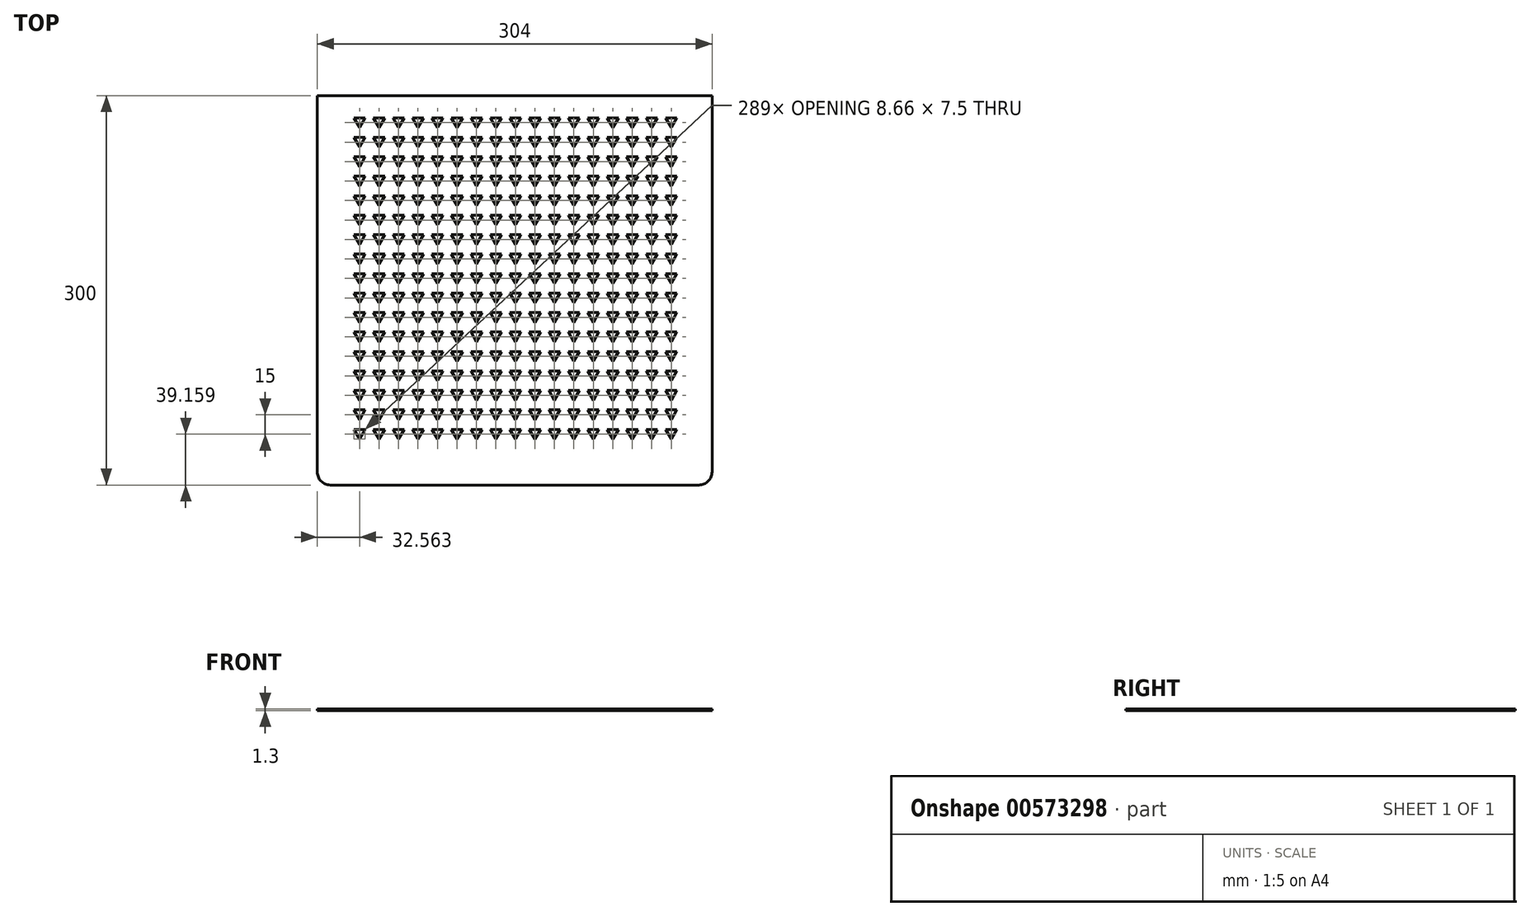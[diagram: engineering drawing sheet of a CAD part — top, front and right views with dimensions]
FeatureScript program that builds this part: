
annotation { "Feature Type Name" : "Feature", "Feature Type Description" : "" }
export const myFeature = defineFeature(function(context is Context, id is Id, definition is map)
    precondition{}
    {
        {
            var Q0;
            Q0=qCreatedBy(makeId("Top.planeOp"),FACE);
            var sketch = newSketch(context, id + "F0", { "sketchPlane" : qUnion([Q0])});
            skLineSegment(sketch, "E0.bottom", {"start": v(152, 150) * mm, "end": v(-152, 150) * mm});
            skLineSegment(sketch, "E0.top", {"start": v(152, -150) * mm, "end": v(-152, -150) * mm});
            skLineSegment(sketch, "E0.left", {"start": v(152, 150) * mm, "end": v(152, -150) * mm});
            skLineSegment(sketch, "E0.right", {"start": v(-152, 150) * mm, "end": v(-152, -150) * mm});
            skPoint(sketch, "E0.middle", {"position": v(0, 0) * mm});
            skSolve(sketch);
        }
        {
            var Q0;
            Q0=makeQuery(id+"F0.imprint","IMPRINT",FACE,{"disambiguationData":[TD([[makeQuery(id+"F0.imprint","IMPRINT",EDGE,{"derivedFrom":sQuery(id+"F0.wireOp",EDGE,"E0.bottom")}),1.0]])]});
            extrude(context, id + "F1", {"entities" : qUnion([Q0]), "depth" : 1.3 * mm, "offsetDistance" : 25 * mm});
        }
        {
            var Q0;
            Q0=makeQuery(id+"F1.opExtrude","SWEPT_EDGE",EDGE,{"disambiguationData":[OSD([sQuery(id+"F0.wireOp",EDGE,"E0.top"),sQuery(id+"F0.wireOp",EDGE,"E0.left")])]});
            var Q1;
            Q1=makeQuery(id+"F1.opExtrude","SWEPT_EDGE",EDGE,{"disambiguationData":[OSD([sQuery(id+"F0.wireOp",EDGE,"E0.top"),sQuery(id+"F0.wireOp",EDGE,"E0.right")])]});
            fillet(context, id + "F2", {"entities" : qUnion([Q0, Q1]), "radius" : 10 * mm, "tangentPropagation" : true, "allowEdgeOverflow" : false});
        }
        {
            var Q0;
            Q0=makeQuery(id+"F1.opExtrude","CAP_FACE",FACE,{"disambiguationData":[OSD([sQuery(id+"F0.wireOp",EDGE,"E0.bottom"),sQuery(id+"F0.wireOp",EDGE,"E0.top"),sQuery(id+"F0.wireOp",EDGE,"E0.left"),sQuery(id+"F0.wireOp",EDGE,"E0.right")])],"isStart":false});
            var sketch = newSketch(context, id + "F3", { "sketchPlane" : qUnion([Q0])});
            skLineSegment(sketch, "E1.0", {"start": v(-123.77, 132.9) * mm, "end": v(-115.1, 132.9) * mm});
            skLineSegment(sketch, "E1.1", {"start": v(-115.1, 132.9) * mm, "end": v(-119.44, 125.41) * mm});
            skLineSegment(sketch, "E1.2", {"start": v(-119.44, 125.41) * mm, "end": v(-123.77, 132.9) * mm});
            skPoint(sketch, "E1.0.midPoint", {"position": v(-119.44, 132.9) * mm});
            skLineSegment(sketch, "E2.0.1.0", {"start": v(-115.1, 117.9) * mm, "end": v(-119.44, 110.41) * mm});
            skLineSegment(sketch, "E2.0.1.1", {"start": v(-119.44, 110.41) * mm, "end": v(-123.77, 117.9) * mm});
            skLineSegment(sketch, "E2.0.1.2", {"start": v(-123.77, 117.9) * mm, "end": v(-115.1, 117.9) * mm});
            skLineSegment(sketch, "E2.0.2.0", {"start": v(-115.1, 102.9) * mm, "end": v(-119.44, 95.41) * mm});
            skLineSegment(sketch, "E2.0.2.1", {"start": v(-119.44, 95.41) * mm, "end": v(-123.77, 102.9) * mm});
            skLineSegment(sketch, "E2.0.2.2", {"start": v(-123.77, 102.9) * mm, "end": v(-115.1, 102.9) * mm});
            skLineSegment(sketch, "E2.0.3.0", {"start": v(-115.1, 87.9) * mm, "end": v(-119.44, 80.41) * mm});
            skLineSegment(sketch, "E2.0.3.1", {"start": v(-119.44, 80.41) * mm, "end": v(-123.77, 87.9) * mm});
            skLineSegment(sketch, "E2.0.3.2", {"start": v(-123.77, 87.9) * mm, "end": v(-115.1, 87.9) * mm});
            skLineSegment(sketch, "E2.0.4.0", {"start": v(-115.1, 72.9) * mm, "end": v(-119.44, 65.41) * mm});
            skLineSegment(sketch, "E2.0.4.1", {"start": v(-119.44, 65.41) * mm, "end": v(-123.77, 72.9) * mm});
            skLineSegment(sketch, "E2.0.4.2", {"start": v(-123.77, 72.9) * mm, "end": v(-115.1, 72.9) * mm});
            skLineSegment(sketch, "E2.0.5.0", {"start": v(-115.1, 57.9) * mm, "end": v(-119.44, 50.41) * mm});
            skLineSegment(sketch, "E2.0.5.1", {"start": v(-119.44, 50.41) * mm, "end": v(-123.77, 57.9) * mm});
            skLineSegment(sketch, "E2.0.5.2", {"start": v(-123.77, 57.9) * mm, "end": v(-115.1, 57.9) * mm});
            skLineSegment(sketch, "E2.0.6.0", {"start": v(-115.1, 42.9) * mm, "end": v(-119.44, 35.41) * mm});
            skLineSegment(sketch, "E2.0.6.1", {"start": v(-119.44, 35.41) * mm, "end": v(-123.77, 42.9) * mm});
            skLineSegment(sketch, "E2.0.6.2", {"start": v(-123.77, 42.9) * mm, "end": v(-115.1, 42.9) * mm});
            skLineSegment(sketch, "E2.0.7.0", {"start": v(-115.1, 27.9) * mm, "end": v(-119.44, 20.41) * mm});
            skLineSegment(sketch, "E2.0.7.1", {"start": v(-119.44, 20.41) * mm, "end": v(-123.77, 27.9) * mm});
            skLineSegment(sketch, "E2.0.7.2", {"start": v(-123.77, 27.9) * mm, "end": v(-115.1, 27.9) * mm});
            skLineSegment(sketch, "E2.0.8.0", {"start": v(-115.1, 12.9) * mm, "end": v(-119.44, 5.41) * mm});
            skLineSegment(sketch, "E2.0.8.1", {"start": v(-119.44, 5.41) * mm, "end": v(-123.77, 12.9) * mm});
            skLineSegment(sketch, "E2.0.8.2", {"start": v(-123.77, 12.9) * mm, "end": v(-115.1, 12.9) * mm});
            skLineSegment(sketch, "E2.0.9.0", {"start": v(-115.1, -2.1) * mm, "end": v(-119.44, -9.59) * mm});
            skLineSegment(sketch, "E2.0.9.1", {"start": v(-119.44, -9.59) * mm, "end": v(-123.77, -2.1) * mm});
            skLineSegment(sketch, "E2.0.9.2", {"start": v(-123.77, -2.1) * mm, "end": v(-115.1, -2.1) * mm});
            skLineSegment(sketch, "E2.0.10.0", {"start": v(-115.1, -17.1) * mm, "end": v(-119.44, -24.59) * mm});
            skLineSegment(sketch, "E2.0.10.1", {"start": v(-119.44, -24.59) * mm, "end": v(-123.77, -17.1) * mm});
            skLineSegment(sketch, "E2.0.10.2", {"start": v(-123.77, -17.1) * mm, "end": v(-115.1, -17.1) * mm});
            skLineSegment(sketch, "E2.0.11.0", {"start": v(-115.1, -32.1) * mm, "end": v(-119.44, -39.59) * mm});
            skLineSegment(sketch, "E2.0.11.1", {"start": v(-119.44, -39.59) * mm, "end": v(-123.77, -32.1) * mm});
            skLineSegment(sketch, "E2.0.11.2", {"start": v(-123.77, -32.1) * mm, "end": v(-115.1, -32.1) * mm});
            skLineSegment(sketch, "E2.0.12.0", {"start": v(-115.1, -47.1) * mm, "end": v(-119.44, -54.59) * mm});
            skLineSegment(sketch, "E2.0.12.1", {"start": v(-119.44, -54.59) * mm, "end": v(-123.77, -47.1) * mm});
            skLineSegment(sketch, "E2.0.12.2", {"start": v(-123.77, -47.1) * mm, "end": v(-115.1, -47.1) * mm});
            skLineSegment(sketch, "E2.0.13.0", {"start": v(-115.1, -62.1) * mm, "end": v(-119.44, -69.59) * mm});
            skLineSegment(sketch, "E2.0.13.1", {"start": v(-119.44, -69.59) * mm, "end": v(-123.77, -62.1) * mm});
            skLineSegment(sketch, "E2.0.13.2", {"start": v(-123.77, -62.1) * mm, "end": v(-115.1, -62.1) * mm});
            skLineSegment(sketch, "E2.0.14.0", {"start": v(-115.1, -77.1) * mm, "end": v(-119.44, -84.59) * mm});
            skLineSegment(sketch, "E2.0.14.1", {"start": v(-119.44, -84.59) * mm, "end": v(-123.77, -77.1) * mm});
            skLineSegment(sketch, "E2.0.14.2", {"start": v(-123.77, -77.1) * mm, "end": v(-115.1, -77.1) * mm});
            skLineSegment(sketch, "E2.0.15.0", {"start": v(-115.1, -92.1) * mm, "end": v(-119.44, -99.59) * mm});
            skLineSegment(sketch, "E2.0.15.1", {"start": v(-119.44, -99.59) * mm, "end": v(-123.77, -92.1) * mm});
            skLineSegment(sketch, "E2.0.15.2", {"start": v(-123.77, -92.1) * mm, "end": v(-115.1, -92.1) * mm});
            skLineSegment(sketch, "E2.0.16.0", {"start": v(-115.1, -107.1) * mm, "end": v(-119.44, -114.59) * mm});
            skLineSegment(sketch, "E2.0.16.1", {"start": v(-119.44, -114.59) * mm, "end": v(-123.77, -107.1) * mm});
            skLineSegment(sketch, "E2.0.16.2", {"start": v(-123.77, -107.1) * mm, "end": v(-115.1, -107.1) * mm});
            skLineSegment(sketch, "E2.1.0.0", {"start": v(-100.1, 132.9) * mm, "end": v(-104.44, 125.41) * mm});
            skLineSegment(sketch, "E2.1.0.1", {"start": v(-104.44, 125.41) * mm, "end": v(-108.77, 132.9) * mm});
            skLineSegment(sketch, "E2.1.0.2", {"start": v(-108.77, 132.9) * mm, "end": v(-100.1, 132.9) * mm});
            skLineSegment(sketch, "E2.1.1.0", {"start": v(-100.1, 117.9) * mm, "end": v(-104.44, 110.41) * mm});
            skLineSegment(sketch, "E2.1.1.1", {"start": v(-104.44, 110.41) * mm, "end": v(-108.77, 117.9) * mm});
            skLineSegment(sketch, "E2.1.1.2", {"start": v(-108.77, 117.9) * mm, "end": v(-100.1, 117.9) * mm});
            skLineSegment(sketch, "E2.1.2.0", {"start": v(-100.1, 102.9) * mm, "end": v(-104.44, 95.41) * mm});
            skLineSegment(sketch, "E2.1.2.1", {"start": v(-104.44, 95.41) * mm, "end": v(-108.77, 102.9) * mm});
            skLineSegment(sketch, "E2.1.2.2", {"start": v(-108.77, 102.9) * mm, "end": v(-100.1, 102.9) * mm});
            skLineSegment(sketch, "E2.1.3.0", {"start": v(-100.1, 87.9) * mm, "end": v(-104.44, 80.41) * mm});
            skLineSegment(sketch, "E2.1.3.1", {"start": v(-104.44, 80.41) * mm, "end": v(-108.77, 87.9) * mm});
            skLineSegment(sketch, "E2.1.3.2", {"start": v(-108.77, 87.9) * mm, "end": v(-100.1, 87.9) * mm});
            skLineSegment(sketch, "E2.1.4.0", {"start": v(-100.1, 72.9) * mm, "end": v(-104.44, 65.41) * mm});
            skLineSegment(sketch, "E2.1.4.1", {"start": v(-104.44, 65.41) * mm, "end": v(-108.77, 72.9) * mm});
            skLineSegment(sketch, "E2.1.4.2", {"start": v(-108.77, 72.9) * mm, "end": v(-100.1, 72.9) * mm});
            skLineSegment(sketch, "E2.1.5.0", {"start": v(-100.1, 57.9) * mm, "end": v(-104.44, 50.41) * mm});
            skLineSegment(sketch, "E2.1.5.1", {"start": v(-104.44, 50.41) * mm, "end": v(-108.77, 57.9) * mm});
            skLineSegment(sketch, "E2.1.5.2", {"start": v(-108.77, 57.9) * mm, "end": v(-100.1, 57.9) * mm});
            skLineSegment(sketch, "E2.1.6.0", {"start": v(-100.1, 42.9) * mm, "end": v(-104.44, 35.41) * mm});
            skLineSegment(sketch, "E2.1.6.1", {"start": v(-104.44, 35.41) * mm, "end": v(-108.77, 42.9) * mm});
            skLineSegment(sketch, "E2.1.6.2", {"start": v(-108.77, 42.9) * mm, "end": v(-100.1, 42.9) * mm});
            skLineSegment(sketch, "E2.1.7.0", {"start": v(-100.1, 27.9) * mm, "end": v(-104.44, 20.41) * mm});
            skLineSegment(sketch, "E2.1.7.1", {"start": v(-104.44, 20.41) * mm, "end": v(-108.77, 27.9) * mm});
            skLineSegment(sketch, "E2.1.7.2", {"start": v(-108.77, 27.9) * mm, "end": v(-100.1, 27.9) * mm});
            skLineSegment(sketch, "E2.1.8.0", {"start": v(-100.1, 12.9) * mm, "end": v(-104.44, 5.41) * mm});
            skLineSegment(sketch, "E2.1.8.1", {"start": v(-104.44, 5.41) * mm, "end": v(-108.77, 12.9) * mm});
            skLineSegment(sketch, "E2.1.8.2", {"start": v(-108.77, 12.9) * mm, "end": v(-100.1, 12.9) * mm});
            skLineSegment(sketch, "E2.1.9.0", {"start": v(-100.1, -2.1) * mm, "end": v(-104.44, -9.59) * mm});
            skLineSegment(sketch, "E2.1.9.1", {"start": v(-104.44, -9.59) * mm, "end": v(-108.77, -2.1) * mm});
            skLineSegment(sketch, "E2.1.9.2", {"start": v(-108.77, -2.1) * mm, "end": v(-100.1, -2.1) * mm});
            skLineSegment(sketch, "E2.1.10.0", {"start": v(-100.1, -17.1) * mm, "end": v(-104.44, -24.59) * mm});
            skLineSegment(sketch, "E2.1.10.1", {"start": v(-104.44, -24.59) * mm, "end": v(-108.77, -17.1) * mm});
            skLineSegment(sketch, "E2.1.10.2", {"start": v(-108.77, -17.1) * mm, "end": v(-100.1, -17.1) * mm});
            skLineSegment(sketch, "E2.1.11.0", {"start": v(-100.1, -32.1) * mm, "end": v(-104.44, -39.59) * mm});
            skLineSegment(sketch, "E2.1.11.1", {"start": v(-104.44, -39.59) * mm, "end": v(-108.77, -32.1) * mm});
            skLineSegment(sketch, "E2.1.11.2", {"start": v(-108.77, -32.1) * mm, "end": v(-100.1, -32.1) * mm});
            skLineSegment(sketch, "E2.1.12.0", {"start": v(-100.1, -47.1) * mm, "end": v(-104.44, -54.59) * mm});
            skLineSegment(sketch, "E2.1.12.1", {"start": v(-104.44, -54.59) * mm, "end": v(-108.77, -47.1) * mm});
            skLineSegment(sketch, "E2.1.12.2", {"start": v(-108.77, -47.1) * mm, "end": v(-100.1, -47.1) * mm});
            skLineSegment(sketch, "E2.1.13.0", {"start": v(-100.1, -62.1) * mm, "end": v(-104.44, -69.59) * mm});
            skLineSegment(sketch, "E2.1.13.1", {"start": v(-104.44, -69.59) * mm, "end": v(-108.77, -62.1) * mm});
            skLineSegment(sketch, "E2.1.13.2", {"start": v(-108.77, -62.1) * mm, "end": v(-100.1, -62.1) * mm});
            skLineSegment(sketch, "E2.1.14.0", {"start": v(-100.1, -77.1) * mm, "end": v(-104.44, -84.59) * mm});
            skLineSegment(sketch, "E2.1.14.1", {"start": v(-104.44, -84.59) * mm, "end": v(-108.77, -77.1) * mm});
            skLineSegment(sketch, "E2.1.14.2", {"start": v(-108.77, -77.1) * mm, "end": v(-100.1, -77.1) * mm});
            skLineSegment(sketch, "E2.1.15.0", {"start": v(-100.1, -92.1) * mm, "end": v(-104.44, -99.59) * mm});
            skLineSegment(sketch, "E2.1.15.1", {"start": v(-104.44, -99.59) * mm, "end": v(-108.77, -92.1) * mm});
            skLineSegment(sketch, "E2.1.15.2", {"start": v(-108.77, -92.1) * mm, "end": v(-100.1, -92.1) * mm});
            skLineSegment(sketch, "E2.1.16.0", {"start": v(-100.1, -107.1) * mm, "end": v(-104.44, -114.59) * mm});
            skLineSegment(sketch, "E2.1.16.1", {"start": v(-104.44, -114.59) * mm, "end": v(-108.77, -107.1) * mm});
            skLineSegment(sketch, "E2.1.16.2", {"start": v(-108.77, -107.1) * mm, "end": v(-100.1, -107.1) * mm});
            skLineSegment(sketch, "E2.2.0.0", {"start": v(-85.1, 132.9) * mm, "end": v(-89.44, 125.41) * mm});
            skLineSegment(sketch, "E2.2.0.1", {"start": v(-89.44, 125.41) * mm, "end": v(-93.77, 132.9) * mm});
            skLineSegment(sketch, "E2.2.0.2", {"start": v(-93.77, 132.9) * mm, "end": v(-85.1, 132.9) * mm});
            skLineSegment(sketch, "E2.2.1.0", {"start": v(-85.1, 117.9) * mm, "end": v(-89.44, 110.41) * mm});
            skLineSegment(sketch, "E2.2.1.1", {"start": v(-89.44, 110.41) * mm, "end": v(-93.77, 117.9) * mm});
            skLineSegment(sketch, "E2.2.1.2", {"start": v(-93.77, 117.9) * mm, "end": v(-85.1, 117.9) * mm});
            skLineSegment(sketch, "E2.2.2.0", {"start": v(-85.1, 102.9) * mm, "end": v(-89.44, 95.41) * mm});
            skLineSegment(sketch, "E2.2.2.1", {"start": v(-89.44, 95.41) * mm, "end": v(-93.77, 102.9) * mm});
            skLineSegment(sketch, "E2.2.2.2", {"start": v(-93.77, 102.9) * mm, "end": v(-85.1, 102.9) * mm});
            skLineSegment(sketch, "E2.2.3.0", {"start": v(-85.1, 87.9) * mm, "end": v(-89.44, 80.41) * mm});
            skLineSegment(sketch, "E2.2.3.1", {"start": v(-89.44, 80.41) * mm, "end": v(-93.77, 87.9) * mm});
            skLineSegment(sketch, "E2.2.3.2", {"start": v(-93.77, 87.9) * mm, "end": v(-85.1, 87.9) * mm});
            skLineSegment(sketch, "E2.2.4.0", {"start": v(-85.1, 72.9) * mm, "end": v(-89.44, 65.41) * mm});
            skLineSegment(sketch, "E2.2.4.1", {"start": v(-89.44, 65.41) * mm, "end": v(-93.77, 72.9) * mm});
            skLineSegment(sketch, "E2.2.4.2", {"start": v(-93.77, 72.9) * mm, "end": v(-85.1, 72.9) * mm});
            skLineSegment(sketch, "E2.2.5.0", {"start": v(-85.1, 57.9) * mm, "end": v(-89.44, 50.41) * mm});
            skLineSegment(sketch, "E2.2.5.1", {"start": v(-89.44, 50.41) * mm, "end": v(-93.77, 57.9) * mm});
            skLineSegment(sketch, "E2.2.5.2", {"start": v(-93.77, 57.9) * mm, "end": v(-85.1, 57.9) * mm});
            skLineSegment(sketch, "E2.2.6.0", {"start": v(-85.1, 42.9) * mm, "end": v(-89.44, 35.41) * mm});
            skLineSegment(sketch, "E2.2.6.1", {"start": v(-89.44, 35.41) * mm, "end": v(-93.77, 42.9) * mm});
            skLineSegment(sketch, "E2.2.6.2", {"start": v(-93.77, 42.9) * mm, "end": v(-85.1, 42.9) * mm});
            skLineSegment(sketch, "E2.2.7.0", {"start": v(-85.1, 27.9) * mm, "end": v(-89.44, 20.41) * mm});
            skLineSegment(sketch, "E2.2.7.1", {"start": v(-89.44, 20.41) * mm, "end": v(-93.77, 27.9) * mm});
            skLineSegment(sketch, "E2.2.7.2", {"start": v(-93.77, 27.9) * mm, "end": v(-85.1, 27.9) * mm});
            skLineSegment(sketch, "E2.2.8.0", {"start": v(-85.1, 12.9) * mm, "end": v(-89.44, 5.41) * mm});
            skLineSegment(sketch, "E2.2.8.1", {"start": v(-89.44, 5.41) * mm, "end": v(-93.77, 12.9) * mm});
            skLineSegment(sketch, "E2.2.8.2", {"start": v(-93.77, 12.9) * mm, "end": v(-85.1, 12.9) * mm});
            skLineSegment(sketch, "E2.2.9.0", {"start": v(-85.1, -2.1) * mm, "end": v(-89.44, -9.59) * mm});
            skLineSegment(sketch, "E2.2.9.1", {"start": v(-89.44, -9.59) * mm, "end": v(-93.77, -2.1) * mm});
            skLineSegment(sketch, "E2.2.9.2", {"start": v(-93.77, -2.1) * mm, "end": v(-85.1, -2.1) * mm});
            skLineSegment(sketch, "E2.2.10.0", {"start": v(-85.1, -17.1) * mm, "end": v(-89.44, -24.59) * mm});
            skLineSegment(sketch, "E2.2.10.1", {"start": v(-89.44, -24.59) * mm, "end": v(-93.77, -17.1) * mm});
            skLineSegment(sketch, "E2.2.10.2", {"start": v(-93.77, -17.1) * mm, "end": v(-85.1, -17.1) * mm});
            skLineSegment(sketch, "E2.2.11.0", {"start": v(-85.1, -32.1) * mm, "end": v(-89.44, -39.59) * mm});
            skLineSegment(sketch, "E2.2.11.1", {"start": v(-89.44, -39.59) * mm, "end": v(-93.77, -32.1) * mm});
            skLineSegment(sketch, "E2.2.11.2", {"start": v(-93.77, -32.1) * mm, "end": v(-85.1, -32.1) * mm});
            skLineSegment(sketch, "E2.2.12.0", {"start": v(-85.1, -47.1) * mm, "end": v(-89.44, -54.59) * mm});
            skLineSegment(sketch, "E2.2.12.1", {"start": v(-89.44, -54.59) * mm, "end": v(-93.77, -47.1) * mm});
            skLineSegment(sketch, "E2.2.12.2", {"start": v(-93.77, -47.1) * mm, "end": v(-85.1, -47.1) * mm});
            skLineSegment(sketch, "E2.2.13.0", {"start": v(-85.1, -62.1) * mm, "end": v(-89.44, -69.59) * mm});
            skLineSegment(sketch, "E2.2.13.1", {"start": v(-89.44, -69.59) * mm, "end": v(-93.77, -62.1) * mm});
            skLineSegment(sketch, "E2.2.13.2", {"start": v(-93.77, -62.1) * mm, "end": v(-85.1, -62.1) * mm});
            skLineSegment(sketch, "E2.2.14.0", {"start": v(-85.1, -77.1) * mm, "end": v(-89.44, -84.59) * mm});
            skLineSegment(sketch, "E2.2.14.1", {"start": v(-89.44, -84.59) * mm, "end": v(-93.77, -77.1) * mm});
            skLineSegment(sketch, "E2.2.14.2", {"start": v(-93.77, -77.1) * mm, "end": v(-85.1, -77.1) * mm});
            skLineSegment(sketch, "E2.2.15.0", {"start": v(-85.1, -92.1) * mm, "end": v(-89.44, -99.59) * mm});
            skLineSegment(sketch, "E2.2.15.1", {"start": v(-89.44, -99.59) * mm, "end": v(-93.77, -92.1) * mm});
            skLineSegment(sketch, "E2.2.15.2", {"start": v(-93.77, -92.1) * mm, "end": v(-85.1, -92.1) * mm});
            skLineSegment(sketch, "E2.2.16.0", {"start": v(-85.1, -107.1) * mm, "end": v(-89.44, -114.59) * mm});
            skLineSegment(sketch, "E2.2.16.1", {"start": v(-89.44, -114.59) * mm, "end": v(-93.77, -107.1) * mm});
            skLineSegment(sketch, "E2.2.16.2", {"start": v(-93.77, -107.1) * mm, "end": v(-85.1, -107.1) * mm});
            skLineSegment(sketch, "E2.3.0.0", {"start": v(-70.1, 132.9) * mm, "end": v(-74.44, 125.41) * mm});
            skLineSegment(sketch, "E2.3.0.1", {"start": v(-74.44, 125.41) * mm, "end": v(-78.77, 132.9) * mm});
            skLineSegment(sketch, "E2.3.0.2", {"start": v(-78.77, 132.9) * mm, "end": v(-70.1, 132.9) * mm});
            skLineSegment(sketch, "E2.3.1.0", {"start": v(-70.1, 117.9) * mm, "end": v(-74.44, 110.41) * mm});
            skLineSegment(sketch, "E2.3.1.1", {"start": v(-74.44, 110.41) * mm, "end": v(-78.77, 117.9) * mm});
            skLineSegment(sketch, "E2.3.1.2", {"start": v(-78.77, 117.9) * mm, "end": v(-70.1, 117.9) * mm});
            skLineSegment(sketch, "E2.3.2.0", {"start": v(-70.1, 102.9) * mm, "end": v(-74.44, 95.41) * mm});
            skLineSegment(sketch, "E2.3.2.1", {"start": v(-74.44, 95.41) * mm, "end": v(-78.77, 102.9) * mm});
            skLineSegment(sketch, "E2.3.2.2", {"start": v(-78.77, 102.9) * mm, "end": v(-70.1, 102.9) * mm});
            skLineSegment(sketch, "E2.3.3.0", {"start": v(-70.1, 87.9) * mm, "end": v(-74.44, 80.41) * mm});
            skLineSegment(sketch, "E2.3.3.1", {"start": v(-74.44, 80.41) * mm, "end": v(-78.77, 87.9) * mm});
            skLineSegment(sketch, "E2.3.3.2", {"start": v(-78.77, 87.9) * mm, "end": v(-70.1, 87.9) * mm});
            skLineSegment(sketch, "E2.3.4.0", {"start": v(-70.1, 72.9) * mm, "end": v(-74.44, 65.41) * mm});
            skLineSegment(sketch, "E2.3.4.1", {"start": v(-74.44, 65.41) * mm, "end": v(-78.77, 72.9) * mm});
            skLineSegment(sketch, "E2.3.4.2", {"start": v(-78.77, 72.9) * mm, "end": v(-70.1, 72.9) * mm});
            skLineSegment(sketch, "E2.3.5.0", {"start": v(-70.1, 57.9) * mm, "end": v(-74.44, 50.41) * mm});
            skLineSegment(sketch, "E2.3.5.1", {"start": v(-74.44, 50.41) * mm, "end": v(-78.77, 57.9) * mm});
            skLineSegment(sketch, "E2.3.5.2", {"start": v(-78.77, 57.9) * mm, "end": v(-70.1, 57.9) * mm});
            skLineSegment(sketch, "E2.3.6.0", {"start": v(-70.1, 42.9) * mm, "end": v(-74.44, 35.41) * mm});
            skLineSegment(sketch, "E2.3.6.1", {"start": v(-74.44, 35.41) * mm, "end": v(-78.77, 42.9) * mm});
            skLineSegment(sketch, "E2.3.6.2", {"start": v(-78.77, 42.9) * mm, "end": v(-70.1, 42.9) * mm});
            skLineSegment(sketch, "E2.3.7.0", {"start": v(-70.1, 27.9) * mm, "end": v(-74.44, 20.41) * mm});
            skLineSegment(sketch, "E2.3.7.1", {"start": v(-74.44, 20.41) * mm, "end": v(-78.77, 27.9) * mm});
            skLineSegment(sketch, "E2.3.7.2", {"start": v(-78.77, 27.9) * mm, "end": v(-70.1, 27.9) * mm});
            skLineSegment(sketch, "E2.3.8.0", {"start": v(-70.1, 12.9) * mm, "end": v(-74.44, 5.41) * mm});
            skLineSegment(sketch, "E2.3.8.1", {"start": v(-74.44, 5.41) * mm, "end": v(-78.77, 12.9) * mm});
            skLineSegment(sketch, "E2.3.8.2", {"start": v(-78.77, 12.9) * mm, "end": v(-70.1, 12.9) * mm});
            skLineSegment(sketch, "E2.3.9.0", {"start": v(-70.1, -2.1) * mm, "end": v(-74.44, -9.59) * mm});
            skLineSegment(sketch, "E2.3.9.1", {"start": v(-74.44, -9.59) * mm, "end": v(-78.77, -2.1) * mm});
            skLineSegment(sketch, "E2.3.9.2", {"start": v(-78.77, -2.1) * mm, "end": v(-70.1, -2.1) * mm});
            skLineSegment(sketch, "E2.3.10.0", {"start": v(-70.1, -17.1) * mm, "end": v(-74.44, -24.59) * mm});
            skLineSegment(sketch, "E2.3.10.1", {"start": v(-74.44, -24.59) * mm, "end": v(-78.77, -17.1) * mm});
            skLineSegment(sketch, "E2.3.10.2", {"start": v(-78.77, -17.1) * mm, "end": v(-70.1, -17.1) * mm});
            skLineSegment(sketch, "E2.3.11.0", {"start": v(-70.1, -32.1) * mm, "end": v(-74.44, -39.59) * mm});
            skLineSegment(sketch, "E2.3.11.1", {"start": v(-74.44, -39.59) * mm, "end": v(-78.77, -32.1) * mm});
            skLineSegment(sketch, "E2.3.11.2", {"start": v(-78.77, -32.1) * mm, "end": v(-70.1, -32.1) * mm});
            skLineSegment(sketch, "E2.3.12.0", {"start": v(-70.1, -47.1) * mm, "end": v(-74.44, -54.59) * mm});
            skLineSegment(sketch, "E2.3.12.1", {"start": v(-74.44, -54.59) * mm, "end": v(-78.77, -47.1) * mm});
            skLineSegment(sketch, "E2.3.12.2", {"start": v(-78.77, -47.1) * mm, "end": v(-70.1, -47.1) * mm});
            skLineSegment(sketch, "E2.3.13.0", {"start": v(-70.1, -62.1) * mm, "end": v(-74.44, -69.59) * mm});
            skLineSegment(sketch, "E2.3.13.1", {"start": v(-74.44, -69.59) * mm, "end": v(-78.77, -62.1) * mm});
            skLineSegment(sketch, "E2.3.13.2", {"start": v(-78.77, -62.1) * mm, "end": v(-70.1, -62.1) * mm});
            skLineSegment(sketch, "E2.3.14.0", {"start": v(-70.1, -77.1) * mm, "end": v(-74.44, -84.59) * mm});
            skLineSegment(sketch, "E2.3.14.1", {"start": v(-74.44, -84.59) * mm, "end": v(-78.77, -77.1) * mm});
            skLineSegment(sketch, "E2.3.14.2", {"start": v(-78.77, -77.1) * mm, "end": v(-70.1, -77.1) * mm});
            skLineSegment(sketch, "E2.3.15.0", {"start": v(-70.1, -92.1) * mm, "end": v(-74.44, -99.59) * mm});
            skLineSegment(sketch, "E2.3.15.1", {"start": v(-74.44, -99.59) * mm, "end": v(-78.77, -92.1) * mm});
            skLineSegment(sketch, "E2.3.15.2", {"start": v(-78.77, -92.1) * mm, "end": v(-70.1, -92.1) * mm});
            skLineSegment(sketch, "E2.3.16.0", {"start": v(-70.1, -107.1) * mm, "end": v(-74.44, -114.59) * mm});
            skLineSegment(sketch, "E2.3.16.1", {"start": v(-74.44, -114.59) * mm, "end": v(-78.77, -107.1) * mm});
            skLineSegment(sketch, "E2.3.16.2", {"start": v(-78.77, -107.1) * mm, "end": v(-70.1, -107.1) * mm});
            skLineSegment(sketch, "E2.4.0.0", {"start": v(-55.1, 132.9) * mm, "end": v(-59.44, 125.41) * mm});
            skLineSegment(sketch, "E2.4.0.1", {"start": v(-59.44, 125.41) * mm, "end": v(-63.77, 132.9) * mm});
            skLineSegment(sketch, "E2.4.0.2", {"start": v(-63.77, 132.9) * mm, "end": v(-55.1, 132.9) * mm});
            skLineSegment(sketch, "E2.4.1.0", {"start": v(-55.1, 117.9) * mm, "end": v(-59.44, 110.41) * mm});
            skLineSegment(sketch, "E2.4.1.1", {"start": v(-59.44, 110.41) * mm, "end": v(-63.77, 117.9) * mm});
            skLineSegment(sketch, "E2.4.1.2", {"start": v(-63.77, 117.9) * mm, "end": v(-55.1, 117.9) * mm});
            skLineSegment(sketch, "E2.4.2.0", {"start": v(-55.1, 102.9) * mm, "end": v(-59.44, 95.41) * mm});
            skLineSegment(sketch, "E2.4.2.1", {"start": v(-59.44, 95.41) * mm, "end": v(-63.77, 102.9) * mm});
            skLineSegment(sketch, "E2.4.2.2", {"start": v(-63.77, 102.9) * mm, "end": v(-55.1, 102.9) * mm});
            skLineSegment(sketch, "E2.4.3.0", {"start": v(-55.1, 87.9) * mm, "end": v(-59.44, 80.41) * mm});
            skLineSegment(sketch, "E2.4.3.1", {"start": v(-59.44, 80.41) * mm, "end": v(-63.77, 87.9) * mm});
            skLineSegment(sketch, "E2.4.3.2", {"start": v(-63.77, 87.9) * mm, "end": v(-55.1, 87.9) * mm});
            skLineSegment(sketch, "E2.4.4.0", {"start": v(-55.1, 72.9) * mm, "end": v(-59.44, 65.41) * mm});
            skLineSegment(sketch, "E2.4.4.1", {"start": v(-59.44, 65.41) * mm, "end": v(-63.77, 72.9) * mm});
            skLineSegment(sketch, "E2.4.4.2", {"start": v(-63.77, 72.9) * mm, "end": v(-55.1, 72.9) * mm});
            skLineSegment(sketch, "E2.4.5.0", {"start": v(-55.1, 57.9) * mm, "end": v(-59.44, 50.41) * mm});
            skLineSegment(sketch, "E2.4.5.1", {"start": v(-59.44, 50.41) * mm, "end": v(-63.77, 57.9) * mm});
            skLineSegment(sketch, "E2.4.5.2", {"start": v(-63.77, 57.9) * mm, "end": v(-55.1, 57.9) * mm});
            skLineSegment(sketch, "E2.4.6.0", {"start": v(-55.1, 42.9) * mm, "end": v(-59.44, 35.41) * mm});
            skLineSegment(sketch, "E2.4.6.1", {"start": v(-59.44, 35.41) * mm, "end": v(-63.77, 42.9) * mm});
            skLineSegment(sketch, "E2.4.6.2", {"start": v(-63.77, 42.9) * mm, "end": v(-55.1, 42.9) * mm});
            skLineSegment(sketch, "E2.4.7.0", {"start": v(-55.1, 27.9) * mm, "end": v(-59.44, 20.41) * mm});
            skLineSegment(sketch, "E2.4.7.1", {"start": v(-59.44, 20.41) * mm, "end": v(-63.77, 27.9) * mm});
            skLineSegment(sketch, "E2.4.7.2", {"start": v(-63.77, 27.9) * mm, "end": v(-55.1, 27.9) * mm});
            skLineSegment(sketch, "E2.4.8.0", {"start": v(-55.1, 12.9) * mm, "end": v(-59.44, 5.41) * mm});
            skLineSegment(sketch, "E2.4.8.1", {"start": v(-59.44, 5.41) * mm, "end": v(-63.77, 12.9) * mm});
            skLineSegment(sketch, "E2.4.8.2", {"start": v(-63.77, 12.9) * mm, "end": v(-55.1, 12.9) * mm});
            skLineSegment(sketch, "E2.4.9.0", {"start": v(-55.1, -2.1) * mm, "end": v(-59.44, -9.59) * mm});
            skLineSegment(sketch, "E2.4.9.1", {"start": v(-59.44, -9.59) * mm, "end": v(-63.77, -2.1) * mm});
            skLineSegment(sketch, "E2.4.9.2", {"start": v(-63.77, -2.1) * mm, "end": v(-55.1, -2.1) * mm});
            skLineSegment(sketch, "E2.4.10.0", {"start": v(-55.1, -17.1) * mm, "end": v(-59.44, -24.59) * mm});
            skLineSegment(sketch, "E2.4.10.1", {"start": v(-59.44, -24.59) * mm, "end": v(-63.77, -17.1) * mm});
            skLineSegment(sketch, "E2.4.10.2", {"start": v(-63.77, -17.1) * mm, "end": v(-55.1, -17.1) * mm});
            skLineSegment(sketch, "E2.4.11.0", {"start": v(-55.1, -32.1) * mm, "end": v(-59.44, -39.59) * mm});
            skLineSegment(sketch, "E2.4.11.1", {"start": v(-59.44, -39.59) * mm, "end": v(-63.77, -32.1) * mm});
            skLineSegment(sketch, "E2.4.11.2", {"start": v(-63.77, -32.1) * mm, "end": v(-55.1, -32.1) * mm});
            skLineSegment(sketch, "E2.4.12.0", {"start": v(-55.1, -47.1) * mm, "end": v(-59.44, -54.59) * mm});
            skLineSegment(sketch, "E2.4.12.1", {"start": v(-59.44, -54.59) * mm, "end": v(-63.77, -47.1) * mm});
            skLineSegment(sketch, "E2.4.12.2", {"start": v(-63.77, -47.1) * mm, "end": v(-55.1, -47.1) * mm});
            skLineSegment(sketch, "E2.4.13.0", {"start": v(-55.1, -62.1) * mm, "end": v(-59.44, -69.59) * mm});
            skLineSegment(sketch, "E2.4.13.1", {"start": v(-59.44, -69.59) * mm, "end": v(-63.77, -62.1) * mm});
            skLineSegment(sketch, "E2.4.13.2", {"start": v(-63.77, -62.1) * mm, "end": v(-55.1, -62.1) * mm});
            skLineSegment(sketch, "E2.4.14.0", {"start": v(-55.1, -77.1) * mm, "end": v(-59.44, -84.59) * mm});
            skLineSegment(sketch, "E2.4.14.1", {"start": v(-59.44, -84.59) * mm, "end": v(-63.77, -77.1) * mm});
            skLineSegment(sketch, "E2.4.14.2", {"start": v(-63.77, -77.1) * mm, "end": v(-55.1, -77.1) * mm});
            skLineSegment(sketch, "E2.4.15.0", {"start": v(-55.1, -92.1) * mm, "end": v(-59.44, -99.59) * mm});
            skLineSegment(sketch, "E2.4.15.1", {"start": v(-59.44, -99.59) * mm, "end": v(-63.77, -92.1) * mm});
            skLineSegment(sketch, "E2.4.15.2", {"start": v(-63.77, -92.1) * mm, "end": v(-55.1, -92.1) * mm});
            skLineSegment(sketch, "E2.4.16.0", {"start": v(-55.1, -107.1) * mm, "end": v(-59.44, -114.59) * mm});
            skLineSegment(sketch, "E2.4.16.1", {"start": v(-59.44, -114.59) * mm, "end": v(-63.77, -107.1) * mm});
            skLineSegment(sketch, "E2.4.16.2", {"start": v(-63.77, -107.1) * mm, "end": v(-55.1, -107.1) * mm});
            skLineSegment(sketch, "E2.5.0.0", {"start": v(-40.1, 132.9) * mm, "end": v(-44.44, 125.41) * mm});
            skLineSegment(sketch, "E2.5.0.1", {"start": v(-44.44, 125.41) * mm, "end": v(-48.77, 132.9) * mm});
            skLineSegment(sketch, "E2.5.0.2", {"start": v(-48.77, 132.9) * mm, "end": v(-40.1, 132.9) * mm});
            skLineSegment(sketch, "E2.5.1.0", {"start": v(-40.1, 117.9) * mm, "end": v(-44.44, 110.41) * mm});
            skLineSegment(sketch, "E2.5.1.1", {"start": v(-44.44, 110.41) * mm, "end": v(-48.77, 117.9) * mm});
            skLineSegment(sketch, "E2.5.1.2", {"start": v(-48.77, 117.9) * mm, "end": v(-40.1, 117.9) * mm});
            skLineSegment(sketch, "E2.5.2.0", {"start": v(-40.1, 102.9) * mm, "end": v(-44.44, 95.41) * mm});
            skLineSegment(sketch, "E2.5.2.1", {"start": v(-44.44, 95.41) * mm, "end": v(-48.77, 102.9) * mm});
            skLineSegment(sketch, "E2.5.2.2", {"start": v(-48.77, 102.9) * mm, "end": v(-40.1, 102.9) * mm});
            skLineSegment(sketch, "E2.5.3.0", {"start": v(-40.1, 87.9) * mm, "end": v(-44.44, 80.41) * mm});
            skLineSegment(sketch, "E2.5.3.1", {"start": v(-44.44, 80.41) * mm, "end": v(-48.77, 87.9) * mm});
            skLineSegment(sketch, "E2.5.3.2", {"start": v(-48.77, 87.9) * mm, "end": v(-40.1, 87.9) * mm});
            skLineSegment(sketch, "E2.5.4.0", {"start": v(-40.1, 72.9) * mm, "end": v(-44.44, 65.41) * mm});
            skLineSegment(sketch, "E2.5.4.1", {"start": v(-44.44, 65.41) * mm, "end": v(-48.77, 72.9) * mm});
            skLineSegment(sketch, "E2.5.4.2", {"start": v(-48.77, 72.9) * mm, "end": v(-40.1, 72.9) * mm});
            skLineSegment(sketch, "E2.5.5.0", {"start": v(-40.1, 57.9) * mm, "end": v(-44.44, 50.41) * mm});
            skLineSegment(sketch, "E2.5.5.1", {"start": v(-44.44, 50.41) * mm, "end": v(-48.77, 57.9) * mm});
            skLineSegment(sketch, "E2.5.5.2", {"start": v(-48.77, 57.9) * mm, "end": v(-40.1, 57.9) * mm});
            skLineSegment(sketch, "E2.5.6.0", {"start": v(-40.1, 42.9) * mm, "end": v(-44.44, 35.41) * mm});
            skLineSegment(sketch, "E2.5.6.1", {"start": v(-44.44, 35.41) * mm, "end": v(-48.77, 42.9) * mm});
            skLineSegment(sketch, "E2.5.6.2", {"start": v(-48.77, 42.9) * mm, "end": v(-40.1, 42.9) * mm});
            skLineSegment(sketch, "E2.5.7.0", {"start": v(-40.1, 27.9) * mm, "end": v(-44.44, 20.41) * mm});
            skLineSegment(sketch, "E2.5.7.1", {"start": v(-44.44, 20.41) * mm, "end": v(-48.77, 27.9) * mm});
            skLineSegment(sketch, "E2.5.7.2", {"start": v(-48.77, 27.9) * mm, "end": v(-40.1, 27.9) * mm});
            skLineSegment(sketch, "E2.5.8.0", {"start": v(-40.1, 12.9) * mm, "end": v(-44.44, 5.41) * mm});
            skLineSegment(sketch, "E2.5.8.1", {"start": v(-44.44, 5.41) * mm, "end": v(-48.77, 12.9) * mm});
            skLineSegment(sketch, "E2.5.8.2", {"start": v(-48.77, 12.9) * mm, "end": v(-40.1, 12.9) * mm});
            skLineSegment(sketch, "E2.5.9.0", {"start": v(-40.1, -2.1) * mm, "end": v(-44.44, -9.59) * mm});
            skLineSegment(sketch, "E2.5.9.1", {"start": v(-44.44, -9.59) * mm, "end": v(-48.77, -2.1) * mm});
            skLineSegment(sketch, "E2.5.9.2", {"start": v(-48.77, -2.1) * mm, "end": v(-40.1, -2.1) * mm});
            skLineSegment(sketch, "E2.5.10.0", {"start": v(-40.1, -17.1) * mm, "end": v(-44.44, -24.59) * mm});
            skLineSegment(sketch, "E2.5.10.1", {"start": v(-44.44, -24.59) * mm, "end": v(-48.77, -17.1) * mm});
            skLineSegment(sketch, "E2.5.10.2", {"start": v(-48.77, -17.1) * mm, "end": v(-40.1, -17.1) * mm});
            skLineSegment(sketch, "E2.5.11.0", {"start": v(-40.1, -32.1) * mm, "end": v(-44.44, -39.59) * mm});
            skLineSegment(sketch, "E2.5.11.1", {"start": v(-44.44, -39.59) * mm, "end": v(-48.77, -32.1) * mm});
            skLineSegment(sketch, "E2.5.11.2", {"start": v(-48.77, -32.1) * mm, "end": v(-40.1, -32.1) * mm});
            skLineSegment(sketch, "E2.5.12.0", {"start": v(-40.1, -47.1) * mm, "end": v(-44.44, -54.59) * mm});
            skLineSegment(sketch, "E2.5.12.1", {"start": v(-44.44, -54.59) * mm, "end": v(-48.77, -47.1) * mm});
            skLineSegment(sketch, "E2.5.12.2", {"start": v(-48.77, -47.1) * mm, "end": v(-40.1, -47.1) * mm});
            skLineSegment(sketch, "E2.5.13.0", {"start": v(-40.1, -62.1) * mm, "end": v(-44.44, -69.59) * mm});
            skLineSegment(sketch, "E2.5.13.1", {"start": v(-44.44, -69.59) * mm, "end": v(-48.77, -62.1) * mm});
            skLineSegment(sketch, "E2.5.13.2", {"start": v(-48.77, -62.1) * mm, "end": v(-40.1, -62.1) * mm});
            skLineSegment(sketch, "E2.5.14.0", {"start": v(-40.1, -77.1) * mm, "end": v(-44.44, -84.59) * mm});
            skLineSegment(sketch, "E2.5.14.1", {"start": v(-44.44, -84.59) * mm, "end": v(-48.77, -77.1) * mm});
            skLineSegment(sketch, "E2.5.14.2", {"start": v(-48.77, -77.1) * mm, "end": v(-40.1, -77.1) * mm});
            skLineSegment(sketch, "E2.5.15.0", {"start": v(-40.1, -92.1) * mm, "end": v(-44.44, -99.59) * mm});
            skLineSegment(sketch, "E2.5.15.1", {"start": v(-44.44, -99.59) * mm, "end": v(-48.77, -92.1) * mm});
            skLineSegment(sketch, "E2.5.15.2", {"start": v(-48.77, -92.1) * mm, "end": v(-40.1, -92.1) * mm});
            skLineSegment(sketch, "E2.5.16.0", {"start": v(-40.1, -107.1) * mm, "end": v(-44.44, -114.59) * mm});
            skLineSegment(sketch, "E2.5.16.1", {"start": v(-44.44, -114.59) * mm, "end": v(-48.77, -107.1) * mm});
            skLineSegment(sketch, "E2.5.16.2", {"start": v(-48.77, -107.1) * mm, "end": v(-40.1, -107.1) * mm});
            skLineSegment(sketch, "E2.6.0.0", {"start": v(-25.1, 132.9) * mm, "end": v(-29.44, 125.41) * mm});
            skLineSegment(sketch, "E2.6.0.1", {"start": v(-29.44, 125.41) * mm, "end": v(-33.77, 132.9) * mm});
            skLineSegment(sketch, "E2.6.0.2", {"start": v(-33.77, 132.9) * mm, "end": v(-25.1, 132.9) * mm});
            skLineSegment(sketch, "E2.6.1.0", {"start": v(-25.1, 117.9) * mm, "end": v(-29.44, 110.41) * mm});
            skLineSegment(sketch, "E2.6.1.1", {"start": v(-29.44, 110.41) * mm, "end": v(-33.77, 117.9) * mm});
            skLineSegment(sketch, "E2.6.1.2", {"start": v(-33.77, 117.9) * mm, "end": v(-25.1, 117.9) * mm});
            skLineSegment(sketch, "E2.6.2.0", {"start": v(-25.1, 102.9) * mm, "end": v(-29.44, 95.41) * mm});
            skLineSegment(sketch, "E2.6.2.1", {"start": v(-29.44, 95.41) * mm, "end": v(-33.77, 102.9) * mm});
            skLineSegment(sketch, "E2.6.2.2", {"start": v(-33.77, 102.9) * mm, "end": v(-25.1, 102.9) * mm});
            skLineSegment(sketch, "E2.6.3.0", {"start": v(-25.1, 87.9) * mm, "end": v(-29.44, 80.41) * mm});
            skLineSegment(sketch, "E2.6.3.1", {"start": v(-29.44, 80.41) * mm, "end": v(-33.77, 87.9) * mm});
            skLineSegment(sketch, "E2.6.3.2", {"start": v(-33.77, 87.9) * mm, "end": v(-25.1, 87.9) * mm});
            skLineSegment(sketch, "E2.6.4.0", {"start": v(-25.1, 72.9) * mm, "end": v(-29.44, 65.41) * mm});
            skLineSegment(sketch, "E2.6.4.1", {"start": v(-29.44, 65.41) * mm, "end": v(-33.77, 72.9) * mm});
            skLineSegment(sketch, "E2.6.4.2", {"start": v(-33.77, 72.9) * mm, "end": v(-25.1, 72.9) * mm});
            skLineSegment(sketch, "E2.6.5.0", {"start": v(-25.1, 57.9) * mm, "end": v(-29.44, 50.41) * mm});
            skLineSegment(sketch, "E2.6.5.1", {"start": v(-29.44, 50.41) * mm, "end": v(-33.77, 57.9) * mm});
            skLineSegment(sketch, "E2.6.5.2", {"start": v(-33.77, 57.9) * mm, "end": v(-25.1, 57.9) * mm});
            skLineSegment(sketch, "E2.6.6.0", {"start": v(-25.1, 42.9) * mm, "end": v(-29.44, 35.41) * mm});
            skLineSegment(sketch, "E2.6.6.1", {"start": v(-29.44, 35.41) * mm, "end": v(-33.77, 42.9) * mm});
            skLineSegment(sketch, "E2.6.6.2", {"start": v(-33.77, 42.9) * mm, "end": v(-25.1, 42.9) * mm});
            skLineSegment(sketch, "E2.6.7.0", {"start": v(-25.1, 27.9) * mm, "end": v(-29.44, 20.41) * mm});
            skLineSegment(sketch, "E2.6.7.1", {"start": v(-29.44, 20.41) * mm, "end": v(-33.77, 27.9) * mm});
            skLineSegment(sketch, "E2.6.7.2", {"start": v(-33.77, 27.9) * mm, "end": v(-25.1, 27.9) * mm});
            skLineSegment(sketch, "E2.6.8.0", {"start": v(-25.1, 12.9) * mm, "end": v(-29.44, 5.41) * mm});
            skLineSegment(sketch, "E2.6.8.1", {"start": v(-29.44, 5.41) * mm, "end": v(-33.77, 12.9) * mm});
            skLineSegment(sketch, "E2.6.8.2", {"start": v(-33.77, 12.9) * mm, "end": v(-25.1, 12.9) * mm});
            skLineSegment(sketch, "E2.6.9.0", {"start": v(-25.1, -2.1) * mm, "end": v(-29.44, -9.59) * mm});
            skLineSegment(sketch, "E2.6.9.1", {"start": v(-29.44, -9.59) * mm, "end": v(-33.77, -2.1) * mm});
            skLineSegment(sketch, "E2.6.9.2", {"start": v(-33.77, -2.1) * mm, "end": v(-25.1, -2.1) * mm});
            skLineSegment(sketch, "E2.6.10.0", {"start": v(-25.1, -17.1) * mm, "end": v(-29.44, -24.59) * mm});
            skLineSegment(sketch, "E2.6.10.1", {"start": v(-29.44, -24.59) * mm, "end": v(-33.77, -17.1) * mm});
            skLineSegment(sketch, "E2.6.10.2", {"start": v(-33.77, -17.1) * mm, "end": v(-25.1, -17.1) * mm});
            skLineSegment(sketch, "E2.6.11.0", {"start": v(-25.1, -32.1) * mm, "end": v(-29.44, -39.59) * mm});
            skLineSegment(sketch, "E2.6.11.1", {"start": v(-29.44, -39.59) * mm, "end": v(-33.77, -32.1) * mm});
            skLineSegment(sketch, "E2.6.11.2", {"start": v(-33.77, -32.1) * mm, "end": v(-25.1, -32.1) * mm});
            skLineSegment(sketch, "E2.6.12.0", {"start": v(-25.1, -47.1) * mm, "end": v(-29.44, -54.59) * mm});
            skLineSegment(sketch, "E2.6.12.1", {"start": v(-29.44, -54.59) * mm, "end": v(-33.77, -47.1) * mm});
            skLineSegment(sketch, "E2.6.12.2", {"start": v(-33.77, -47.1) * mm, "end": v(-25.1, -47.1) * mm});
            skLineSegment(sketch, "E2.6.13.0", {"start": v(-25.1, -62.1) * mm, "end": v(-29.44, -69.59) * mm});
            skLineSegment(sketch, "E2.6.13.1", {"start": v(-29.44, -69.59) * mm, "end": v(-33.77, -62.1) * mm});
            skLineSegment(sketch, "E2.6.13.2", {"start": v(-33.77, -62.1) * mm, "end": v(-25.1, -62.1) * mm});
            skLineSegment(sketch, "E2.6.14.0", {"start": v(-25.1, -77.1) * mm, "end": v(-29.44, -84.59) * mm});
            skLineSegment(sketch, "E2.6.14.1", {"start": v(-29.44, -84.59) * mm, "end": v(-33.77, -77.1) * mm});
            skLineSegment(sketch, "E2.6.14.2", {"start": v(-33.77, -77.1) * mm, "end": v(-25.1, -77.1) * mm});
            skLineSegment(sketch, "E2.6.15.0", {"start": v(-25.1, -92.1) * mm, "end": v(-29.44, -99.59) * mm});
            skLineSegment(sketch, "E2.6.15.1", {"start": v(-29.44, -99.59) * mm, "end": v(-33.77, -92.1) * mm});
            skLineSegment(sketch, "E2.6.15.2", {"start": v(-33.77, -92.1) * mm, "end": v(-25.1, -92.1) * mm});
            skLineSegment(sketch, "E2.6.16.0", {"start": v(-25.1, -107.1) * mm, "end": v(-29.44, -114.59) * mm});
            skLineSegment(sketch, "E2.6.16.1", {"start": v(-29.44, -114.59) * mm, "end": v(-33.77, -107.1) * mm});
            skLineSegment(sketch, "E2.6.16.2", {"start": v(-33.77, -107.1) * mm, "end": v(-25.1, -107.1) * mm});
            skLineSegment(sketch, "E2.7.0.0", {"start": v(-10.1, 132.9) * mm, "end": v(-14.44, 125.41) * mm});
            skLineSegment(sketch, "E2.7.0.1", {"start": v(-14.44, 125.41) * mm, "end": v(-18.77, 132.9) * mm});
            skLineSegment(sketch, "E2.7.0.2", {"start": v(-18.77, 132.9) * mm, "end": v(-10.1, 132.9) * mm});
            skLineSegment(sketch, "E2.7.1.0", {"start": v(-10.1, 117.9) * mm, "end": v(-14.44, 110.41) * mm});
            skLineSegment(sketch, "E2.7.1.1", {"start": v(-14.44, 110.41) * mm, "end": v(-18.77, 117.9) * mm});
            skLineSegment(sketch, "E2.7.1.2", {"start": v(-18.77, 117.9) * mm, "end": v(-10.1, 117.9) * mm});
            skLineSegment(sketch, "E2.7.2.0", {"start": v(-10.1, 102.9) * mm, "end": v(-14.44, 95.41) * mm});
            skLineSegment(sketch, "E2.7.2.1", {"start": v(-14.44, 95.41) * mm, "end": v(-18.77, 102.9) * mm});
            skLineSegment(sketch, "E2.7.2.2", {"start": v(-18.77, 102.9) * mm, "end": v(-10.1, 102.9) * mm});
            skLineSegment(sketch, "E2.7.3.0", {"start": v(-10.1, 87.9) * mm, "end": v(-14.44, 80.41) * mm});
            skLineSegment(sketch, "E2.7.3.1", {"start": v(-14.44, 80.41) * mm, "end": v(-18.77, 87.9) * mm});
            skLineSegment(sketch, "E2.7.3.2", {"start": v(-18.77, 87.9) * mm, "end": v(-10.1, 87.9) * mm});
            skLineSegment(sketch, "E2.7.4.0", {"start": v(-10.1, 72.9) * mm, "end": v(-14.44, 65.41) * mm});
            skLineSegment(sketch, "E2.7.4.1", {"start": v(-14.44, 65.41) * mm, "end": v(-18.77, 72.9) * mm});
            skLineSegment(sketch, "E2.7.4.2", {"start": v(-18.77, 72.9) * mm, "end": v(-10.1, 72.9) * mm});
            skLineSegment(sketch, "E2.7.5.0", {"start": v(-10.1, 57.9) * mm, "end": v(-14.44, 50.41) * mm});
            skLineSegment(sketch, "E2.7.5.1", {"start": v(-14.44, 50.41) * mm, "end": v(-18.77, 57.9) * mm});
            skLineSegment(sketch, "E2.7.5.2", {"start": v(-18.77, 57.9) * mm, "end": v(-10.1, 57.9) * mm});
            skLineSegment(sketch, "E2.7.6.0", {"start": v(-10.1, 42.9) * mm, "end": v(-14.44, 35.41) * mm});
            skLineSegment(sketch, "E2.7.6.1", {"start": v(-14.44, 35.41) * mm, "end": v(-18.77, 42.9) * mm});
            skLineSegment(sketch, "E2.7.6.2", {"start": v(-18.77, 42.9) * mm, "end": v(-10.1, 42.9) * mm});
            skLineSegment(sketch, "E2.7.7.0", {"start": v(-10.1, 27.9) * mm, "end": v(-14.44, 20.41) * mm});
            skLineSegment(sketch, "E2.7.7.1", {"start": v(-14.44, 20.41) * mm, "end": v(-18.77, 27.9) * mm});
            skLineSegment(sketch, "E2.7.7.2", {"start": v(-18.77, 27.9) * mm, "end": v(-10.1, 27.9) * mm});
            skLineSegment(sketch, "E2.7.8.0", {"start": v(-10.1, 12.9) * mm, "end": v(-14.44, 5.41) * mm});
            skLineSegment(sketch, "E2.7.8.1", {"start": v(-14.44, 5.41) * mm, "end": v(-18.77, 12.9) * mm});
            skLineSegment(sketch, "E2.7.8.2", {"start": v(-18.77, 12.9) * mm, "end": v(-10.1, 12.9) * mm});
            skLineSegment(sketch, "E2.7.9.0", {"start": v(-10.1, -2.1) * mm, "end": v(-14.44, -9.59) * mm});
            skLineSegment(sketch, "E2.7.9.1", {"start": v(-14.44, -9.59) * mm, "end": v(-18.77, -2.1) * mm});
            skLineSegment(sketch, "E2.7.9.2", {"start": v(-18.77, -2.1) * mm, "end": v(-10.1, -2.1) * mm});
            skLineSegment(sketch, "E2.7.10.0", {"start": v(-10.1, -17.1) * mm, "end": v(-14.44, -24.59) * mm});
            skLineSegment(sketch, "E2.7.10.1", {"start": v(-14.44, -24.59) * mm, "end": v(-18.77, -17.1) * mm});
            skLineSegment(sketch, "E2.7.10.2", {"start": v(-18.77, -17.1) * mm, "end": v(-10.1, -17.1) * mm});
            skLineSegment(sketch, "E2.7.11.0", {"start": v(-10.1, -32.1) * mm, "end": v(-14.44, -39.59) * mm});
            skLineSegment(sketch, "E2.7.11.1", {"start": v(-14.44, -39.59) * mm, "end": v(-18.77, -32.1) * mm});
            skLineSegment(sketch, "E2.7.11.2", {"start": v(-18.77, -32.1) * mm, "end": v(-10.1, -32.1) * mm});
            skLineSegment(sketch, "E2.7.12.0", {"start": v(-10.1, -47.1) * mm, "end": v(-14.44, -54.59) * mm});
            skLineSegment(sketch, "E2.7.12.1", {"start": v(-14.44, -54.59) * mm, "end": v(-18.77, -47.1) * mm});
            skLineSegment(sketch, "E2.7.12.2", {"start": v(-18.77, -47.1) * mm, "end": v(-10.1, -47.1) * mm});
            skLineSegment(sketch, "E2.7.13.0", {"start": v(-10.1, -62.1) * mm, "end": v(-14.44, -69.59) * mm});
            skLineSegment(sketch, "E2.7.13.1", {"start": v(-14.44, -69.59) * mm, "end": v(-18.77, -62.1) * mm});
            skLineSegment(sketch, "E2.7.13.2", {"start": v(-18.77, -62.1) * mm, "end": v(-10.1, -62.1) * mm});
            skLineSegment(sketch, "E2.7.14.0", {"start": v(-10.1, -77.1) * mm, "end": v(-14.44, -84.59) * mm});
            skLineSegment(sketch, "E2.7.14.1", {"start": v(-14.44, -84.59) * mm, "end": v(-18.77, -77.1) * mm});
            skLineSegment(sketch, "E2.7.14.2", {"start": v(-18.77, -77.1) * mm, "end": v(-10.1, -77.1) * mm});
            skLineSegment(sketch, "E2.7.15.0", {"start": v(-10.1, -92.1) * mm, "end": v(-14.44, -99.59) * mm});
            skLineSegment(sketch, "E2.7.15.1", {"start": v(-14.44, -99.59) * mm, "end": v(-18.77, -92.1) * mm});
            skLineSegment(sketch, "E2.7.15.2", {"start": v(-18.77, -92.1) * mm, "end": v(-10.1, -92.1) * mm});
            skLineSegment(sketch, "E2.7.16.0", {"start": v(-10.1, -107.1) * mm, "end": v(-14.44, -114.59) * mm});
            skLineSegment(sketch, "E2.7.16.1", {"start": v(-14.44, -114.59) * mm, "end": v(-18.77, -107.1) * mm});
            skLineSegment(sketch, "E2.7.16.2", {"start": v(-18.77, -107.1) * mm, "end": v(-10.1, -107.1) * mm});
            skLineSegment(sketch, "E2.8.0.0", {"start": v(4.9, 132.9) * mm, "end": v(0.56, 125.41) * mm});
            skLineSegment(sketch, "E2.8.0.1", {"start": v(0.56, 125.41) * mm, "end": v(-3.77, 132.9) * mm});
            skLineSegment(sketch, "E2.8.0.2", {"start": v(-3.77, 132.9) * mm, "end": v(4.9, 132.9) * mm});
            skLineSegment(sketch, "E2.8.1.0", {"start": v(4.9, 117.9) * mm, "end": v(0.56, 110.41) * mm});
            skLineSegment(sketch, "E2.8.1.1", {"start": v(0.56, 110.41) * mm, "end": v(-3.77, 117.9) * mm});
            skLineSegment(sketch, "E2.8.1.2", {"start": v(-3.77, 117.9) * mm, "end": v(4.9, 117.9) * mm});
            skLineSegment(sketch, "E2.8.2.0", {"start": v(4.9, 102.9) * mm, "end": v(0.56, 95.41) * mm});
            skLineSegment(sketch, "E2.8.2.1", {"start": v(0.56, 95.41) * mm, "end": v(-3.77, 102.9) * mm});
            skLineSegment(sketch, "E2.8.2.2", {"start": v(-3.77, 102.9) * mm, "end": v(4.9, 102.9) * mm});
            skLineSegment(sketch, "E2.8.3.0", {"start": v(4.9, 87.9) * mm, "end": v(0.56, 80.41) * mm});
            skLineSegment(sketch, "E2.8.3.1", {"start": v(0.56, 80.41) * mm, "end": v(-3.77, 87.9) * mm});
            skLineSegment(sketch, "E2.8.3.2", {"start": v(-3.77, 87.9) * mm, "end": v(4.9, 87.9) * mm});
            skLineSegment(sketch, "E2.8.4.0", {"start": v(4.9, 72.9) * mm, "end": v(0.56, 65.41) * mm});
            skLineSegment(sketch, "E2.8.4.1", {"start": v(0.56, 65.41) * mm, "end": v(-3.77, 72.9) * mm});
            skLineSegment(sketch, "E2.8.4.2", {"start": v(-3.77, 72.9) * mm, "end": v(4.9, 72.9) * mm});
            skLineSegment(sketch, "E2.8.5.0", {"start": v(4.9, 57.9) * mm, "end": v(0.56, 50.41) * mm});
            skLineSegment(sketch, "E2.8.5.1", {"start": v(0.56, 50.41) * mm, "end": v(-3.77, 57.9) * mm});
            skLineSegment(sketch, "E2.8.5.2", {"start": v(-3.77, 57.9) * mm, "end": v(4.9, 57.9) * mm});
            skLineSegment(sketch, "E2.8.6.0", {"start": v(4.9, 42.9) * mm, "end": v(0.56, 35.41) * mm});
            skLineSegment(sketch, "E2.8.6.1", {"start": v(0.56, 35.41) * mm, "end": v(-3.77, 42.9) * mm});
            skLineSegment(sketch, "E2.8.6.2", {"start": v(-3.77, 42.9) * mm, "end": v(4.9, 42.9) * mm});
            skLineSegment(sketch, "E2.8.7.0", {"start": v(4.9, 27.9) * mm, "end": v(0.56, 20.41) * mm});
            skLineSegment(sketch, "E2.8.7.1", {"start": v(0.56, 20.41) * mm, "end": v(-3.77, 27.9) * mm});
            skLineSegment(sketch, "E2.8.7.2", {"start": v(-3.77, 27.9) * mm, "end": v(4.9, 27.9) * mm});
            skLineSegment(sketch, "E2.8.8.0", {"start": v(4.9, 12.9) * mm, "end": v(0.56, 5.41) * mm});
            skLineSegment(sketch, "E2.8.8.1", {"start": v(0.56, 5.41) * mm, "end": v(-3.77, 12.9) * mm});
            skLineSegment(sketch, "E2.8.8.2", {"start": v(-3.77, 12.9) * mm, "end": v(4.9, 12.9) * mm});
            skLineSegment(sketch, "E2.8.9.0", {"start": v(4.9, -2.1) * mm, "end": v(0.56, -9.59) * mm});
            skLineSegment(sketch, "E2.8.9.1", {"start": v(0.56, -9.59) * mm, "end": v(-3.77, -2.1) * mm});
            skLineSegment(sketch, "E2.8.9.2", {"start": v(-3.77, -2.1) * mm, "end": v(4.9, -2.1) * mm});
            skLineSegment(sketch, "E2.8.10.0", {"start": v(4.9, -17.1) * mm, "end": v(0.56, -24.59) * mm});
            skLineSegment(sketch, "E2.8.10.1", {"start": v(0.56, -24.59) * mm, "end": v(-3.77, -17.1) * mm});
            skLineSegment(sketch, "E2.8.10.2", {"start": v(-3.77, -17.1) * mm, "end": v(4.9, -17.1) * mm});
            skLineSegment(sketch, "E2.8.11.0", {"start": v(4.9, -32.1) * mm, "end": v(0.56, -39.59) * mm});
            skLineSegment(sketch, "E2.8.11.1", {"start": v(0.56, -39.59) * mm, "end": v(-3.77, -32.1) * mm});
            skLineSegment(sketch, "E2.8.11.2", {"start": v(-3.77, -32.1) * mm, "end": v(4.9, -32.1) * mm});
            skLineSegment(sketch, "E2.8.12.0", {"start": v(4.9, -47.1) * mm, "end": v(0.56, -54.59) * mm});
            skLineSegment(sketch, "E2.8.12.1", {"start": v(0.56, -54.59) * mm, "end": v(-3.77, -47.1) * mm});
            skLineSegment(sketch, "E2.8.12.2", {"start": v(-3.77, -47.1) * mm, "end": v(4.9, -47.1) * mm});
            skLineSegment(sketch, "E2.8.13.0", {"start": v(4.9, -62.1) * mm, "end": v(0.56, -69.59) * mm});
            skLineSegment(sketch, "E2.8.13.1", {"start": v(0.56, -69.59) * mm, "end": v(-3.77, -62.1) * mm});
            skLineSegment(sketch, "E2.8.13.2", {"start": v(-3.77, -62.1) * mm, "end": v(4.9, -62.1) * mm});
            skLineSegment(sketch, "E2.8.14.0", {"start": v(4.9, -77.1) * mm, "end": v(0.56, -84.59) * mm});
            skLineSegment(sketch, "E2.8.14.1", {"start": v(0.56, -84.59) * mm, "end": v(-3.77, -77.1) * mm});
            skLineSegment(sketch, "E2.8.14.2", {"start": v(-3.77, -77.1) * mm, "end": v(4.9, -77.1) * mm});
            skLineSegment(sketch, "E2.8.15.0", {"start": v(4.9, -92.1) * mm, "end": v(0.56, -99.59) * mm});
            skLineSegment(sketch, "E2.8.15.1", {"start": v(0.56, -99.59) * mm, "end": v(-3.77, -92.1) * mm});
            skLineSegment(sketch, "E2.8.15.2", {"start": v(-3.77, -92.1) * mm, "end": v(4.9, -92.1) * mm});
            skLineSegment(sketch, "E2.8.16.0", {"start": v(4.9, -107.1) * mm, "end": v(0.56, -114.59) * mm});
            skLineSegment(sketch, "E2.8.16.1", {"start": v(0.56, -114.59) * mm, "end": v(-3.77, -107.1) * mm});
            skLineSegment(sketch, "E2.8.16.2", {"start": v(-3.77, -107.1) * mm, "end": v(4.9, -107.1) * mm});
            skLineSegment(sketch, "E2.9.0.0", {"start": v(19.9, 132.9) * mm, "end": v(15.56, 125.41) * mm});
            skLineSegment(sketch, "E2.9.0.1", {"start": v(15.56, 125.41) * mm, "end": v(11.23, 132.9) * mm});
            skLineSegment(sketch, "E2.9.0.2", {"start": v(11.23, 132.9) * mm, "end": v(19.9, 132.9) * mm});
            skLineSegment(sketch, "E2.9.1.0", {"start": v(19.9, 117.9) * mm, "end": v(15.56, 110.41) * mm});
            skLineSegment(sketch, "E2.9.1.1", {"start": v(15.56, 110.41) * mm, "end": v(11.23, 117.9) * mm});
            skLineSegment(sketch, "E2.9.1.2", {"start": v(11.23, 117.9) * mm, "end": v(19.9, 117.9) * mm});
            skLineSegment(sketch, "E2.9.2.0", {"start": v(19.9, 102.9) * mm, "end": v(15.56, 95.41) * mm});
            skLineSegment(sketch, "E2.9.2.1", {"start": v(15.56, 95.41) * mm, "end": v(11.23, 102.9) * mm});
            skLineSegment(sketch, "E2.9.2.2", {"start": v(11.23, 102.9) * mm, "end": v(19.9, 102.9) * mm});
            skLineSegment(sketch, "E2.9.3.0", {"start": v(19.9, 87.9) * mm, "end": v(15.56, 80.41) * mm});
            skLineSegment(sketch, "E2.9.3.1", {"start": v(15.56, 80.41) * mm, "end": v(11.23, 87.9) * mm});
            skLineSegment(sketch, "E2.9.3.2", {"start": v(11.23, 87.9) * mm, "end": v(19.9, 87.9) * mm});
            skLineSegment(sketch, "E2.9.4.0", {"start": v(19.9, 72.9) * mm, "end": v(15.56, 65.41) * mm});
            skLineSegment(sketch, "E2.9.4.1", {"start": v(15.56, 65.41) * mm, "end": v(11.23, 72.9) * mm});
            skLineSegment(sketch, "E2.9.4.2", {"start": v(11.23, 72.9) * mm, "end": v(19.9, 72.9) * mm});
            skLineSegment(sketch, "E2.9.5.0", {"start": v(19.9, 57.9) * mm, "end": v(15.56, 50.41) * mm});
            skLineSegment(sketch, "E2.9.5.1", {"start": v(15.56, 50.41) * mm, "end": v(11.23, 57.9) * mm});
            skLineSegment(sketch, "E2.9.5.2", {"start": v(11.23, 57.9) * mm, "end": v(19.9, 57.9) * mm});
            skLineSegment(sketch, "E2.9.6.0", {"start": v(19.9, 42.9) * mm, "end": v(15.56, 35.41) * mm});
            skLineSegment(sketch, "E2.9.6.1", {"start": v(15.56, 35.41) * mm, "end": v(11.23, 42.9) * mm});
            skLineSegment(sketch, "E2.9.6.2", {"start": v(11.23, 42.9) * mm, "end": v(19.9, 42.9) * mm});
            skLineSegment(sketch, "E2.9.7.0", {"start": v(19.9, 27.9) * mm, "end": v(15.56, 20.41) * mm});
            skLineSegment(sketch, "E2.9.7.1", {"start": v(15.56, 20.41) * mm, "end": v(11.23, 27.9) * mm});
            skLineSegment(sketch, "E2.9.7.2", {"start": v(11.23, 27.9) * mm, "end": v(19.9, 27.9) * mm});
            skLineSegment(sketch, "E2.9.8.0", {"start": v(19.9, 12.9) * mm, "end": v(15.56, 5.41) * mm});
            skLineSegment(sketch, "E2.9.8.1", {"start": v(15.56, 5.41) * mm, "end": v(11.23, 12.9) * mm});
            skLineSegment(sketch, "E2.9.8.2", {"start": v(11.23, 12.9) * mm, "end": v(19.9, 12.9) * mm});
            skLineSegment(sketch, "E2.9.9.0", {"start": v(19.9, -2.1) * mm, "end": v(15.56, -9.59) * mm});
            skLineSegment(sketch, "E2.9.9.1", {"start": v(15.56, -9.59) * mm, "end": v(11.23, -2.1) * mm});
            skLineSegment(sketch, "E2.9.9.2", {"start": v(11.23, -2.1) * mm, "end": v(19.9, -2.1) * mm});
            skLineSegment(sketch, "E2.9.10.0", {"start": v(19.9, -17.1) * mm, "end": v(15.56, -24.59) * mm});
            skLineSegment(sketch, "E2.9.10.1", {"start": v(15.56, -24.59) * mm, "end": v(11.23, -17.1) * mm});
            skLineSegment(sketch, "E2.9.10.2", {"start": v(11.23, -17.1) * mm, "end": v(19.9, -17.1) * mm});
            skLineSegment(sketch, "E2.9.11.0", {"start": v(19.9, -32.1) * mm, "end": v(15.56, -39.59) * mm});
            skLineSegment(sketch, "E2.9.11.1", {"start": v(15.56, -39.59) * mm, "end": v(11.23, -32.1) * mm});
            skLineSegment(sketch, "E2.9.11.2", {"start": v(11.23, -32.1) * mm, "end": v(19.9, -32.1) * mm});
            skLineSegment(sketch, "E2.9.12.0", {"start": v(19.9, -47.1) * mm, "end": v(15.56, -54.59) * mm});
            skLineSegment(sketch, "E2.9.12.1", {"start": v(15.56, -54.59) * mm, "end": v(11.23, -47.1) * mm});
            skLineSegment(sketch, "E2.9.12.2", {"start": v(11.23, -47.1) * mm, "end": v(19.9, -47.1) * mm});
            skLineSegment(sketch, "E2.9.13.0", {"start": v(19.9, -62.1) * mm, "end": v(15.56, -69.59) * mm});
            skLineSegment(sketch, "E2.9.13.1", {"start": v(15.56, -69.59) * mm, "end": v(11.23, -62.1) * mm});
            skLineSegment(sketch, "E2.9.13.2", {"start": v(11.23, -62.1) * mm, "end": v(19.9, -62.1) * mm});
            skLineSegment(sketch, "E2.9.14.0", {"start": v(19.9, -77.1) * mm, "end": v(15.56, -84.59) * mm});
            skLineSegment(sketch, "E2.9.14.1", {"start": v(15.56, -84.59) * mm, "end": v(11.23, -77.1) * mm});
            skLineSegment(sketch, "E2.9.14.2", {"start": v(11.23, -77.1) * mm, "end": v(19.9, -77.1) * mm});
            skLineSegment(sketch, "E2.9.15.0", {"start": v(19.9, -92.1) * mm, "end": v(15.56, -99.59) * mm});
            skLineSegment(sketch, "E2.9.15.1", {"start": v(15.56, -99.59) * mm, "end": v(11.23, -92.1) * mm});
            skLineSegment(sketch, "E2.9.15.2", {"start": v(11.23, -92.1) * mm, "end": v(19.9, -92.1) * mm});
            skLineSegment(sketch, "E2.9.16.0", {"start": v(19.9, -107.1) * mm, "end": v(15.56, -114.59) * mm});
            skLineSegment(sketch, "E2.9.16.1", {"start": v(15.56, -114.59) * mm, "end": v(11.23, -107.1) * mm});
            skLineSegment(sketch, "E2.9.16.2", {"start": v(11.23, -107.1) * mm, "end": v(19.9, -107.1) * mm});
            skLineSegment(sketch, "E2.10.0.0", {"start": v(34.9, 132.9) * mm, "end": v(30.56, 125.41) * mm});
            skLineSegment(sketch, "E2.10.0.1", {"start": v(30.56, 125.41) * mm, "end": v(26.23, 132.9) * mm});
            skLineSegment(sketch, "E2.10.0.2", {"start": v(26.23, 132.9) * mm, "end": v(34.9, 132.9) * mm});
            skLineSegment(sketch, "E2.10.1.0", {"start": v(34.9, 117.9) * mm, "end": v(30.56, 110.41) * mm});
            skLineSegment(sketch, "E2.10.1.1", {"start": v(30.56, 110.41) * mm, "end": v(26.23, 117.9) * mm});
            skLineSegment(sketch, "E2.10.1.2", {"start": v(26.23, 117.9) * mm, "end": v(34.9, 117.9) * mm});
            skLineSegment(sketch, "E2.10.2.0", {"start": v(34.9, 102.9) * mm, "end": v(30.56, 95.41) * mm});
            skLineSegment(sketch, "E2.10.2.1", {"start": v(30.56, 95.41) * mm, "end": v(26.23, 102.9) * mm});
            skLineSegment(sketch, "E2.10.2.2", {"start": v(26.23, 102.9) * mm, "end": v(34.9, 102.9) * mm});
            skLineSegment(sketch, "E2.10.3.0", {"start": v(34.9, 87.9) * mm, "end": v(30.56, 80.41) * mm});
            skLineSegment(sketch, "E2.10.3.1", {"start": v(30.56, 80.41) * mm, "end": v(26.23, 87.9) * mm});
            skLineSegment(sketch, "E2.10.3.2", {"start": v(26.23, 87.9) * mm, "end": v(34.9, 87.9) * mm});
            skLineSegment(sketch, "E2.10.4.0", {"start": v(34.9, 72.9) * mm, "end": v(30.56, 65.41) * mm});
            skLineSegment(sketch, "E2.10.4.1", {"start": v(30.56, 65.41) * mm, "end": v(26.23, 72.9) * mm});
            skLineSegment(sketch, "E2.10.4.2", {"start": v(26.23, 72.9) * mm, "end": v(34.9, 72.9) * mm});
            skLineSegment(sketch, "E2.10.5.0", {"start": v(34.9, 57.9) * mm, "end": v(30.56, 50.41) * mm});
            skLineSegment(sketch, "E2.10.5.1", {"start": v(30.56, 50.41) * mm, "end": v(26.23, 57.9) * mm});
            skLineSegment(sketch, "E2.10.5.2", {"start": v(26.23, 57.9) * mm, "end": v(34.9, 57.9) * mm});
            skLineSegment(sketch, "E2.10.6.0", {"start": v(34.9, 42.9) * mm, "end": v(30.56, 35.41) * mm});
            skLineSegment(sketch, "E2.10.6.1", {"start": v(30.56, 35.41) * mm, "end": v(26.23, 42.9) * mm});
            skLineSegment(sketch, "E2.10.6.2", {"start": v(26.23, 42.9) * mm, "end": v(34.9, 42.9) * mm});
            skLineSegment(sketch, "E2.10.7.0", {"start": v(34.9, 27.9) * mm, "end": v(30.56, 20.41) * mm});
            skLineSegment(sketch, "E2.10.7.1", {"start": v(30.56, 20.41) * mm, "end": v(26.23, 27.9) * mm});
            skLineSegment(sketch, "E2.10.7.2", {"start": v(26.23, 27.9) * mm, "end": v(34.9, 27.9) * mm});
            skLineSegment(sketch, "E2.10.8.0", {"start": v(34.9, 12.9) * mm, "end": v(30.56, 5.41) * mm});
            skLineSegment(sketch, "E2.10.8.1", {"start": v(30.56, 5.41) * mm, "end": v(26.23, 12.9) * mm});
            skLineSegment(sketch, "E2.10.8.2", {"start": v(26.23, 12.9) * mm, "end": v(34.9, 12.9) * mm});
            skLineSegment(sketch, "E2.10.9.0", {"start": v(34.9, -2.1) * mm, "end": v(30.56, -9.59) * mm});
            skLineSegment(sketch, "E2.10.9.1", {"start": v(30.56, -9.59) * mm, "end": v(26.23, -2.1) * mm});
            skLineSegment(sketch, "E2.10.9.2", {"start": v(26.23, -2.1) * mm, "end": v(34.9, -2.1) * mm});
            skLineSegment(sketch, "E2.10.10.0", {"start": v(34.9, -17.1) * mm, "end": v(30.56, -24.59) * mm});
            skLineSegment(sketch, "E2.10.10.1", {"start": v(30.56, -24.59) * mm, "end": v(26.23, -17.1) * mm});
            skLineSegment(sketch, "E2.10.10.2", {"start": v(26.23, -17.1) * mm, "end": v(34.9, -17.1) * mm});
            skLineSegment(sketch, "E2.10.11.0", {"start": v(34.9, -32.1) * mm, "end": v(30.56, -39.59) * mm});
            skLineSegment(sketch, "E2.10.11.1", {"start": v(30.56, -39.59) * mm, "end": v(26.23, -32.1) * mm});
            skLineSegment(sketch, "E2.10.11.2", {"start": v(26.23, -32.1) * mm, "end": v(34.9, -32.1) * mm});
            skLineSegment(sketch, "E2.10.12.0", {"start": v(34.9, -47.1) * mm, "end": v(30.56, -54.59) * mm});
            skLineSegment(sketch, "E2.10.12.1", {"start": v(30.56, -54.59) * mm, "end": v(26.23, -47.1) * mm});
            skLineSegment(sketch, "E2.10.12.2", {"start": v(26.23, -47.1) * mm, "end": v(34.9, -47.1) * mm});
            skLineSegment(sketch, "E2.10.13.0", {"start": v(34.9, -62.1) * mm, "end": v(30.56, -69.59) * mm});
            skLineSegment(sketch, "E2.10.13.1", {"start": v(30.56, -69.59) * mm, "end": v(26.23, -62.1) * mm});
            skLineSegment(sketch, "E2.10.13.2", {"start": v(26.23, -62.1) * mm, "end": v(34.9, -62.1) * mm});
            skLineSegment(sketch, "E2.10.14.0", {"start": v(34.9, -77.1) * mm, "end": v(30.56, -84.59) * mm});
            skLineSegment(sketch, "E2.10.14.1", {"start": v(30.56, -84.59) * mm, "end": v(26.23, -77.1) * mm});
            skLineSegment(sketch, "E2.10.14.2", {"start": v(26.23, -77.1) * mm, "end": v(34.9, -77.1) * mm});
            skLineSegment(sketch, "E2.10.15.0", {"start": v(34.9, -92.1) * mm, "end": v(30.56, -99.59) * mm});
            skLineSegment(sketch, "E2.10.15.1", {"start": v(30.56, -99.59) * mm, "end": v(26.23, -92.1) * mm});
            skLineSegment(sketch, "E2.10.15.2", {"start": v(26.23, -92.1) * mm, "end": v(34.9, -92.1) * mm});
            skLineSegment(sketch, "E2.10.16.0", {"start": v(34.9, -107.1) * mm, "end": v(30.56, -114.59) * mm});
            skLineSegment(sketch, "E2.10.16.1", {"start": v(30.56, -114.59) * mm, "end": v(26.23, -107.1) * mm});
            skLineSegment(sketch, "E2.10.16.2", {"start": v(26.23, -107.1) * mm, "end": v(34.9, -107.1) * mm});
            skLineSegment(sketch, "E2.11.0.0", {"start": v(49.9, 132.9) * mm, "end": v(45.56, 125.41) * mm});
            skLineSegment(sketch, "E2.11.0.1", {"start": v(45.56, 125.41) * mm, "end": v(41.23, 132.9) * mm});
            skLineSegment(sketch, "E2.11.0.2", {"start": v(41.23, 132.9) * mm, "end": v(49.9, 132.9) * mm});
            skLineSegment(sketch, "E2.11.1.0", {"start": v(49.9, 117.9) * mm, "end": v(45.56, 110.41) * mm});
            skLineSegment(sketch, "E2.11.1.1", {"start": v(45.56, 110.41) * mm, "end": v(41.23, 117.9) * mm});
            skLineSegment(sketch, "E2.11.1.2", {"start": v(41.23, 117.9) * mm, "end": v(49.9, 117.9) * mm});
            skLineSegment(sketch, "E2.11.2.0", {"start": v(49.9, 102.9) * mm, "end": v(45.56, 95.41) * mm});
            skLineSegment(sketch, "E2.11.2.1", {"start": v(45.56, 95.41) * mm, "end": v(41.23, 102.9) * mm});
            skLineSegment(sketch, "E2.11.2.2", {"start": v(41.23, 102.9) * mm, "end": v(49.9, 102.9) * mm});
            skLineSegment(sketch, "E2.11.3.0", {"start": v(49.9, 87.9) * mm, "end": v(45.56, 80.41) * mm});
            skLineSegment(sketch, "E2.11.3.1", {"start": v(45.56, 80.41) * mm, "end": v(41.23, 87.9) * mm});
            skLineSegment(sketch, "E2.11.3.2", {"start": v(41.23, 87.9) * mm, "end": v(49.9, 87.9) * mm});
            skLineSegment(sketch, "E2.11.4.0", {"start": v(49.9, 72.9) * mm, "end": v(45.56, 65.41) * mm});
            skLineSegment(sketch, "E2.11.4.1", {"start": v(45.56, 65.41) * mm, "end": v(41.23, 72.9) * mm});
            skLineSegment(sketch, "E2.11.4.2", {"start": v(41.23, 72.9) * mm, "end": v(49.9, 72.9) * mm});
            skLineSegment(sketch, "E2.11.5.0", {"start": v(49.9, 57.9) * mm, "end": v(45.56, 50.41) * mm});
            skLineSegment(sketch, "E2.11.5.1", {"start": v(45.56, 50.41) * mm, "end": v(41.23, 57.9) * mm});
            skLineSegment(sketch, "E2.11.5.2", {"start": v(41.23, 57.9) * mm, "end": v(49.9, 57.9) * mm});
            skLineSegment(sketch, "E2.11.6.0", {"start": v(49.9, 42.9) * mm, "end": v(45.56, 35.41) * mm});
            skLineSegment(sketch, "E2.11.6.1", {"start": v(45.56, 35.41) * mm, "end": v(41.23, 42.9) * mm});
            skLineSegment(sketch, "E2.11.6.2", {"start": v(41.23, 42.9) * mm, "end": v(49.9, 42.9) * mm});
            skLineSegment(sketch, "E2.11.7.0", {"start": v(49.9, 27.9) * mm, "end": v(45.56, 20.41) * mm});
            skLineSegment(sketch, "E2.11.7.1", {"start": v(45.56, 20.41) * mm, "end": v(41.23, 27.9) * mm});
            skLineSegment(sketch, "E2.11.7.2", {"start": v(41.23, 27.9) * mm, "end": v(49.9, 27.9) * mm});
            skLineSegment(sketch, "E2.11.8.0", {"start": v(49.9, 12.9) * mm, "end": v(45.56, 5.41) * mm});
            skLineSegment(sketch, "E2.11.8.1", {"start": v(45.56, 5.41) * mm, "end": v(41.23, 12.9) * mm});
            skLineSegment(sketch, "E2.11.8.2", {"start": v(41.23, 12.9) * mm, "end": v(49.9, 12.9) * mm});
            skLineSegment(sketch, "E2.11.9.0", {"start": v(49.9, -2.1) * mm, "end": v(45.56, -9.59) * mm});
            skLineSegment(sketch, "E2.11.9.1", {"start": v(45.56, -9.59) * mm, "end": v(41.23, -2.1) * mm});
            skLineSegment(sketch, "E2.11.9.2", {"start": v(41.23, -2.1) * mm, "end": v(49.9, -2.1) * mm});
            skLineSegment(sketch, "E2.11.10.0", {"start": v(49.9, -17.1) * mm, "end": v(45.56, -24.59) * mm});
            skLineSegment(sketch, "E2.11.10.1", {"start": v(45.56, -24.59) * mm, "end": v(41.23, -17.1) * mm});
            skLineSegment(sketch, "E2.11.10.2", {"start": v(41.23, -17.1) * mm, "end": v(49.9, -17.1) * mm});
            skLineSegment(sketch, "E2.11.11.0", {"start": v(49.9, -32.1) * mm, "end": v(45.56, -39.59) * mm});
            skLineSegment(sketch, "E2.11.11.1", {"start": v(45.56, -39.59) * mm, "end": v(41.23, -32.1) * mm});
            skLineSegment(sketch, "E2.11.11.2", {"start": v(41.23, -32.1) * mm, "end": v(49.9, -32.1) * mm});
            skLineSegment(sketch, "E2.11.12.0", {"start": v(49.9, -47.1) * mm, "end": v(45.56, -54.59) * mm});
            skLineSegment(sketch, "E2.11.12.1", {"start": v(45.56, -54.59) * mm, "end": v(41.23, -47.1) * mm});
            skLineSegment(sketch, "E2.11.12.2", {"start": v(41.23, -47.1) * mm, "end": v(49.9, -47.1) * mm});
            skLineSegment(sketch, "E2.11.13.0", {"start": v(49.9, -62.1) * mm, "end": v(45.56, -69.59) * mm});
            skLineSegment(sketch, "E2.11.13.1", {"start": v(45.56, -69.59) * mm, "end": v(41.23, -62.1) * mm});
            skLineSegment(sketch, "E2.11.13.2", {"start": v(41.23, -62.1) * mm, "end": v(49.9, -62.1) * mm});
            skLineSegment(sketch, "E2.11.14.0", {"start": v(49.9, -77.1) * mm, "end": v(45.56, -84.59) * mm});
            skLineSegment(sketch, "E2.11.14.1", {"start": v(45.56, -84.59) * mm, "end": v(41.23, -77.1) * mm});
            skLineSegment(sketch, "E2.11.14.2", {"start": v(41.23, -77.1) * mm, "end": v(49.9, -77.1) * mm});
            skLineSegment(sketch, "E2.11.15.0", {"start": v(49.9, -92.1) * mm, "end": v(45.56, -99.59) * mm});
            skLineSegment(sketch, "E2.11.15.1", {"start": v(45.56, -99.59) * mm, "end": v(41.23, -92.1) * mm});
            skLineSegment(sketch, "E2.11.15.2", {"start": v(41.23, -92.1) * mm, "end": v(49.9, -92.1) * mm});
            skLineSegment(sketch, "E2.11.16.0", {"start": v(49.9, -107.1) * mm, "end": v(45.56, -114.59) * mm});
            skLineSegment(sketch, "E2.11.16.1", {"start": v(45.56, -114.59) * mm, "end": v(41.23, -107.1) * mm});
            skLineSegment(sketch, "E2.11.16.2", {"start": v(41.23, -107.1) * mm, "end": v(49.9, -107.1) * mm});
            skLineSegment(sketch, "E2.12.0.0", {"start": v(64.9, 132.9) * mm, "end": v(60.56, 125.41) * mm});
            skLineSegment(sketch, "E2.12.0.1", {"start": v(60.56, 125.41) * mm, "end": v(56.23, 132.9) * mm});
            skLineSegment(sketch, "E2.12.0.2", {"start": v(56.23, 132.9) * mm, "end": v(64.9, 132.9) * mm});
            skLineSegment(sketch, "E2.12.1.0", {"start": v(64.9, 117.9) * mm, "end": v(60.56, 110.41) * mm});
            skLineSegment(sketch, "E2.12.1.1", {"start": v(60.56, 110.41) * mm, "end": v(56.23, 117.9) * mm});
            skLineSegment(sketch, "E2.12.1.2", {"start": v(56.23, 117.9) * mm, "end": v(64.9, 117.9) * mm});
            skLineSegment(sketch, "E2.12.2.0", {"start": v(64.9, 102.9) * mm, "end": v(60.56, 95.41) * mm});
            skLineSegment(sketch, "E2.12.2.1", {"start": v(60.56, 95.41) * mm, "end": v(56.23, 102.9) * mm});
            skLineSegment(sketch, "E2.12.2.2", {"start": v(56.23, 102.9) * mm, "end": v(64.9, 102.9) * mm});
            skLineSegment(sketch, "E2.12.3.0", {"start": v(64.9, 87.9) * mm, "end": v(60.56, 80.41) * mm});
            skLineSegment(sketch, "E2.12.3.1", {"start": v(60.56, 80.41) * mm, "end": v(56.23, 87.9) * mm});
            skLineSegment(sketch, "E2.12.3.2", {"start": v(56.23, 87.9) * mm, "end": v(64.9, 87.9) * mm});
            skLineSegment(sketch, "E2.12.4.0", {"start": v(64.9, 72.9) * mm, "end": v(60.56, 65.41) * mm});
            skLineSegment(sketch, "E2.12.4.1", {"start": v(60.56, 65.41) * mm, "end": v(56.23, 72.9) * mm});
            skLineSegment(sketch, "E2.12.4.2", {"start": v(56.23, 72.9) * mm, "end": v(64.9, 72.9) * mm});
            skLineSegment(sketch, "E2.12.5.0", {"start": v(64.9, 57.9) * mm, "end": v(60.56, 50.41) * mm});
            skLineSegment(sketch, "E2.12.5.1", {"start": v(60.56, 50.41) * mm, "end": v(56.23, 57.9) * mm});
            skLineSegment(sketch, "E2.12.5.2", {"start": v(56.23, 57.9) * mm, "end": v(64.9, 57.9) * mm});
            skLineSegment(sketch, "E2.12.6.0", {"start": v(64.9, 42.9) * mm, "end": v(60.56, 35.41) * mm});
            skLineSegment(sketch, "E2.12.6.1", {"start": v(60.56, 35.41) * mm, "end": v(56.23, 42.9) * mm});
            skLineSegment(sketch, "E2.12.6.2", {"start": v(56.23, 42.9) * mm, "end": v(64.9, 42.9) * mm});
            skLineSegment(sketch, "E2.12.7.0", {"start": v(64.9, 27.9) * mm, "end": v(60.56, 20.41) * mm});
            skLineSegment(sketch, "E2.12.7.1", {"start": v(60.56, 20.41) * mm, "end": v(56.23, 27.9) * mm});
            skLineSegment(sketch, "E2.12.7.2", {"start": v(56.23, 27.9) * mm, "end": v(64.9, 27.9) * mm});
            skLineSegment(sketch, "E2.12.8.0", {"start": v(64.9, 12.9) * mm, "end": v(60.56, 5.41) * mm});
            skLineSegment(sketch, "E2.12.8.1", {"start": v(60.56, 5.41) * mm, "end": v(56.23, 12.9) * mm});
            skLineSegment(sketch, "E2.12.8.2", {"start": v(56.23, 12.9) * mm, "end": v(64.9, 12.9) * mm});
            skLineSegment(sketch, "E2.12.9.0", {"start": v(64.9, -2.1) * mm, "end": v(60.56, -9.59) * mm});
            skLineSegment(sketch, "E2.12.9.1", {"start": v(60.56, -9.59) * mm, "end": v(56.23, -2.1) * mm});
            skLineSegment(sketch, "E2.12.9.2", {"start": v(56.23, -2.1) * mm, "end": v(64.9, -2.1) * mm});
            skLineSegment(sketch, "E2.12.10.0", {"start": v(64.9, -17.1) * mm, "end": v(60.56, -24.59) * mm});
            skLineSegment(sketch, "E2.12.10.1", {"start": v(60.56, -24.59) * mm, "end": v(56.23, -17.1) * mm});
            skLineSegment(sketch, "E2.12.10.2", {"start": v(56.23, -17.1) * mm, "end": v(64.9, -17.1) * mm});
            skLineSegment(sketch, "E2.12.11.0", {"start": v(64.9, -32.1) * mm, "end": v(60.56, -39.59) * mm});
            skLineSegment(sketch, "E2.12.11.1", {"start": v(60.56, -39.59) * mm, "end": v(56.23, -32.1) * mm});
            skLineSegment(sketch, "E2.12.11.2", {"start": v(56.23, -32.1) * mm, "end": v(64.9, -32.1) * mm});
            skLineSegment(sketch, "E2.12.12.0", {"start": v(64.9, -47.1) * mm, "end": v(60.56, -54.59) * mm});
            skLineSegment(sketch, "E2.12.12.1", {"start": v(60.56, -54.59) * mm, "end": v(56.23, -47.1) * mm});
            skLineSegment(sketch, "E2.12.12.2", {"start": v(56.23, -47.1) * mm, "end": v(64.9, -47.1) * mm});
            skLineSegment(sketch, "E2.12.13.0", {"start": v(64.9, -62.1) * mm, "end": v(60.56, -69.59) * mm});
            skLineSegment(sketch, "E2.12.13.1", {"start": v(60.56, -69.59) * mm, "end": v(56.23, -62.1) * mm});
            skLineSegment(sketch, "E2.12.13.2", {"start": v(56.23, -62.1) * mm, "end": v(64.9, -62.1) * mm});
            skLineSegment(sketch, "E2.12.14.0", {"start": v(64.9, -77.1) * mm, "end": v(60.56, -84.59) * mm});
            skLineSegment(sketch, "E2.12.14.1", {"start": v(60.56, -84.59) * mm, "end": v(56.23, -77.1) * mm});
            skLineSegment(sketch, "E2.12.14.2", {"start": v(56.23, -77.1) * mm, "end": v(64.9, -77.1) * mm});
            skLineSegment(sketch, "E2.12.15.0", {"start": v(64.9, -92.1) * mm, "end": v(60.56, -99.59) * mm});
            skLineSegment(sketch, "E2.12.15.1", {"start": v(60.56, -99.59) * mm, "end": v(56.23, -92.1) * mm});
            skLineSegment(sketch, "E2.12.15.2", {"start": v(56.23, -92.1) * mm, "end": v(64.9, -92.1) * mm});
            skLineSegment(sketch, "E2.12.16.0", {"start": v(64.9, -107.1) * mm, "end": v(60.56, -114.59) * mm});
            skLineSegment(sketch, "E2.12.16.1", {"start": v(60.56, -114.59) * mm, "end": v(56.23, -107.1) * mm});
            skLineSegment(sketch, "E2.12.16.2", {"start": v(56.23, -107.1) * mm, "end": v(64.9, -107.1) * mm});
            skLineSegment(sketch, "E2.13.0.0", {"start": v(79.9, 132.9) * mm, "end": v(75.56, 125.41) * mm});
            skLineSegment(sketch, "E2.13.0.1", {"start": v(75.56, 125.41) * mm, "end": v(71.23, 132.9) * mm});
            skLineSegment(sketch, "E2.13.0.2", {"start": v(71.23, 132.9) * mm, "end": v(79.9, 132.9) * mm});
            skLineSegment(sketch, "E2.13.1.0", {"start": v(79.9, 117.9) * mm, "end": v(75.56, 110.41) * mm});
            skLineSegment(sketch, "E2.13.1.1", {"start": v(75.56, 110.41) * mm, "end": v(71.23, 117.9) * mm});
            skLineSegment(sketch, "E2.13.1.2", {"start": v(71.23, 117.9) * mm, "end": v(79.9, 117.9) * mm});
            skLineSegment(sketch, "E2.13.2.0", {"start": v(79.9, 102.9) * mm, "end": v(75.56, 95.41) * mm});
            skLineSegment(sketch, "E2.13.2.1", {"start": v(75.56, 95.41) * mm, "end": v(71.23, 102.9) * mm});
            skLineSegment(sketch, "E2.13.2.2", {"start": v(71.23, 102.9) * mm, "end": v(79.9, 102.9) * mm});
            skLineSegment(sketch, "E2.13.3.0", {"start": v(79.9, 87.9) * mm, "end": v(75.56, 80.41) * mm});
            skLineSegment(sketch, "E2.13.3.1", {"start": v(75.56, 80.41) * mm, "end": v(71.23, 87.9) * mm});
            skLineSegment(sketch, "E2.13.3.2", {"start": v(71.23, 87.9) * mm, "end": v(79.9, 87.9) * mm});
            skLineSegment(sketch, "E2.13.4.0", {"start": v(79.9, 72.9) * mm, "end": v(75.56, 65.41) * mm});
            skLineSegment(sketch, "E2.13.4.1", {"start": v(75.56, 65.41) * mm, "end": v(71.23, 72.9) * mm});
            skLineSegment(sketch, "E2.13.4.2", {"start": v(71.23, 72.9) * mm, "end": v(79.9, 72.9) * mm});
            skLineSegment(sketch, "E2.13.5.0", {"start": v(79.9, 57.9) * mm, "end": v(75.56, 50.41) * mm});
            skLineSegment(sketch, "E2.13.5.1", {"start": v(75.56, 50.41) * mm, "end": v(71.23, 57.9) * mm});
            skLineSegment(sketch, "E2.13.5.2", {"start": v(71.23, 57.9) * mm, "end": v(79.9, 57.9) * mm});
            skLineSegment(sketch, "E2.13.6.0", {"start": v(79.9, 42.9) * mm, "end": v(75.56, 35.41) * mm});
            skLineSegment(sketch, "E2.13.6.1", {"start": v(75.56, 35.41) * mm, "end": v(71.23, 42.9) * mm});
            skLineSegment(sketch, "E2.13.6.2", {"start": v(71.23, 42.9) * mm, "end": v(79.9, 42.9) * mm});
            skLineSegment(sketch, "E2.13.7.0", {"start": v(79.9, 27.9) * mm, "end": v(75.56, 20.41) * mm});
            skLineSegment(sketch, "E2.13.7.1", {"start": v(75.56, 20.41) * mm, "end": v(71.23, 27.9) * mm});
            skLineSegment(sketch, "E2.13.7.2", {"start": v(71.23, 27.9) * mm, "end": v(79.9, 27.9) * mm});
            skLineSegment(sketch, "E2.13.8.0", {"start": v(79.9, 12.9) * mm, "end": v(75.56, 5.41) * mm});
            skLineSegment(sketch, "E2.13.8.1", {"start": v(75.56, 5.41) * mm, "end": v(71.23, 12.9) * mm});
            skLineSegment(sketch, "E2.13.8.2", {"start": v(71.23, 12.9) * mm, "end": v(79.9, 12.9) * mm});
            skLineSegment(sketch, "E2.13.9.0", {"start": v(79.9, -2.1) * mm, "end": v(75.56, -9.59) * mm});
            skLineSegment(sketch, "E2.13.9.1", {"start": v(75.56, -9.59) * mm, "end": v(71.23, -2.1) * mm});
            skLineSegment(sketch, "E2.13.9.2", {"start": v(71.23, -2.1) * mm, "end": v(79.9, -2.1) * mm});
            skLineSegment(sketch, "E2.13.10.0", {"start": v(79.9, -17.1) * mm, "end": v(75.56, -24.59) * mm});
            skLineSegment(sketch, "E2.13.10.1", {"start": v(75.56, -24.59) * mm, "end": v(71.23, -17.1) * mm});
            skLineSegment(sketch, "E2.13.10.2", {"start": v(71.23, -17.1) * mm, "end": v(79.9, -17.1) * mm});
            skLineSegment(sketch, "E2.13.11.0", {"start": v(79.9, -32.1) * mm, "end": v(75.56, -39.59) * mm});
            skLineSegment(sketch, "E2.13.11.1", {"start": v(75.56, -39.59) * mm, "end": v(71.23, -32.1) * mm});
            skLineSegment(sketch, "E2.13.11.2", {"start": v(71.23, -32.1) * mm, "end": v(79.9, -32.1) * mm});
            skLineSegment(sketch, "E2.13.12.0", {"start": v(79.9, -47.1) * mm, "end": v(75.56, -54.59) * mm});
            skLineSegment(sketch, "E2.13.12.1", {"start": v(75.56, -54.59) * mm, "end": v(71.23, -47.1) * mm});
            skLineSegment(sketch, "E2.13.12.2", {"start": v(71.23, -47.1) * mm, "end": v(79.9, -47.1) * mm});
            skLineSegment(sketch, "E2.13.13.0", {"start": v(79.9, -62.1) * mm, "end": v(75.56, -69.59) * mm});
            skLineSegment(sketch, "E2.13.13.1", {"start": v(75.56, -69.59) * mm, "end": v(71.23, -62.1) * mm});
            skLineSegment(sketch, "E2.13.13.2", {"start": v(71.23, -62.1) * mm, "end": v(79.9, -62.1) * mm});
            skLineSegment(sketch, "E2.13.14.0", {"start": v(79.9, -77.1) * mm, "end": v(75.56, -84.59) * mm});
            skLineSegment(sketch, "E2.13.14.1", {"start": v(75.56, -84.59) * mm, "end": v(71.23, -77.1) * mm});
            skLineSegment(sketch, "E2.13.14.2", {"start": v(71.23, -77.1) * mm, "end": v(79.9, -77.1) * mm});
            skLineSegment(sketch, "E2.13.15.0", {"start": v(79.9, -92.1) * mm, "end": v(75.56, -99.59) * mm});
            skLineSegment(sketch, "E2.13.15.1", {"start": v(75.56, -99.59) * mm, "end": v(71.23, -92.1) * mm});
            skLineSegment(sketch, "E2.13.15.2", {"start": v(71.23, -92.1) * mm, "end": v(79.9, -92.1) * mm});
            skLineSegment(sketch, "E2.13.16.0", {"start": v(79.9, -107.1) * mm, "end": v(75.56, -114.59) * mm});
            skLineSegment(sketch, "E2.13.16.1", {"start": v(75.56, -114.59) * mm, "end": v(71.23, -107.1) * mm});
            skLineSegment(sketch, "E2.13.16.2", {"start": v(71.23, -107.1) * mm, "end": v(79.9, -107.1) * mm});
            skLineSegment(sketch, "E2.14.0.0", {"start": v(94.9, 132.9) * mm, "end": v(90.56, 125.41) * mm});
            skLineSegment(sketch, "E2.14.0.1", {"start": v(90.56, 125.41) * mm, "end": v(86.23, 132.9) * mm});
            skLineSegment(sketch, "E2.14.0.2", {"start": v(86.23, 132.9) * mm, "end": v(94.9, 132.9) * mm});
            skLineSegment(sketch, "E2.14.1.0", {"start": v(94.9, 117.9) * mm, "end": v(90.56, 110.41) * mm});
            skLineSegment(sketch, "E2.14.1.1", {"start": v(90.56, 110.41) * mm, "end": v(86.23, 117.9) * mm});
            skLineSegment(sketch, "E2.14.1.2", {"start": v(86.23, 117.9) * mm, "end": v(94.9, 117.9) * mm});
            skLineSegment(sketch, "E2.14.2.0", {"start": v(94.9, 102.9) * mm, "end": v(90.56, 95.41) * mm});
            skLineSegment(sketch, "E2.14.2.1", {"start": v(90.56, 95.41) * mm, "end": v(86.23, 102.9) * mm});
            skLineSegment(sketch, "E2.14.2.2", {"start": v(86.23, 102.9) * mm, "end": v(94.9, 102.9) * mm});
            skLineSegment(sketch, "E2.14.3.0", {"start": v(94.9, 87.9) * mm, "end": v(90.56, 80.41) * mm});
            skLineSegment(sketch, "E2.14.3.1", {"start": v(90.56, 80.41) * mm, "end": v(86.23, 87.9) * mm});
            skLineSegment(sketch, "E2.14.3.2", {"start": v(86.23, 87.9) * mm, "end": v(94.9, 87.9) * mm});
            skLineSegment(sketch, "E2.14.4.0", {"start": v(94.9, 72.9) * mm, "end": v(90.56, 65.41) * mm});
            skLineSegment(sketch, "E2.14.4.1", {"start": v(90.56, 65.41) * mm, "end": v(86.23, 72.9) * mm});
            skLineSegment(sketch, "E2.14.4.2", {"start": v(86.23, 72.9) * mm, "end": v(94.9, 72.9) * mm});
            skLineSegment(sketch, "E2.14.5.0", {"start": v(94.9, 57.9) * mm, "end": v(90.56, 50.41) * mm});
            skLineSegment(sketch, "E2.14.5.1", {"start": v(90.56, 50.41) * mm, "end": v(86.23, 57.9) * mm});
            skLineSegment(sketch, "E2.14.5.2", {"start": v(86.23, 57.9) * mm, "end": v(94.9, 57.9) * mm});
            skLineSegment(sketch, "E2.14.6.0", {"start": v(94.9, 42.9) * mm, "end": v(90.56, 35.41) * mm});
            skLineSegment(sketch, "E2.14.6.1", {"start": v(90.56, 35.41) * mm, "end": v(86.23, 42.9) * mm});
            skLineSegment(sketch, "E2.14.6.2", {"start": v(86.23, 42.9) * mm, "end": v(94.9, 42.9) * mm});
            skLineSegment(sketch, "E2.14.7.0", {"start": v(94.9, 27.9) * mm, "end": v(90.56, 20.41) * mm});
            skLineSegment(sketch, "E2.14.7.1", {"start": v(90.56, 20.41) * mm, "end": v(86.23, 27.9) * mm});
            skLineSegment(sketch, "E2.14.7.2", {"start": v(86.23, 27.9) * mm, "end": v(94.9, 27.9) * mm});
            skLineSegment(sketch, "E2.14.8.0", {"start": v(94.9, 12.9) * mm, "end": v(90.56, 5.41) * mm});
            skLineSegment(sketch, "E2.14.8.1", {"start": v(90.56, 5.41) * mm, "end": v(86.23, 12.9) * mm});
            skLineSegment(sketch, "E2.14.8.2", {"start": v(86.23, 12.9) * mm, "end": v(94.9, 12.9) * mm});
            skLineSegment(sketch, "E2.14.9.0", {"start": v(94.9, -2.1) * mm, "end": v(90.56, -9.59) * mm});
            skLineSegment(sketch, "E2.14.9.1", {"start": v(90.56, -9.59) * mm, "end": v(86.23, -2.1) * mm});
            skLineSegment(sketch, "E2.14.9.2", {"start": v(86.23, -2.1) * mm, "end": v(94.9, -2.1) * mm});
            skLineSegment(sketch, "E2.14.10.0", {"start": v(94.9, -17.1) * mm, "end": v(90.56, -24.59) * mm});
            skLineSegment(sketch, "E2.14.10.1", {"start": v(90.56, -24.59) * mm, "end": v(86.23, -17.1) * mm});
            skLineSegment(sketch, "E2.14.10.2", {"start": v(86.23, -17.1) * mm, "end": v(94.9, -17.1) * mm});
            skLineSegment(sketch, "E2.14.11.0", {"start": v(94.9, -32.1) * mm, "end": v(90.56, -39.59) * mm});
            skLineSegment(sketch, "E2.14.11.1", {"start": v(90.56, -39.59) * mm, "end": v(86.23, -32.1) * mm});
            skLineSegment(sketch, "E2.14.11.2", {"start": v(86.23, -32.1) * mm, "end": v(94.9, -32.1) * mm});
            skLineSegment(sketch, "E2.14.12.0", {"start": v(94.9, -47.1) * mm, "end": v(90.56, -54.59) * mm});
            skLineSegment(sketch, "E2.14.12.1", {"start": v(90.56, -54.59) * mm, "end": v(86.23, -47.1) * mm});
            skLineSegment(sketch, "E2.14.12.2", {"start": v(86.23, -47.1) * mm, "end": v(94.9, -47.1) * mm});
            skLineSegment(sketch, "E2.14.13.0", {"start": v(94.9, -62.1) * mm, "end": v(90.56, -69.59) * mm});
            skLineSegment(sketch, "E2.14.13.1", {"start": v(90.56, -69.59) * mm, "end": v(86.23, -62.1) * mm});
            skLineSegment(sketch, "E2.14.13.2", {"start": v(86.23, -62.1) * mm, "end": v(94.9, -62.1) * mm});
            skLineSegment(sketch, "E2.14.14.0", {"start": v(94.9, -77.1) * mm, "end": v(90.56, -84.59) * mm});
            skLineSegment(sketch, "E2.14.14.1", {"start": v(90.56, -84.59) * mm, "end": v(86.23, -77.1) * mm});
            skLineSegment(sketch, "E2.14.14.2", {"start": v(86.23, -77.1) * mm, "end": v(94.9, -77.1) * mm});
            skLineSegment(sketch, "E2.14.15.0", {"start": v(94.9, -92.1) * mm, "end": v(90.56, -99.59) * mm});
            skLineSegment(sketch, "E2.14.15.1", {"start": v(90.56, -99.59) * mm, "end": v(86.23, -92.1) * mm});
            skLineSegment(sketch, "E2.14.15.2", {"start": v(86.23, -92.1) * mm, "end": v(94.9, -92.1) * mm});
            skLineSegment(sketch, "E2.14.16.0", {"start": v(94.9, -107.1) * mm, "end": v(90.56, -114.59) * mm});
            skLineSegment(sketch, "E2.14.16.1", {"start": v(90.56, -114.59) * mm, "end": v(86.23, -107.1) * mm});
            skLineSegment(sketch, "E2.14.16.2", {"start": v(86.23, -107.1) * mm, "end": v(94.9, -107.1) * mm});
            skLineSegment(sketch, "E2.15.0.0", {"start": v(109.9, 132.9) * mm, "end": v(105.56, 125.41) * mm});
            skLineSegment(sketch, "E2.15.0.1", {"start": v(105.56, 125.41) * mm, "end": v(101.23, 132.9) * mm});
            skLineSegment(sketch, "E2.15.0.2", {"start": v(101.23, 132.9) * mm, "end": v(109.9, 132.9) * mm});
            skLineSegment(sketch, "E2.15.1.0", {"start": v(109.9, 117.9) * mm, "end": v(105.56, 110.41) * mm});
            skLineSegment(sketch, "E2.15.1.1", {"start": v(105.56, 110.41) * mm, "end": v(101.23, 117.9) * mm});
            skLineSegment(sketch, "E2.15.1.2", {"start": v(101.23, 117.9) * mm, "end": v(109.9, 117.9) * mm});
            skLineSegment(sketch, "E2.15.2.0", {"start": v(109.9, 102.9) * mm, "end": v(105.56, 95.41) * mm});
            skLineSegment(sketch, "E2.15.2.1", {"start": v(105.56, 95.41) * mm, "end": v(101.23, 102.9) * mm});
            skLineSegment(sketch, "E2.15.2.2", {"start": v(101.23, 102.9) * mm, "end": v(109.9, 102.9) * mm});
            skLineSegment(sketch, "E2.15.3.0", {"start": v(109.9, 87.9) * mm, "end": v(105.56, 80.41) * mm});
            skLineSegment(sketch, "E2.15.3.1", {"start": v(105.56, 80.41) * mm, "end": v(101.23, 87.9) * mm});
            skLineSegment(sketch, "E2.15.3.2", {"start": v(101.23, 87.9) * mm, "end": v(109.9, 87.9) * mm});
            skLineSegment(sketch, "E2.15.4.0", {"start": v(109.9, 72.9) * mm, "end": v(105.56, 65.41) * mm});
            skLineSegment(sketch, "E2.15.4.1", {"start": v(105.56, 65.41) * mm, "end": v(101.23, 72.9) * mm});
            skLineSegment(sketch, "E2.15.4.2", {"start": v(101.23, 72.9) * mm, "end": v(109.9, 72.9) * mm});
            skLineSegment(sketch, "E2.15.5.0", {"start": v(109.9, 57.9) * mm, "end": v(105.56, 50.41) * mm});
            skLineSegment(sketch, "E2.15.5.1", {"start": v(105.56, 50.41) * mm, "end": v(101.23, 57.9) * mm});
            skLineSegment(sketch, "E2.15.5.2", {"start": v(101.23, 57.9) * mm, "end": v(109.9, 57.9) * mm});
            skLineSegment(sketch, "E2.15.6.0", {"start": v(109.9, 42.9) * mm, "end": v(105.56, 35.41) * mm});
            skLineSegment(sketch, "E2.15.6.1", {"start": v(105.56, 35.41) * mm, "end": v(101.23, 42.9) * mm});
            skLineSegment(sketch, "E2.15.6.2", {"start": v(101.23, 42.9) * mm, "end": v(109.9, 42.9) * mm});
            skLineSegment(sketch, "E2.15.7.0", {"start": v(109.9, 27.9) * mm, "end": v(105.56, 20.41) * mm});
            skLineSegment(sketch, "E2.15.7.1", {"start": v(105.56, 20.41) * mm, "end": v(101.23, 27.9) * mm});
            skLineSegment(sketch, "E2.15.7.2", {"start": v(101.23, 27.9) * mm, "end": v(109.9, 27.9) * mm});
            skLineSegment(sketch, "E2.15.8.0", {"start": v(109.9, 12.9) * mm, "end": v(105.56, 5.41) * mm});
            skLineSegment(sketch, "E2.15.8.1", {"start": v(105.56, 5.41) * mm, "end": v(101.23, 12.9) * mm});
            skLineSegment(sketch, "E2.15.8.2", {"start": v(101.23, 12.9) * mm, "end": v(109.9, 12.9) * mm});
            skLineSegment(sketch, "E2.15.9.0", {"start": v(109.9, -2.1) * mm, "end": v(105.56, -9.59) * mm});
            skLineSegment(sketch, "E2.15.9.1", {"start": v(105.56, -9.59) * mm, "end": v(101.23, -2.1) * mm});
            skLineSegment(sketch, "E2.15.9.2", {"start": v(101.23, -2.1) * mm, "end": v(109.9, -2.1) * mm});
            skLineSegment(sketch, "E2.15.10.0", {"start": v(109.9, -17.1) * mm, "end": v(105.56, -24.59) * mm});
            skLineSegment(sketch, "E2.15.10.1", {"start": v(105.56, -24.59) * mm, "end": v(101.23, -17.1) * mm});
            skLineSegment(sketch, "E2.15.10.2", {"start": v(101.23, -17.1) * mm, "end": v(109.9, -17.1) * mm});
            skLineSegment(sketch, "E2.15.11.0", {"start": v(109.9, -32.1) * mm, "end": v(105.56, -39.59) * mm});
            skLineSegment(sketch, "E2.15.11.1", {"start": v(105.56, -39.59) * mm, "end": v(101.23, -32.1) * mm});
            skLineSegment(sketch, "E2.15.11.2", {"start": v(101.23, -32.1) * mm, "end": v(109.9, -32.1) * mm});
            skLineSegment(sketch, "E2.15.12.0", {"start": v(109.9, -47.1) * mm, "end": v(105.56, -54.59) * mm});
            skLineSegment(sketch, "E2.15.12.1", {"start": v(105.56, -54.59) * mm, "end": v(101.23, -47.1) * mm});
            skLineSegment(sketch, "E2.15.12.2", {"start": v(101.23, -47.1) * mm, "end": v(109.9, -47.1) * mm});
            skLineSegment(sketch, "E2.15.13.0", {"start": v(109.9, -62.1) * mm, "end": v(105.56, -69.59) * mm});
            skLineSegment(sketch, "E2.15.13.1", {"start": v(105.56, -69.59) * mm, "end": v(101.23, -62.1) * mm});
            skLineSegment(sketch, "E2.15.13.2", {"start": v(101.23, -62.1) * mm, "end": v(109.9, -62.1) * mm});
            skLineSegment(sketch, "E2.15.14.0", {"start": v(109.9, -77.1) * mm, "end": v(105.56, -84.59) * mm});
            skLineSegment(sketch, "E2.15.14.1", {"start": v(105.56, -84.59) * mm, "end": v(101.23, -77.1) * mm});
            skLineSegment(sketch, "E2.15.14.2", {"start": v(101.23, -77.1) * mm, "end": v(109.9, -77.1) * mm});
            skLineSegment(sketch, "E2.15.15.0", {"start": v(109.9, -92.1) * mm, "end": v(105.56, -99.59) * mm});
            skLineSegment(sketch, "E2.15.15.1", {"start": v(105.56, -99.59) * mm, "end": v(101.23, -92.1) * mm});
            skLineSegment(sketch, "E2.15.15.2", {"start": v(101.23, -92.1) * mm, "end": v(109.9, -92.1) * mm});
            skLineSegment(sketch, "E2.15.16.0", {"start": v(109.9, -107.1) * mm, "end": v(105.56, -114.59) * mm});
            skLineSegment(sketch, "E2.15.16.1", {"start": v(105.56, -114.59) * mm, "end": v(101.23, -107.1) * mm});
            skLineSegment(sketch, "E2.15.16.2", {"start": v(101.23, -107.1) * mm, "end": v(109.9, -107.1) * mm});
            skLineSegment(sketch, "E2.16.0.0", {"start": v(124.9, 132.9) * mm, "end": v(120.56, 125.41) * mm});
            skLineSegment(sketch, "E2.16.0.1", {"start": v(120.56, 125.41) * mm, "end": v(116.23, 132.9) * mm});
            skLineSegment(sketch, "E2.16.0.2", {"start": v(116.23, 132.9) * mm, "end": v(124.9, 132.9) * mm});
            skLineSegment(sketch, "E2.16.1.0", {"start": v(124.9, 117.9) * mm, "end": v(120.56, 110.41) * mm});
            skLineSegment(sketch, "E2.16.1.1", {"start": v(120.56, 110.41) * mm, "end": v(116.23, 117.9) * mm});
            skLineSegment(sketch, "E2.16.1.2", {"start": v(116.23, 117.9) * mm, "end": v(124.9, 117.9) * mm});
            skLineSegment(sketch, "E2.16.2.0", {"start": v(124.9, 102.9) * mm, "end": v(120.56, 95.41) * mm});
            skLineSegment(sketch, "E2.16.2.1", {"start": v(120.56, 95.41) * mm, "end": v(116.23, 102.9) * mm});
            skLineSegment(sketch, "E2.16.2.2", {"start": v(116.23, 102.9) * mm, "end": v(124.9, 102.9) * mm});
            skLineSegment(sketch, "E2.16.3.0", {"start": v(124.9, 87.9) * mm, "end": v(120.56, 80.41) * mm});
            skLineSegment(sketch, "E2.16.3.1", {"start": v(120.56, 80.41) * mm, "end": v(116.23, 87.9) * mm});
            skLineSegment(sketch, "E2.16.3.2", {"start": v(116.23, 87.9) * mm, "end": v(124.9, 87.9) * mm});
            skLineSegment(sketch, "E2.16.4.0", {"start": v(124.9, 72.9) * mm, "end": v(120.56, 65.41) * mm});
            skLineSegment(sketch, "E2.16.4.1", {"start": v(120.56, 65.41) * mm, "end": v(116.23, 72.9) * mm});
            skLineSegment(sketch, "E2.16.4.2", {"start": v(116.23, 72.9) * mm, "end": v(124.9, 72.9) * mm});
            skLineSegment(sketch, "E2.16.5.0", {"start": v(124.9, 57.9) * mm, "end": v(120.56, 50.41) * mm});
            skLineSegment(sketch, "E2.16.5.1", {"start": v(120.56, 50.41) * mm, "end": v(116.23, 57.9) * mm});
            skLineSegment(sketch, "E2.16.5.2", {"start": v(116.23, 57.9) * mm, "end": v(124.9, 57.9) * mm});
            skLineSegment(sketch, "E2.16.6.0", {"start": v(124.9, 42.9) * mm, "end": v(120.56, 35.41) * mm});
            skLineSegment(sketch, "E2.16.6.1", {"start": v(120.56, 35.41) * mm, "end": v(116.23, 42.9) * mm});
            skLineSegment(sketch, "E2.16.6.2", {"start": v(116.23, 42.9) * mm, "end": v(124.9, 42.9) * mm});
            skLineSegment(sketch, "E2.16.7.0", {"start": v(124.9, 27.9) * mm, "end": v(120.56, 20.41) * mm});
            skLineSegment(sketch, "E2.16.7.1", {"start": v(120.56, 20.41) * mm, "end": v(116.23, 27.9) * mm});
            skLineSegment(sketch, "E2.16.7.2", {"start": v(116.23, 27.9) * mm, "end": v(124.9, 27.9) * mm});
            skLineSegment(sketch, "E2.16.8.0", {"start": v(124.9, 12.9) * mm, "end": v(120.56, 5.41) * mm});
            skLineSegment(sketch, "E2.16.8.1", {"start": v(120.56, 5.41) * mm, "end": v(116.23, 12.9) * mm});
            skLineSegment(sketch, "E2.16.8.2", {"start": v(116.23, 12.9) * mm, "end": v(124.9, 12.9) * mm});
            skLineSegment(sketch, "E2.16.9.0", {"start": v(124.9, -2.1) * mm, "end": v(120.56, -9.59) * mm});
            skLineSegment(sketch, "E2.16.9.1", {"start": v(120.56, -9.59) * mm, "end": v(116.23, -2.1) * mm});
            skLineSegment(sketch, "E2.16.9.2", {"start": v(116.23, -2.1) * mm, "end": v(124.9, -2.1) * mm});
            skLineSegment(sketch, "E2.16.10.0", {"start": v(124.9, -17.1) * mm, "end": v(120.56, -24.59) * mm});
            skLineSegment(sketch, "E2.16.10.1", {"start": v(120.56, -24.59) * mm, "end": v(116.23, -17.1) * mm});
            skLineSegment(sketch, "E2.16.10.2", {"start": v(116.23, -17.1) * mm, "end": v(124.9, -17.1) * mm});
            skLineSegment(sketch, "E2.16.11.0", {"start": v(124.9, -32.1) * mm, "end": v(120.56, -39.59) * mm});
            skLineSegment(sketch, "E2.16.11.1", {"start": v(120.56, -39.59) * mm, "end": v(116.23, -32.1) * mm});
            skLineSegment(sketch, "E2.16.11.2", {"start": v(116.23, -32.1) * mm, "end": v(124.9, -32.1) * mm});
            skLineSegment(sketch, "E2.16.12.0", {"start": v(124.9, -47.1) * mm, "end": v(120.56, -54.59) * mm});
            skLineSegment(sketch, "E2.16.12.1", {"start": v(120.56, -54.59) * mm, "end": v(116.23, -47.1) * mm});
            skLineSegment(sketch, "E2.16.12.2", {"start": v(116.23, -47.1) * mm, "end": v(124.9, -47.1) * mm});
            skLineSegment(sketch, "E2.16.13.0", {"start": v(124.9, -62.1) * mm, "end": v(120.56, -69.59) * mm});
            skLineSegment(sketch, "E2.16.13.1", {"start": v(120.56, -69.59) * mm, "end": v(116.23, -62.1) * mm});
            skLineSegment(sketch, "E2.16.13.2", {"start": v(116.23, -62.1) * mm, "end": v(124.9, -62.1) * mm});
            skLineSegment(sketch, "E2.16.14.0", {"start": v(124.9, -77.1) * mm, "end": v(120.56, -84.59) * mm});
            skLineSegment(sketch, "E2.16.14.1", {"start": v(120.56, -84.59) * mm, "end": v(116.23, -77.1) * mm});
            skLineSegment(sketch, "E2.16.14.2", {"start": v(116.23, -77.1) * mm, "end": v(124.9, -77.1) * mm});
            skLineSegment(sketch, "E2.16.15.0", {"start": v(124.9, -92.1) * mm, "end": v(120.56, -99.59) * mm});
            skLineSegment(sketch, "E2.16.15.1", {"start": v(120.56, -99.59) * mm, "end": v(116.23, -92.1) * mm});
            skLineSegment(sketch, "E2.16.15.2", {"start": v(116.23, -92.1) * mm, "end": v(124.9, -92.1) * mm});
            skLineSegment(sketch, "E2.16.16.0", {"start": v(124.9, -107.1) * mm, "end": v(120.56, -114.59) * mm});
            skLineSegment(sketch, "E2.16.16.1", {"start": v(120.56, -114.59) * mm, "end": v(116.23, -107.1) * mm});
            skLineSegment(sketch, "E2.16.16.2", {"start": v(116.23, -107.1) * mm, "end": v(124.9, -107.1) * mm});
            skLineSegment(sketch, "E2.direction1", {"start": v(-119.44, 125.41) * mm, "end": v(-104.44, 125.41) * mm, "construction": true});
            skLineSegment(sketch, "E2.direction2", {"start": v(-119.44, 125.41) * mm, "end": v(-119.44, 110.41) * mm, "construction": true});
            skSolve(sketch);
        }
        {
            var Q0;
            Q0=makeQuery(id+"F3.imprint","IMPRINT",FACE,{"disambiguationData":[TD([[makeQuery(id+"F3.imprint","IMPRINT",EDGE,{"derivedFrom":sQuery(id+"F3.wireOp",EDGE,"E2.15.12.0")}),-1.0]])]});
            var Q1;
            Q1=makeQuery(id+"F3.imprint","IMPRINT",FACE,{"disambiguationData":[TD([[makeQuery(id+"F3.imprint","IMPRINT",EDGE,{"derivedFrom":sQuery(id+"F3.wireOp",EDGE,"E2.15.11.0")}),-1.0]])]});
            var Q2;
            Q2=makeQuery(id+"F3.imprint","IMPRINT",FACE,{"disambiguationData":[TD([[makeQuery(id+"F3.imprint","IMPRINT",EDGE,{"derivedFrom":sQuery(id+"F3.wireOp",EDGE,"E2.15.10.0")}),-1.0]])]});
            var Q3;
            Q3=makeQuery(id+"F3.imprint","IMPRINT",FACE,{"disambiguationData":[TD([[makeQuery(id+"F3.imprint","IMPRINT",EDGE,{"derivedFrom":sQuery(id+"F3.wireOp",EDGE,"E2.15.9.0")}),-1.0]])]});
            var Q4;
            Q4=makeQuery(id+"F3.imprint","IMPRINT",FACE,{"disambiguationData":[TD([[makeQuery(id+"F3.imprint","IMPRINT",EDGE,{"derivedFrom":sQuery(id+"F3.wireOp",EDGE,"E2.15.8.0")}),-1.0]])]});
            var Q5;
            Q5=makeQuery(id+"F3.imprint","IMPRINT",FACE,{"disambiguationData":[TD([[makeQuery(id+"F3.imprint","IMPRINT",EDGE,{"derivedFrom":sQuery(id+"F3.wireOp",EDGE,"E2.15.7.0")}),-1.0]])]});
            var Q6;
            Q6=makeQuery(id+"F3.imprint","IMPRINT",FACE,{"disambiguationData":[TD([[makeQuery(id+"F3.imprint","IMPRINT",EDGE,{"derivedFrom":sQuery(id+"F3.wireOp",EDGE,"E2.15.6.0")}),-1.0]])]});
            var Q7;
            Q7=makeQuery(id+"F3.imprint","IMPRINT",FACE,{"disambiguationData":[TD([[makeQuery(id+"F3.imprint","IMPRINT",EDGE,{"derivedFrom":sQuery(id+"F3.wireOp",EDGE,"E2.15.5.0")}),-1.0]])]});
            var Q8;
            Q8=makeQuery(id+"F3.imprint","IMPRINT",FACE,{"disambiguationData":[TD([[makeQuery(id+"F3.imprint","IMPRINT",EDGE,{"derivedFrom":sQuery(id+"F3.wireOp",EDGE,"E2.15.4.0")}),-1.0]])]});
            var Q9;
            Q9=makeQuery(id+"F3.imprint","IMPRINT",FACE,{"disambiguationData":[TD([[makeQuery(id+"F3.imprint","IMPRINT",EDGE,{"derivedFrom":sQuery(id+"F3.wireOp",EDGE,"E2.15.3.0")}),-1.0]])]});
            var Q10;
            Q10=makeQuery(id+"F3.imprint","IMPRINT",FACE,{"disambiguationData":[TD([[makeQuery(id+"F3.imprint","IMPRINT",EDGE,{"derivedFrom":sQuery(id+"F3.wireOp",EDGE,"E2.15.2.0")}),-1.0]])]});
            var Q11;
            Q11=makeQuery(id+"F3.imprint","IMPRINT",FACE,{"disambiguationData":[TD([[makeQuery(id+"F3.imprint","IMPRINT",EDGE,{"derivedFrom":sQuery(id+"F3.wireOp",EDGE,"E2.15.1.0")}),-1.0]])]});
            var Q12;
            Q12=makeQuery(id+"F3.imprint","IMPRINT",FACE,{"disambiguationData":[TD([[makeQuery(id+"F3.imprint","IMPRINT",EDGE,{"derivedFrom":sQuery(id+"F3.wireOp",EDGE,"E2.15.15.0")}),-1.0]])]});
            var Q13;
            Q13=makeQuery(id+"F3.imprint","IMPRINT",FACE,{"disambiguationData":[TD([[makeQuery(id+"F3.imprint","IMPRINT",EDGE,{"derivedFrom":sQuery(id+"F3.wireOp",EDGE,"E2.15.14.0")}),-1.0]])]});
            var Q14;
            Q14=makeQuery(id+"F3.imprint","IMPRINT",FACE,{"disambiguationData":[TD([[makeQuery(id+"F3.imprint","IMPRINT",EDGE,{"derivedFrom":sQuery(id+"F3.wireOp",EDGE,"E2.15.0.0")}),-1.0]])]});
            var Q15;
            Q15=makeQuery(id+"F3.imprint","IMPRINT",FACE,{"disambiguationData":[TD([[makeQuery(id+"F3.imprint","IMPRINT",EDGE,{"derivedFrom":sQuery(id+"F3.wireOp",EDGE,"E2.15.16.0")}),-1.0]])]});
            var Q16;
            Q16=makeQuery(id+"F3.imprint","IMPRINT",FACE,{"disambiguationData":[TD([[makeQuery(id+"F3.imprint","IMPRINT",EDGE,{"derivedFrom":sQuery(id+"F3.wireOp",EDGE,"E2.15.13.0")}),-1.0]])]});
            var Q17;
            Q17=makeQuery(id+"F3.imprint","IMPRINT",FACE,{"disambiguationData":[TD([[makeQuery(id+"F3.imprint","IMPRINT",EDGE,{"derivedFrom":sQuery(id+"F3.wireOp",EDGE,"E2.13.14.0")}),-1.0]])]});
            var Q18;
            Q18=makeQuery(id+"F3.imprint","IMPRINT",FACE,{"disambiguationData":[TD([[makeQuery(id+"F3.imprint","IMPRINT",EDGE,{"derivedFrom":sQuery(id+"F3.wireOp",EDGE,"E2.14.13.0")}),-1.0]])]});
            var Q19;
            Q19=makeQuery(id+"F3.imprint","IMPRINT",FACE,{"disambiguationData":[TD([[makeQuery(id+"F3.imprint","IMPRINT",EDGE,{"derivedFrom":sQuery(id+"F3.wireOp",EDGE,"E2.11.16.0")}),-1.0]])]});
            var Q20;
            Q20=makeQuery(id+"F3.imprint","IMPRINT",FACE,{"disambiguationData":[TD([[makeQuery(id+"F3.imprint","IMPRINT",EDGE,{"derivedFrom":sQuery(id+"F3.wireOp",EDGE,"E2.16.12.0")}),-1.0]])]});
            var Q21;
            Q21=makeQuery(id+"F3.imprint","IMPRINT",FACE,{"disambiguationData":[TD([[makeQuery(id+"F3.imprint","IMPRINT",EDGE,{"derivedFrom":sQuery(id+"F3.wireOp",EDGE,"E2.12.15.0")}),-1.0]])]});
            var Q22;
            Q22=makeQuery(id+"F3.imprint","IMPRINT",FACE,{"disambiguationData":[TD([[makeQuery(id+"F3.imprint","IMPRINT",EDGE,{"derivedFrom":sQuery(id+"F3.wireOp",EDGE,"E2.16.11.0")}),-1.0]])]});
            var Q23;
            Q23=makeQuery(id+"F3.imprint","IMPRINT",FACE,{"disambiguationData":[TD([[makeQuery(id+"F3.imprint","IMPRINT",EDGE,{"derivedFrom":sQuery(id+"F3.wireOp",EDGE,"E2.8.3.0")}),-1.0]])]});
            var Q24;
            Q24=makeQuery(id+"F3.imprint","IMPRINT",FACE,{"disambiguationData":[TD([[makeQuery(id+"F3.imprint","IMPRINT",EDGE,{"derivedFrom":sQuery(id+"F3.wireOp",EDGE,"E2.9.2.0")}),-1.0]])]});
            var Q25;
            Q25=makeQuery(id+"F3.imprint","IMPRINT",FACE,{"disambiguationData":[TD([[makeQuery(id+"F3.imprint","IMPRINT",EDGE,{"derivedFrom":sQuery(id+"F3.wireOp",EDGE,"E2.10.1.0")}),-1.0]])]});
            var Q26;
            Q26=makeQuery(id+"F3.imprint","IMPRINT",FACE,{"disambiguationData":[TD([[makeQuery(id+"F3.imprint","IMPRINT",EDGE,{"derivedFrom":sQuery(id+"F3.wireOp",EDGE,"E2.11.0.0")}),-1.0]])]});
            var Q27;
            Q27=makeQuery(id+"F3.imprint","IMPRINT",FACE,{"disambiguationData":[TD([[makeQuery(id+"F3.imprint","IMPRINT",EDGE,{"derivedFrom":sQuery(id+"F3.wireOp",EDGE,"E2.4.7.0")}),-1.0]])]});
            var Q28;
            Q28=makeQuery(id+"F3.imprint","IMPRINT",FACE,{"disambiguationData":[TD([[makeQuery(id+"F3.imprint","IMPRINT",EDGE,{"derivedFrom":sQuery(id+"F3.wireOp",EDGE,"E2.5.6.0")}),-1.0]])]});
            var Q29;
            Q29=makeQuery(id+"F3.imprint","IMPRINT",FACE,{"disambiguationData":[TD([[makeQuery(id+"F3.imprint","IMPRINT",EDGE,{"derivedFrom":sQuery(id+"F3.wireOp",EDGE,"E2.6.5.0")}),-1.0]])]});
            var Q30;
            Q30=makeQuery(id+"F3.imprint","IMPRINT",FACE,{"disambiguationData":[TD([[makeQuery(id+"F3.imprint","IMPRINT",EDGE,{"derivedFrom":sQuery(id+"F3.wireOp",EDGE,"E2.7.4.0")}),-1.0]])]});
            var Q31;
            Q31=makeQuery(id+"F3.imprint","IMPRINT",FACE,{"disambiguationData":[TD([[makeQuery(id+"F3.imprint","IMPRINT",EDGE,{"derivedFrom":sQuery(id+"F3.wireOp",EDGE,"E2.1.10.0")}),-1.0]])]});
            var Q32;
            Q32=makeQuery(id+"F3.imprint","IMPRINT",FACE,{"disambiguationData":[TD([[makeQuery(id+"F3.imprint","IMPRINT",EDGE,{"derivedFrom":sQuery(id+"F3.wireOp",EDGE,"E2.2.9.0")}),-1.0]])]});
            var Q33;
            Q33=makeQuery(id+"F3.imprint","IMPRINT",FACE,{"disambiguationData":[TD([[makeQuery(id+"F3.imprint","IMPRINT",EDGE,{"derivedFrom":sQuery(id+"F3.wireOp",EDGE,"E2.3.8.0")}),-1.0]])]});
            var Q34;
            Q34=makeQuery(id+"F3.imprint","IMPRINT",FACE,{"disambiguationData":[TD([[makeQuery(id+"F3.imprint","IMPRINT",EDGE,{"derivedFrom":sQuery(id+"F3.wireOp",EDGE,"E2.12.14.0")}),-1.0]])]});
            var Q35;
            Q35=makeQuery(id+"F3.imprint","IMPRINT",FACE,{"disambiguationData":[TD([[makeQuery(id+"F3.imprint","IMPRINT",EDGE,{"derivedFrom":sQuery(id+"F3.wireOp",EDGE,"E2.11.15.0")}),-1.0]])]});
            var Q36;
            Q36=makeQuery(id+"F3.imprint","IMPRINT",FACE,{"disambiguationData":[TD([[makeQuery(id+"F3.imprint","IMPRINT",EDGE,{"derivedFrom":sQuery(id+"F3.wireOp",EDGE,"E2.13.13.0")}),-1.0]])]});
            var Q37;
            Q37=makeQuery(id+"F3.imprint","IMPRINT",FACE,{"disambiguationData":[TD([[makeQuery(id+"F3.imprint","IMPRINT",EDGE,{"derivedFrom":sQuery(id+"F3.wireOp",EDGE,"E2.14.12.0")}),-1.0]])]});
            var Q38;
            Q38=makeQuery(id+"F3.imprint","IMPRINT",FACE,{"disambiguationData":[TD([[makeQuery(id+"F3.imprint","IMPRINT",EDGE,{"derivedFrom":sQuery(id+"F3.wireOp",EDGE,"E2.8.2.0")}),-1.0]])]});
            var Q39;
            Q39=makeQuery(id+"F3.imprint","IMPRINT",FACE,{"disambiguationData":[TD([[makeQuery(id+"F3.imprint","IMPRINT",EDGE,{"derivedFrom":sQuery(id+"F3.wireOp",EDGE,"E2.9.1.0")}),-1.0]])]});
            var Q40;
            Q40=makeQuery(id+"F3.imprint","IMPRINT",FACE,{"disambiguationData":[TD([[makeQuery(id+"F3.imprint","IMPRINT",EDGE,{"derivedFrom":sQuery(id+"F3.wireOp",EDGE,"E2.10.0.0")}),-1.0]])]});
            var Q41;
            Q41=makeQuery(id+"F3.imprint","IMPRINT",FACE,{"disambiguationData":[TD([[makeQuery(id+"F3.imprint","IMPRINT",EDGE,{"derivedFrom":sQuery(id+"F3.wireOp",EDGE,"E2.10.16.0")}),-1.0]])]});
            var Q42;
            Q42=makeQuery(id+"F3.imprint","IMPRINT",FACE,{"disambiguationData":[TD([[makeQuery(id+"F3.imprint","IMPRINT",EDGE,{"derivedFrom":sQuery(id+"F3.wireOp",EDGE,"E2.4.6.0")}),-1.0]])]});
            var Q43;
            Q43=makeQuery(id+"F3.imprint","IMPRINT",FACE,{"disambiguationData":[TD([[makeQuery(id+"F3.imprint","IMPRINT",EDGE,{"derivedFrom":sQuery(id+"F3.wireOp",EDGE,"E2.5.5.0")}),-1.0]])]});
            var Q44;
            Q44=makeQuery(id+"F3.imprint","IMPRINT",FACE,{"disambiguationData":[TD([[makeQuery(id+"F3.imprint","IMPRINT",EDGE,{"derivedFrom":sQuery(id+"F3.wireOp",EDGE,"E2.6.4.0")}),-1.0]])]});
            var Q45;
            Q45=makeQuery(id+"F3.imprint","IMPRINT",FACE,{"disambiguationData":[TD([[makeQuery(id+"F3.imprint","IMPRINT",EDGE,{"derivedFrom":sQuery(id+"F3.wireOp",EDGE,"E2.7.3.0")}),-1.0]])]});
            var Q46;
            Q46=makeQuery(id+"F3.imprint","IMPRINT",FACE,{"disambiguationData":[TD([[makeQuery(id+"F3.imprint","IMPRINT",EDGE,{"derivedFrom":sQuery(id+"F3.wireOp",EDGE,"E2.1.9.0")}),-1.0]])]});
            var Q47;
            Q47=makeQuery(id+"F3.imprint","IMPRINT",FACE,{"disambiguationData":[TD([[makeQuery(id+"F3.imprint","IMPRINT",EDGE,{"derivedFrom":sQuery(id+"F3.wireOp",EDGE,"E2.2.8.0")}),-1.0]])]});
            var Q48;
            Q48=makeQuery(id+"F3.imprint","IMPRINT",FACE,{"disambiguationData":[TD([[makeQuery(id+"F3.imprint","IMPRINT",EDGE,{"derivedFrom":sQuery(id+"F3.wireOp",EDGE,"E2.3.7.0")}),-1.0]])]});
            var Q49;
            Q49=makeQuery(id+"F3.imprint","IMPRINT",FACE,{"disambiguationData":[TD([[makeQuery(id+"F3.imprint","IMPRINT",EDGE,{"derivedFrom":sQuery(id+"F3.wireOp",EDGE,"E2.16.10.0")}),-1.0]])]});
            var Q50;
            Q50=makeQuery(id+"F3.imprint","IMPRINT",FACE,{"disambiguationData":[TD([[makeQuery(id+"F3.imprint","IMPRINT",EDGE,{"derivedFrom":sQuery(id+"F3.wireOp",EDGE,"E2.8.1.0")}),-1.0]])]});
            var Q51;
            Q51=makeQuery(id+"F3.imprint","IMPRINT",FACE,{"disambiguationData":[TD([[makeQuery(id+"F3.imprint","IMPRINT",EDGE,{"derivedFrom":sQuery(id+"F3.wireOp",EDGE,"E2.9.0.0")}),-1.0]])]});
            var Q52;
            Q52=makeQuery(id+"F3.imprint","IMPRINT",FACE,{"disambiguationData":[TD([[makeQuery(id+"F3.imprint","IMPRINT",EDGE,{"derivedFrom":sQuery(id+"F3.wireOp",EDGE,"E2.9.16.0")}),-1.0]])]});
            var Q53;
            Q53=makeQuery(id+"F3.imprint","IMPRINT",FACE,{"disambiguationData":[TD([[makeQuery(id+"F3.imprint","IMPRINT",EDGE,{"derivedFrom":sQuery(id+"F3.wireOp",EDGE,"E2.10.15.0")}),-1.0]])]});
            var Q54;
            Q54=makeQuery(id+"F3.imprint","IMPRINT",FACE,{"disambiguationData":[TD([[makeQuery(id+"F3.imprint","IMPRINT",EDGE,{"derivedFrom":sQuery(id+"F3.wireOp",EDGE,"E2.4.5.0")}),-1.0]])]});
            var Q55;
            Q55=makeQuery(id+"F3.imprint","IMPRINT",FACE,{"disambiguationData":[TD([[makeQuery(id+"F3.imprint","IMPRINT",EDGE,{"derivedFrom":sQuery(id+"F3.wireOp",EDGE,"E2.5.4.0")}),-1.0]])]});
            var Q56;
            Q56=makeQuery(id+"F3.imprint","IMPRINT",FACE,{"disambiguationData":[TD([[makeQuery(id+"F3.imprint","IMPRINT",EDGE,{"derivedFrom":sQuery(id+"F3.wireOp",EDGE,"E2.6.3.0")}),-1.0]])]});
            var Q57;
            Q57=makeQuery(id+"F3.imprint","IMPRINT",FACE,{"disambiguationData":[TD([[makeQuery(id+"F3.imprint","IMPRINT",EDGE,{"derivedFrom":sQuery(id+"F3.wireOp",EDGE,"E2.7.2.0")}),-1.0]])]});
            var Q58;
            Q58=makeQuery(id+"F3.imprint","IMPRINT",FACE,{"disambiguationData":[TD([[makeQuery(id+"F3.imprint","IMPRINT",EDGE,{"derivedFrom":sQuery(id+"F3.wireOp",EDGE,"E2.2.7.0")}),-1.0]])]});
            var Q59;
            Q59=makeQuery(id+"F3.imprint","IMPRINT",FACE,{"disambiguationData":[TD([[makeQuery(id+"F3.imprint","IMPRINT",EDGE,{"derivedFrom":sQuery(id+"F3.wireOp",EDGE,"E2.1.8.0")}),-1.0]])]});
            var Q60;
            Q60=makeQuery(id+"F3.imprint","IMPRINT",FACE,{"disambiguationData":[TD([[makeQuery(id+"F3.imprint","IMPRINT",EDGE,{"derivedFrom":sQuery(id+"F3.wireOp",EDGE,"E2.3.6.0")}),-1.0]])]});
            var Q61;
            Q61=makeQuery(id+"F3.imprint","IMPRINT",FACE,{"disambiguationData":[TD([[makeQuery(id+"F3.imprint","IMPRINT",EDGE,{"derivedFrom":sQuery(id+"F3.wireOp",EDGE,"E2.16.9.0")}),-1.0]])]});
            var Q62;
            Q62=makeQuery(id+"F3.imprint","IMPRINT",FACE,{"disambiguationData":[TD([[makeQuery(id+"F3.imprint","IMPRINT",EDGE,{"derivedFrom":sQuery(id+"F3.wireOp",EDGE,"E2.11.14.0")}),-1.0]])]});
            var Q63;
            Q63=makeQuery(id+"F3.imprint","IMPRINT",FACE,{"disambiguationData":[TD([[makeQuery(id+"F3.imprint","IMPRINT",EDGE,{"derivedFrom":sQuery(id+"F3.wireOp",EDGE,"E2.12.13.0")}),-1.0]])]});
            var Q64;
            Q64=makeQuery(id+"F3.imprint","IMPRINT",FACE,{"disambiguationData":[TD([[makeQuery(id+"F3.imprint","IMPRINT",EDGE,{"derivedFrom":sQuery(id+"F3.wireOp",EDGE,"E2.13.12.0")}),-1.0]])]});
            var Q65;
            Q65=makeQuery(id+"F3.imprint","IMPRINT",FACE,{"disambiguationData":[TD([[makeQuery(id+"F3.imprint","IMPRINT",EDGE,{"derivedFrom":sQuery(id+"F3.wireOp",EDGE,"E2.14.11.0")}),-1.0]])]});
            var Q66;
            Q66=makeQuery(id+"F3.imprint","IMPRINT",FACE,{"disambiguationData":[TD([[makeQuery(id+"F3.imprint","IMPRINT",EDGE,{"derivedFrom":sQuery(id+"F3.wireOp",EDGE,"E2.4.4.0")}),-1.0]])]});
            var Q67;
            Q67=makeQuery(id+"F3.imprint","IMPRINT",FACE,{"disambiguationData":[TD([[makeQuery(id+"F3.imprint","IMPRINT",EDGE,{"derivedFrom":sQuery(id+"F3.wireOp",EDGE,"E2.5.3.0")}),-1.0]])]});
            var Q68;
            Q68=makeQuery(id+"F3.imprint","IMPRINT",FACE,{"disambiguationData":[TD([[makeQuery(id+"F3.imprint","IMPRINT",EDGE,{"derivedFrom":sQuery(id+"F3.wireOp",EDGE,"E2.6.2.0")}),-1.0]])]});
            var Q69;
            Q69=makeQuery(id+"F3.imprint","IMPRINT",FACE,{"disambiguationData":[TD([[makeQuery(id+"F3.imprint","IMPRINT",EDGE,{"derivedFrom":sQuery(id+"F3.wireOp",EDGE,"E2.7.1.0")}),-1.0]])]});
            var Q70;
            Q70=makeQuery(id+"F3.imprint","IMPRINT",FACE,{"disambiguationData":[TD([[makeQuery(id+"F3.imprint","IMPRINT",EDGE,{"derivedFrom":sQuery(id+"F3.wireOp",EDGE,"E2.1.7.0")}),-1.0]])]});
            var Q71;
            Q71=makeQuery(id+"F3.imprint","IMPRINT",FACE,{"disambiguationData":[TD([[makeQuery(id+"F3.imprint","IMPRINT",EDGE,{"derivedFrom":sQuery(id+"F3.wireOp",EDGE,"E2.2.6.0")}),-1.0]])]});
            var Q72;
            Q72=makeQuery(id+"F3.imprint","IMPRINT",FACE,{"disambiguationData":[TD([[makeQuery(id+"F3.imprint","IMPRINT",EDGE,{"derivedFrom":sQuery(id+"F3.wireOp",EDGE,"E2.3.5.0")}),-1.0]])]});
            var Q73;
            Q73=makeQuery(id+"F3.imprint","IMPRINT",FACE,{"disambiguationData":[TD([[makeQuery(id+"F3.imprint","IMPRINT",EDGE,{"derivedFrom":sQuery(id+"F3.wireOp",EDGE,"E2.16.8.0")}),-1.0]])]});
            var Q74;
            Q74=makeQuery(id+"F3.imprint","IMPRINT",FACE,{"disambiguationData":[TD([[makeQuery(id+"F3.imprint","IMPRINT",EDGE,{"derivedFrom":sQuery(id+"F3.wireOp",EDGE,"E2.11.13.0")}),-1.0]])]});
            var Q75;
            Q75=makeQuery(id+"F3.imprint","IMPRINT",FACE,{"disambiguationData":[TD([[makeQuery(id+"F3.imprint","IMPRINT",EDGE,{"derivedFrom":sQuery(id+"F3.wireOp",EDGE,"E2.12.12.0")}),-1.0]])]});
            var Q76;
            Q76=makeQuery(id+"F3.imprint","IMPRINT",FACE,{"disambiguationData":[TD([[makeQuery(id+"F3.imprint","IMPRINT",EDGE,{"derivedFrom":sQuery(id+"F3.wireOp",EDGE,"E2.13.11.0")}),-1.0]])]});
            var Q77;
            Q77=makeQuery(id+"F3.imprint","IMPRINT",FACE,{"disambiguationData":[TD([[makeQuery(id+"F3.imprint","IMPRINT",EDGE,{"derivedFrom":sQuery(id+"F3.wireOp",EDGE,"E2.14.10.0")}),-1.0]])]});
            var Q78;
            Q78=makeQuery(id+"F3.imprint","IMPRINT",FACE,{"disambiguationData":[TD([[makeQuery(id+"F3.imprint","IMPRINT",EDGE,{"derivedFrom":sQuery(id+"F3.wireOp",EDGE,"E2.8.0.0")}),-1.0]])]});
            var Q79;
            Q79=makeQuery(id+"F3.imprint","IMPRINT",FACE,{"disambiguationData":[TD([[makeQuery(id+"F3.imprint","IMPRINT",EDGE,{"derivedFrom":sQuery(id+"F3.wireOp",EDGE,"E2.8.16.0")}),-1.0]])]});
            var Q80;
            Q80=makeQuery(id+"F3.imprint","IMPRINT",FACE,{"disambiguationData":[TD([[makeQuery(id+"F3.imprint","IMPRINT",EDGE,{"derivedFrom":sQuery(id+"F3.wireOp",EDGE,"E2.9.15.0")}),-1.0]])]});
            var Q81;
            Q81=makeQuery(id+"F3.imprint","IMPRINT",FACE,{"disambiguationData":[TD([[makeQuery(id+"F3.imprint","IMPRINT",EDGE,{"derivedFrom":sQuery(id+"F3.wireOp",EDGE,"E2.10.14.0")}),-1.0]])]});
            var Q82;
            Q82=makeQuery(id+"F3.imprint","IMPRINT",FACE,{"disambiguationData":[TD([[makeQuery(id+"F3.imprint","IMPRINT",EDGE,{"derivedFrom":sQuery(id+"F3.wireOp",EDGE,"E2.1.6.0")}),-1.0]])]});
            var Q83;
            Q83=makeQuery(id+"F3.imprint","IMPRINT",FACE,{"disambiguationData":[TD([[makeQuery(id+"F3.imprint","IMPRINT",EDGE,{"derivedFrom":sQuery(id+"F3.wireOp",EDGE,"E2.2.5.0")}),-1.0]])]});
            var Q84;
            Q84=makeQuery(id+"F3.imprint","IMPRINT",FACE,{"disambiguationData":[TD([[makeQuery(id+"F3.imprint","IMPRINT",EDGE,{"derivedFrom":sQuery(id+"F3.wireOp",EDGE,"E2.3.4.0")}),-1.0]])]});
            var Q85;
            Q85=makeQuery(id+"F3.imprint","IMPRINT",FACE,{"disambiguationData":[TD([[makeQuery(id+"F3.imprint","IMPRINT",EDGE,{"derivedFrom":sQuery(id+"F3.wireOp",EDGE,"E2.16.7.0")}),-1.0]])]});
            var Q86;
            Q86=makeQuery(id+"F3.imprint","IMPRINT",FACE,{"disambiguationData":[TD([[makeQuery(id+"F3.imprint","IMPRINT",EDGE,{"derivedFrom":sQuery(id+"F3.wireOp",EDGE,"E2.11.12.0")}),-1.0]])]});
            var Q87;
            Q87=makeQuery(id+"F3.imprint","IMPRINT",FACE,{"disambiguationData":[TD([[makeQuery(id+"F3.imprint","IMPRINT",EDGE,{"derivedFrom":sQuery(id+"F3.wireOp",EDGE,"E2.12.11.0")}),-1.0]])]});
            var Q88;
            Q88=makeQuery(id+"F3.imprint","IMPRINT",FACE,{"disambiguationData":[TD([[makeQuery(id+"F3.imprint","IMPRINT",EDGE,{"derivedFrom":sQuery(id+"F3.wireOp",EDGE,"E2.13.10.0")}),-1.0]])]});
            var Q89;
            Q89=makeQuery(id+"F3.imprint","IMPRINT",FACE,{"disambiguationData":[TD([[makeQuery(id+"F3.imprint","IMPRINT",EDGE,{"derivedFrom":sQuery(id+"F3.wireOp",EDGE,"E2.14.9.0")}),-1.0]])]});
            var Q90;
            Q90=makeQuery(id+"F3.imprint","IMPRINT",FACE,{"disambiguationData":[TD([[makeQuery(id+"F3.imprint","IMPRINT",EDGE,{"derivedFrom":sQuery(id+"F3.wireOp",EDGE,"E2.7.16.0")}),-1.0]])]});
            var Q91;
            Q91=makeQuery(id+"F3.imprint","IMPRINT",FACE,{"disambiguationData":[TD([[makeQuery(id+"F3.imprint","IMPRINT",EDGE,{"derivedFrom":sQuery(id+"F3.wireOp",EDGE,"E2.8.15.0")}),-1.0]])]});
            var Q92;
            Q92=makeQuery(id+"F3.imprint","IMPRINT",FACE,{"disambiguationData":[TD([[makeQuery(id+"F3.imprint","IMPRINT",EDGE,{"derivedFrom":sQuery(id+"F3.wireOp",EDGE,"E2.9.14.0")}),-1.0]])]});
            var Q93;
            Q93=makeQuery(id+"F3.imprint","IMPRINT",FACE,{"disambiguationData":[TD([[makeQuery(id+"F3.imprint","IMPRINT",EDGE,{"derivedFrom":sQuery(id+"F3.wireOp",EDGE,"E2.10.13.0")}),-1.0]])]});
            var Q94;
            Q94=makeQuery(id+"F3.imprint","IMPRINT",FACE,{"disambiguationData":[TD([[makeQuery(id+"F3.imprint","IMPRINT",EDGE,{"derivedFrom":sQuery(id+"F3.wireOp",EDGE,"E2.4.3.0")}),-1.0]])]});
            var Q95;
            Q95=makeQuery(id+"F3.imprint","IMPRINT",FACE,{"disambiguationData":[TD([[makeQuery(id+"F3.imprint","IMPRINT",EDGE,{"derivedFrom":sQuery(id+"F3.wireOp",EDGE,"E2.5.2.0")}),-1.0]])]});
            var Q96;
            Q96=makeQuery(id+"F3.imprint","IMPRINT",FACE,{"disambiguationData":[TD([[makeQuery(id+"F3.imprint","IMPRINT",EDGE,{"derivedFrom":sQuery(id+"F3.wireOp",EDGE,"E2.6.1.0")}),-1.0]])]});
            var Q97;
            Q97=makeQuery(id+"F3.imprint","IMPRINT",FACE,{"disambiguationData":[TD([[makeQuery(id+"F3.imprint","IMPRINT",EDGE,{"derivedFrom":sQuery(id+"F3.wireOp",EDGE,"E2.7.0.0")}),-1.0]])]});
            var Q98;
            Q98=makeQuery(id+"F3.imprint","IMPRINT",FACE,{"disambiguationData":[TD([[makeQuery(id+"F3.imprint","IMPRINT",EDGE,{"derivedFrom":sQuery(id+"F3.wireOp",EDGE,"E2.16.6.0")}),-1.0]])]});
            var Q99;
            Q99=makeQuery(id+"F3.imprint","IMPRINT",FACE,{"disambiguationData":[TD([[makeQuery(id+"F3.imprint","IMPRINT",EDGE,{"derivedFrom":sQuery(id+"F3.wireOp",EDGE,"E2.12.0.0")}),-1.0]])]});
            var Q100;
            Q100=makeQuery(id+"F3.imprint","IMPRINT",FACE,{"disambiguationData":[TD([[makeQuery(id+"F3.imprint","IMPRINT",EDGE,{"derivedFrom":sQuery(id+"F3.wireOp",EDGE,"E2.11.11.0")}),-1.0]])]});
            var Q101;
            Q101=makeQuery(id+"F3.imprint","IMPRINT",FACE,{"disambiguationData":[TD([[makeQuery(id+"F3.imprint","IMPRINT",EDGE,{"derivedFrom":sQuery(id+"F3.wireOp",EDGE,"E2.12.10.0")}),-1.0]])]});
            var Q102;
            Q102=makeQuery(id+"F3.imprint","IMPRINT",FACE,{"disambiguationData":[TD([[makeQuery(id+"F3.imprint","IMPRINT",EDGE,{"derivedFrom":sQuery(id+"F3.wireOp",EDGE,"E2.13.9.0")}),-1.0]])]});
            var Q103;
            Q103=makeQuery(id+"F3.imprint","IMPRINT",FACE,{"disambiguationData":[TD([[makeQuery(id+"F3.imprint","IMPRINT",EDGE,{"derivedFrom":sQuery(id+"F3.wireOp",EDGE,"E2.14.8.0")}),-1.0]])]});
            var Q104;
            Q104=makeQuery(id+"F3.imprint","IMPRINT",FACE,{"disambiguationData":[TD([[makeQuery(id+"F3.imprint","IMPRINT",EDGE,{"derivedFrom":sQuery(id+"F3.wireOp",EDGE,"E2.7.15.0")}),-1.0]])]});
            var Q105;
            Q105=makeQuery(id+"F3.imprint","IMPRINT",FACE,{"disambiguationData":[TD([[makeQuery(id+"F3.imprint","IMPRINT",EDGE,{"derivedFrom":sQuery(id+"F3.wireOp",EDGE,"E2.8.14.0")}),-1.0]])]});
            var Q106;
            Q106=makeQuery(id+"F3.imprint","IMPRINT",FACE,{"disambiguationData":[TD([[makeQuery(id+"F3.imprint","IMPRINT",EDGE,{"derivedFrom":sQuery(id+"F3.wireOp",EDGE,"E2.9.13.0")}),-1.0]])]});
            var Q107;
            Q107=makeQuery(id+"F3.imprint","IMPRINT",FACE,{"disambiguationData":[TD([[makeQuery(id+"F3.imprint","IMPRINT",EDGE,{"derivedFrom":sQuery(id+"F3.wireOp",EDGE,"E2.10.12.0")}),-1.0]])]});
            var Q108;
            Q108=makeQuery(id+"F3.imprint","IMPRINT",FACE,{"disambiguationData":[TD([[makeQuery(id+"F3.imprint","IMPRINT",EDGE,{"derivedFrom":sQuery(id+"F3.wireOp",EDGE,"E2.4.2.0")}),-1.0]])]});
            var Q109;
            Q109=makeQuery(id+"F3.imprint","IMPRINT",FACE,{"disambiguationData":[TD([[makeQuery(id+"F3.imprint","IMPRINT",EDGE,{"derivedFrom":sQuery(id+"F3.wireOp",EDGE,"E2.5.1.0")}),-1.0]])]});
            var Q110;
            Q110=makeQuery(id+"F3.imprint","IMPRINT",FACE,{"disambiguationData":[TD([[makeQuery(id+"F3.imprint","IMPRINT",EDGE,{"derivedFrom":sQuery(id+"F3.wireOp",EDGE,"E2.6.0.0")}),-1.0]])]});
            var Q111;
            Q111=makeQuery(id+"F3.imprint","IMPRINT",FACE,{"disambiguationData":[TD([[makeQuery(id+"F3.imprint","IMPRINT",EDGE,{"derivedFrom":sQuery(id+"F3.wireOp",EDGE,"E2.6.16.0")}),-1.0]])]});
            var Q112;
            Q112=makeQuery(id+"F3.imprint","IMPRINT",FACE,{"disambiguationData":[TD([[makeQuery(id+"F3.imprint","IMPRINT",EDGE,{"derivedFrom":sQuery(id+"F3.wireOp",EDGE,"E2.1.5.0")}),-1.0]])]});
            var Q113;
            Q113=makeQuery(id+"F3.imprint","IMPRINT",FACE,{"disambiguationData":[TD([[makeQuery(id+"F3.imprint","IMPRINT",EDGE,{"derivedFrom":sQuery(id+"F3.wireOp",EDGE,"E2.2.4.0")}),-1.0]])]});
            var Q114;
            Q114=makeQuery(id+"F3.imprint","IMPRINT",FACE,{"disambiguationData":[TD([[makeQuery(id+"F3.imprint","IMPRINT",EDGE,{"derivedFrom":sQuery(id+"F3.wireOp",EDGE,"E2.3.3.0")}),-1.0]])]});
            var Q115;
            Q115=makeQuery(id+"F3.imprint","IMPRINT",FACE,{"disambiguationData":[TD([[makeQuery(id+"F3.imprint","IMPRINT",EDGE,{"derivedFrom":sQuery(id+"F3.wireOp",EDGE,"E2.13.8.0")}),-1.0]])]});
            var Q116;
            Q116=makeQuery(id+"F3.imprint","IMPRINT",FACE,{"disambiguationData":[TD([[makeQuery(id+"F3.imprint","IMPRINT",EDGE,{"derivedFrom":sQuery(id+"F3.wireOp",EDGE,"E2.14.7.0")}),-1.0]])]});
            var Q117;
            Q117=makeQuery(id+"F3.imprint","IMPRINT",FACE,{"disambiguationData":[TD([[makeQuery(id+"F3.imprint","IMPRINT",EDGE,{"derivedFrom":sQuery(id+"F3.wireOp",EDGE,"E2.16.5.0")}),-1.0]])]});
            var Q118;
            Q118=makeQuery(id+"F3.imprint","IMPRINT",FACE,{"disambiguationData":[TD([[makeQuery(id+"F3.imprint","IMPRINT",EDGE,{"derivedFrom":sQuery(id+"F3.wireOp",EDGE,"E2.9.12.0")}),-1.0]])]});
            var Q119;
            Q119=makeQuery(id+"F3.imprint","IMPRINT",FACE,{"disambiguationData":[TD([[makeQuery(id+"F3.imprint","IMPRINT",EDGE,{"derivedFrom":sQuery(id+"F3.wireOp",EDGE,"E2.10.11.0")}),-1.0]])]});
            var Q120;
            Q120=makeQuery(id+"F3.imprint","IMPRINT",FACE,{"disambiguationData":[TD([[makeQuery(id+"F3.imprint","IMPRINT",EDGE,{"derivedFrom":sQuery(id+"F3.wireOp",EDGE,"E2.11.10.0")}),-1.0]])]});
            var Q121;
            Q121=makeQuery(id+"F3.imprint","IMPRINT",FACE,{"disambiguationData":[TD([[makeQuery(id+"F3.imprint","IMPRINT",EDGE,{"derivedFrom":sQuery(id+"F3.wireOp",EDGE,"E2.12.9.0")}),-1.0]])]});
            var Q122;
            Q122=makeQuery(id+"F3.imprint","IMPRINT",FACE,{"disambiguationData":[TD([[makeQuery(id+"F3.imprint","IMPRINT",EDGE,{"derivedFrom":sQuery(id+"F3.wireOp",EDGE,"E2.5.16.0")}),-1.0]])]});
            var Q123;
            Q123=makeQuery(id+"F3.imprint","IMPRINT",FACE,{"disambiguationData":[TD([[makeQuery(id+"F3.imprint","IMPRINT",EDGE,{"derivedFrom":sQuery(id+"F3.wireOp",EDGE,"E2.6.15.0")}),-1.0]])]});
            var Q124;
            Q124=makeQuery(id+"F3.imprint","IMPRINT",FACE,{"disambiguationData":[TD([[makeQuery(id+"F3.imprint","IMPRINT",EDGE,{"derivedFrom":sQuery(id+"F3.wireOp",EDGE,"E2.7.14.0")}),-1.0]])]});
            var Q125;
            Q125=makeQuery(id+"F3.imprint","IMPRINT",FACE,{"disambiguationData":[TD([[makeQuery(id+"F3.imprint","IMPRINT",EDGE,{"derivedFrom":sQuery(id+"F3.wireOp",EDGE,"E2.2.3.0")}),-1.0]])]});
            var Q126;
            Q126=makeQuery(id+"F3.imprint","IMPRINT",FACE,{"disambiguationData":[TD([[makeQuery(id+"F3.imprint","IMPRINT",EDGE,{"derivedFrom":sQuery(id+"F3.wireOp",EDGE,"E2.3.2.0")}),-1.0]])]});
            var Q127;
            Q127=makeQuery(id+"F3.imprint","IMPRINT",FACE,{"disambiguationData":[TD([[makeQuery(id+"F3.imprint","IMPRINT",EDGE,{"derivedFrom":sQuery(id+"F3.wireOp",EDGE,"E2.4.1.0")}),-1.0]])]});
            var Q128;
            Q128=makeQuery(id+"F3.imprint","IMPRINT",FACE,{"disambiguationData":[TD([[makeQuery(id+"F3.imprint","IMPRINT",EDGE,{"derivedFrom":sQuery(id+"F3.wireOp",EDGE,"E2.5.0.0")}),-1.0]])]});
            var Q129;
            Q129=makeQuery(id+"F3.imprint","IMPRINT",FACE,{"disambiguationData":[TD([[makeQuery(id+"F3.imprint","IMPRINT",EDGE,{"derivedFrom":sQuery(id+"F3.wireOp",EDGE,"E2.1.4.0")}),-1.0]])]});
            var Q130;
            Q130=makeQuery(id+"F3.imprint","IMPRINT",FACE,{"disambiguationData":[TD([[makeQuery(id+"F3.imprint","IMPRINT",EDGE,{"derivedFrom":sQuery(id+"F3.wireOp",EDGE,"E2.13.7.0")}),-1.0]])]});
            var Q131;
            Q131=makeQuery(id+"F3.imprint","IMPRINT",FACE,{"disambiguationData":[TD([[makeQuery(id+"F3.imprint","IMPRINT",EDGE,{"derivedFrom":sQuery(id+"F3.wireOp",EDGE,"E2.14.6.0")}),-1.0]])]});
            var Q132;
            Q132=makeQuery(id+"F3.imprint","IMPRINT",FACE,{"disambiguationData":[TD([[makeQuery(id+"F3.imprint","IMPRINT",EDGE,{"derivedFrom":sQuery(id+"F3.wireOp",EDGE,"E2.16.4.0")}),-1.0]])]});
            var Q133;
            Q133=makeQuery(id+"F3.imprint","IMPRINT",FACE,{"disambiguationData":[TD([[makeQuery(id+"F3.imprint","IMPRINT",EDGE,{"derivedFrom":sQuery(id+"F3.wireOp",EDGE,"E2.9.11.0")}),-1.0]])]});
            var Q134;
            Q134=makeQuery(id+"F3.imprint","IMPRINT",FACE,{"disambiguationData":[TD([[makeQuery(id+"F3.imprint","IMPRINT",EDGE,{"derivedFrom":sQuery(id+"F3.wireOp",EDGE,"E2.10.10.0")}),-1.0]])]});
            var Q135;
            Q135=makeQuery(id+"F3.imprint","IMPRINT",FACE,{"disambiguationData":[TD([[makeQuery(id+"F3.imprint","IMPRINT",EDGE,{"derivedFrom":sQuery(id+"F3.wireOp",EDGE,"E2.11.9.0")}),-1.0]])]});
            var Q136;
            Q136=makeQuery(id+"F3.imprint","IMPRINT",FACE,{"disambiguationData":[TD([[makeQuery(id+"F3.imprint","IMPRINT",EDGE,{"derivedFrom":sQuery(id+"F3.wireOp",EDGE,"E2.12.8.0")}),-1.0]])]});
            var Q137;
            Q137=makeQuery(id+"F3.imprint","IMPRINT",FACE,{"disambiguationData":[TD([[makeQuery(id+"F3.imprint","IMPRINT",EDGE,{"derivedFrom":sQuery(id+"F3.wireOp",EDGE,"E2.5.15.0")}),-1.0]])]});
            var Q138;
            Q138=makeQuery(id+"F3.imprint","IMPRINT",FACE,{"disambiguationData":[TD([[makeQuery(id+"F3.imprint","IMPRINT",EDGE,{"derivedFrom":sQuery(id+"F3.wireOp",EDGE,"E2.6.14.0")}),-1.0]])]});
            var Q139;
            Q139=makeQuery(id+"F3.imprint","IMPRINT",FACE,{"disambiguationData":[TD([[makeQuery(id+"F3.imprint","IMPRINT",EDGE,{"derivedFrom":sQuery(id+"F3.wireOp",EDGE,"E2.7.13.0")}),-1.0]])]});
            var Q140;
            Q140=makeQuery(id+"F3.imprint","IMPRINT",FACE,{"disambiguationData":[TD([[makeQuery(id+"F3.imprint","IMPRINT",EDGE,{"derivedFrom":sQuery(id+"F3.wireOp",EDGE,"E2.2.2.0")}),-1.0]])]});
            var Q141;
            Q141=makeQuery(id+"F3.imprint","IMPRINT",FACE,{"disambiguationData":[TD([[makeQuery(id+"F3.imprint","IMPRINT",EDGE,{"derivedFrom":sQuery(id+"F3.wireOp",EDGE,"E2.3.1.0")}),-1.0]])]});
            var Q142;
            Q142=makeQuery(id+"F3.imprint","IMPRINT",FACE,{"disambiguationData":[TD([[makeQuery(id+"F3.imprint","IMPRINT",EDGE,{"derivedFrom":sQuery(id+"F3.wireOp",EDGE,"E2.4.0.0")}),-1.0]])]});
            var Q143;
            Q143=makeQuery(id+"F3.imprint","IMPRINT",FACE,{"disambiguationData":[TD([[makeQuery(id+"F3.imprint","IMPRINT",EDGE,{"derivedFrom":sQuery(id+"F3.wireOp",EDGE,"E2.1.3.0")}),-1.0]])]});
            var Q144;
            Q144=makeQuery(id+"F3.imprint","IMPRINT",FACE,{"disambiguationData":[TD([[makeQuery(id+"F3.imprint","IMPRINT",EDGE,{"derivedFrom":sQuery(id+"F3.wireOp",EDGE,"E2.4.16.0")}),-1.0]])]});
            var Q145;
            Q145=makeQuery(id+"F3.imprint","IMPRINT",FACE,{"disambiguationData":[TD([[makeQuery(id+"F3.imprint","IMPRINT",EDGE,{"derivedFrom":sQuery(id+"F3.wireOp",EDGE,"E2.14.5.0")}),-1.0]])]});
            var Q146;
            Q146=makeQuery(id+"F3.imprint","IMPRINT",FACE,{"disambiguationData":[TD([[makeQuery(id+"F3.imprint","IMPRINT",EDGE,{"derivedFrom":sQuery(id+"F3.wireOp",EDGE,"E2.13.6.0")}),-1.0]])]});
            var Q147;
            Q147=makeQuery(id+"F3.imprint","IMPRINT",FACE,{"disambiguationData":[TD([[makeQuery(id+"F3.imprint","IMPRINT",EDGE,{"derivedFrom":sQuery(id+"F3.wireOp",EDGE,"E2.16.3.0")}),-1.0]])]});
            var Q148;
            Q148=makeQuery(id+"F3.imprint","IMPRINT",FACE,{"disambiguationData":[TD([[makeQuery(id+"F3.imprint","IMPRINT",EDGE,{"derivedFrom":sQuery(id+"F3.wireOp",EDGE,"E2.9.10.0")}),-1.0]])]});
            var Q149;
            Q149=makeQuery(id+"F3.imprint","IMPRINT",FACE,{"disambiguationData":[TD([[makeQuery(id+"F3.imprint","IMPRINT",EDGE,{"derivedFrom":sQuery(id+"F3.wireOp",EDGE,"E2.11.8.0")}),-1.0]])]});
            var Q150;
            Q150=makeQuery(id+"F3.imprint","IMPRINT",FACE,{"disambiguationData":[TD([[makeQuery(id+"F3.imprint","IMPRINT",EDGE,{"derivedFrom":sQuery(id+"F3.wireOp",EDGE,"E2.10.9.0")}),-1.0]])]});
            var Q151;
            Q151=makeQuery(id+"F3.imprint","IMPRINT",FACE,{"disambiguationData":[TD([[makeQuery(id+"F3.imprint","IMPRINT",EDGE,{"derivedFrom":sQuery(id+"F3.wireOp",EDGE,"E2.12.7.0")}),-1.0]])]});
            var Q152;
            Q152=makeQuery(id+"F3.imprint","IMPRINT",FACE,{"disambiguationData":[TD([[makeQuery(id+"F3.imprint","IMPRINT",EDGE,{"derivedFrom":sQuery(id+"F3.wireOp",EDGE,"E2.5.14.0")}),-1.0]])]});
            var Q153;
            Q153=makeQuery(id+"F3.imprint","IMPRINT",FACE,{"disambiguationData":[TD([[makeQuery(id+"F3.imprint","IMPRINT",EDGE,{"derivedFrom":sQuery(id+"F3.wireOp",EDGE,"E2.6.13.0")}),-1.0]])]});
            var Q154;
            Q154=makeQuery(id+"F3.imprint","IMPRINT",FACE,{"disambiguationData":[TD([[makeQuery(id+"F3.imprint","IMPRINT",EDGE,{"derivedFrom":sQuery(id+"F3.wireOp",EDGE,"E2.7.12.0")}),-1.0]])]});
            var Q155;
            Q155=makeQuery(id+"F3.imprint","IMPRINT",FACE,{"disambiguationData":[TD([[makeQuery(id+"F3.imprint","IMPRINT",EDGE,{"derivedFrom":sQuery(id+"F3.wireOp",EDGE,"E2.2.1.0")}),-1.0]])]});
            var Q156;
            Q156=makeQuery(id+"F3.imprint","IMPRINT",FACE,{"disambiguationData":[TD([[makeQuery(id+"F3.imprint","IMPRINT",EDGE,{"derivedFrom":sQuery(id+"F3.wireOp",EDGE,"E2.3.0.0")}),-1.0]])]});
            var Q157;
            Q157=makeQuery(id+"F3.imprint","IMPRINT",FACE,{"disambiguationData":[TD([[makeQuery(id+"F3.imprint","IMPRINT",EDGE,{"derivedFrom":sQuery(id+"F3.wireOp",EDGE,"E2.3.16.0")}),-1.0]])]});
            var Q158;
            Q158=makeQuery(id+"F3.imprint","IMPRINT",FACE,{"disambiguationData":[TD([[makeQuery(id+"F3.imprint","IMPRINT",EDGE,{"derivedFrom":sQuery(id+"F3.wireOp",EDGE,"E2.4.15.0")}),-1.0]])]});
            var Q159;
            Q159=makeQuery(id+"F3.imprint","IMPRINT",FACE,{"disambiguationData":[TD([[makeQuery(id+"F3.imprint","IMPRINT",EDGE,{"derivedFrom":sQuery(id+"F3.wireOp",EDGE,"E2.1.2.0")}),-1.0]])]});
            var Q160;
            Q160=makeQuery(id+"F3.imprint","IMPRINT",FACE,{"disambiguationData":[TD([[makeQuery(id+"F3.imprint","IMPRINT",EDGE,{"derivedFrom":sQuery(id+"F3.wireOp",EDGE,"E2.13.5.0")}),-1.0]])]});
            var Q161;
            Q161=makeQuery(id+"F3.imprint","IMPRINT",FACE,{"disambiguationData":[TD([[makeQuery(id+"F3.imprint","IMPRINT",EDGE,{"derivedFrom":sQuery(id+"F3.wireOp",EDGE,"E2.14.4.0")}),-1.0]])]});
            var Q162;
            Q162=makeQuery(id+"F3.imprint","IMPRINT",FACE,{"disambiguationData":[TD([[makeQuery(id+"F3.imprint","IMPRINT",EDGE,{"derivedFrom":sQuery(id+"F3.wireOp",EDGE,"E2.16.2.0")}),-1.0]])]});
            var Q163;
            Q163=makeQuery(id+"F3.imprint","IMPRINT",FACE,{"disambiguationData":[TD([[makeQuery(id+"F3.imprint","IMPRINT",EDGE,{"derivedFrom":sQuery(id+"F3.wireOp",EDGE,"E2.9.9.0")}),-1.0]])]});
            var Q164;
            Q164=makeQuery(id+"F3.imprint","IMPRINT",FACE,{"disambiguationData":[TD([[makeQuery(id+"F3.imprint","IMPRINT",EDGE,{"derivedFrom":sQuery(id+"F3.wireOp",EDGE,"E2.10.8.0")}),-1.0]])]});
            var Q165;
            Q165=makeQuery(id+"F3.imprint","IMPRINT",FACE,{"disambiguationData":[TD([[makeQuery(id+"F3.imprint","IMPRINT",EDGE,{"derivedFrom":sQuery(id+"F3.wireOp",EDGE,"E2.11.7.0")}),-1.0]])]});
            var Q166;
            Q166=makeQuery(id+"F3.imprint","IMPRINT",FACE,{"disambiguationData":[TD([[makeQuery(id+"F3.imprint","IMPRINT",EDGE,{"derivedFrom":sQuery(id+"F3.wireOp",EDGE,"E2.12.6.0")}),-1.0]])]});
            var Q167;
            Q167=makeQuery(id+"F3.imprint","IMPRINT",FACE,{"disambiguationData":[TD([[makeQuery(id+"F3.imprint","IMPRINT",EDGE,{"derivedFrom":sQuery(id+"F3.wireOp",EDGE,"E2.5.13.0")}),-1.0]])]});
            var Q168;
            Q168=makeQuery(id+"F3.imprint","IMPRINT",FACE,{"disambiguationData":[TD([[makeQuery(id+"F3.imprint","IMPRINT",EDGE,{"derivedFrom":sQuery(id+"F3.wireOp",EDGE,"E2.6.12.0")}),-1.0]])]});
            var Q169;
            Q169=makeQuery(id+"F3.imprint","IMPRINT",FACE,{"disambiguationData":[TD([[makeQuery(id+"F3.imprint","IMPRINT",EDGE,{"derivedFrom":sQuery(id+"F3.wireOp",EDGE,"E2.7.11.0")}),-1.0]])]});
            var Q170;
            Q170=makeQuery(id+"F3.imprint","IMPRINT",FACE,{"disambiguationData":[TD([[makeQuery(id+"F3.imprint","IMPRINT",EDGE,{"derivedFrom":sQuery(id+"F3.wireOp",EDGE,"E2.2.0.0")}),-1.0]])]});
            var Q171;
            Q171=makeQuery(id+"F3.imprint","IMPRINT",FACE,{"disambiguationData":[TD([[makeQuery(id+"F3.imprint","IMPRINT",EDGE,{"derivedFrom":sQuery(id+"F3.wireOp",EDGE,"E2.2.16.0")}),-1.0]])]});
            var Q172;
            Q172=makeQuery(id+"F3.imprint","IMPRINT",FACE,{"disambiguationData":[TD([[makeQuery(id+"F3.imprint","IMPRINT",EDGE,{"derivedFrom":sQuery(id+"F3.wireOp",EDGE,"E2.3.15.0")}),-1.0]])]});
            var Q173;
            Q173=makeQuery(id+"F3.imprint","IMPRINT",FACE,{"disambiguationData":[TD([[makeQuery(id+"F3.imprint","IMPRINT",EDGE,{"derivedFrom":sQuery(id+"F3.wireOp",EDGE,"E2.4.14.0")}),-1.0]])]});
            var Q174;
            Q174=makeQuery(id+"F3.imprint","IMPRINT",FACE,{"disambiguationData":[TD([[makeQuery(id+"F3.imprint","IMPRINT",EDGE,{"derivedFrom":sQuery(id+"F3.wireOp",EDGE,"E2.1.1.0")}),-1.0]])]});
            var Q175;
            Q175=makeQuery(id+"F3.imprint","IMPRINT",FACE,{"disambiguationData":[TD([[makeQuery(id+"F3.imprint","IMPRINT",EDGE,{"derivedFrom":sQuery(id+"F3.wireOp",EDGE,"E2.13.4.0")}),-1.0]])]});
            var Q176;
            Q176=makeQuery(id+"F3.imprint","IMPRINT",FACE,{"disambiguationData":[TD([[makeQuery(id+"F3.imprint","IMPRINT",EDGE,{"derivedFrom":sQuery(id+"F3.wireOp",EDGE,"E2.14.3.0")}),-1.0]])]});
            var Q177;
            Q177=makeQuery(id+"F3.imprint","IMPRINT",FACE,{"disambiguationData":[TD([[makeQuery(id+"F3.imprint","IMPRINT",EDGE,{"derivedFrom":sQuery(id+"F3.wireOp",EDGE,"E2.16.1.0")}),-1.0]])]});
            var Q178;
            Q178=makeQuery(id+"F3.imprint","IMPRINT",FACE,{"disambiguationData":[TD([[makeQuery(id+"F3.imprint","IMPRINT",EDGE,{"derivedFrom":sQuery(id+"F3.wireOp",EDGE,"E2.11.6.0")}),-1.0]])]});
            var Q179;
            Q179=makeQuery(id+"F3.imprint","IMPRINT",FACE,{"disambiguationData":[TD([[makeQuery(id+"F3.imprint","IMPRINT",EDGE,{"derivedFrom":sQuery(id+"F3.wireOp",EDGE,"E2.10.7.0")}),-1.0]])]});
            var Q180;
            Q180=makeQuery(id+"F3.imprint","IMPRINT",FACE,{"disambiguationData":[TD([[makeQuery(id+"F3.imprint","IMPRINT",EDGE,{"derivedFrom":sQuery(id+"F3.wireOp",EDGE,"E2.9.8.0")}),-1.0]])]});
            var Q181;
            Q181=makeQuery(id+"F3.imprint","IMPRINT",FACE,{"disambiguationData":[TD([[makeQuery(id+"F3.imprint","IMPRINT",EDGE,{"derivedFrom":sQuery(id+"F3.wireOp",EDGE,"E2.12.5.0")}),-1.0]])]});
            var Q182;
            Q182=makeQuery(id+"F3.imprint","IMPRINT",FACE,{"disambiguationData":[TD([[makeQuery(id+"F3.imprint","IMPRINT",EDGE,{"derivedFrom":sQuery(id+"F3.wireOp",EDGE,"E2.5.12.0")}),-1.0]])]});
            var Q183;
            Q183=makeQuery(id+"F3.imprint","IMPRINT",FACE,{"disambiguationData":[TD([[makeQuery(id+"F3.imprint","IMPRINT",EDGE,{"derivedFrom":sQuery(id+"F3.wireOp",EDGE,"E2.7.10.0")}),-1.0]])]});
            var Q184;
            Q184=makeQuery(id+"F3.imprint","IMPRINT",FACE,{"disambiguationData":[TD([[makeQuery(id+"F3.imprint","IMPRINT",EDGE,{"derivedFrom":sQuery(id+"F3.wireOp",EDGE,"E2.6.11.0")}),-1.0]])]});
            var Q185;
            Q185=makeQuery(id+"F3.imprint","IMPRINT",FACE,{"disambiguationData":[TD([[makeQuery(id+"F3.imprint","IMPRINT",EDGE,{"derivedFrom":sQuery(id+"F3.wireOp",EDGE,"E2.1.16.0")}),-1.0]])]});
            var Q186;
            Q186=makeQuery(id+"F3.imprint","IMPRINT",FACE,{"disambiguationData":[TD([[makeQuery(id+"F3.imprint","IMPRINT",EDGE,{"derivedFrom":sQuery(id+"F3.wireOp",EDGE,"E2.2.15.0")}),-1.0]])]});
            var Q187;
            Q187=makeQuery(id+"F3.imprint","IMPRINT",FACE,{"disambiguationData":[TD([[makeQuery(id+"F3.imprint","IMPRINT",EDGE,{"derivedFrom":sQuery(id+"F3.wireOp",EDGE,"E2.3.14.0")}),-1.0]])]});
            var Q188;
            Q188=makeQuery(id+"F3.imprint","IMPRINT",FACE,{"disambiguationData":[TD([[makeQuery(id+"F3.imprint","IMPRINT",EDGE,{"derivedFrom":sQuery(id+"F3.wireOp",EDGE,"E2.4.13.0")}),-1.0]])]});
            var Q189;
            Q189=makeQuery(id+"F3.imprint","IMPRINT",FACE,{"disambiguationData":[TD([[makeQuery(id+"F3.imprint","IMPRINT",EDGE,{"derivedFrom":sQuery(id+"F3.wireOp",EDGE,"E2.1.0.0")}),-1.0]])]});
            var Q190;
            Q190=makeQuery(id+"F3.imprint","IMPRINT",FACE,{"disambiguationData":[TD([[makeQuery(id+"F3.imprint","IMPRINT",EDGE,{"derivedFrom":sQuery(id+"F3.wireOp",EDGE,"E2.16.16.0")}),-1.0]])]});
            var Q191;
            Q191=makeQuery(id+"F3.imprint","IMPRINT",FACE,{"disambiguationData":[TD([[makeQuery(id+"F3.imprint","IMPRINT",EDGE,{"derivedFrom":sQuery(id+"F3.wireOp",EDGE,"E2.13.3.0")}),-1.0]])]});
            var Q192;
            Q192=makeQuery(id+"F3.imprint","IMPRINT",FACE,{"disambiguationData":[TD([[makeQuery(id+"F3.imprint","IMPRINT",EDGE,{"derivedFrom":sQuery(id+"F3.wireOp",EDGE,"E2.14.2.0")}),-1.0]])]});
            var Q193;
            Q193=makeQuery(id+"F3.imprint","IMPRINT",FACE,{"disambiguationData":[TD([[makeQuery(id+"F3.imprint","IMPRINT",EDGE,{"derivedFrom":sQuery(id+"F3.wireOp",EDGE,"E2.16.0.0")}),-1.0]])]});
            var Q194;
            Q194=makeQuery(id+"F3.imprint","IMPRINT",FACE,{"disambiguationData":[TD([[makeQuery(id+"F3.imprint","IMPRINT",EDGE,{"derivedFrom":sQuery(id+"F3.wireOp",EDGE,"E2.9.7.0")}),-1.0]])]});
            var Q195;
            Q195=makeQuery(id+"F3.imprint","IMPRINT",FACE,{"disambiguationData":[TD([[makeQuery(id+"F3.imprint","IMPRINT",EDGE,{"derivedFrom":sQuery(id+"F3.wireOp",EDGE,"E2.11.5.0")}),-1.0]])]});
            var Q196;
            Q196=makeQuery(id+"F3.imprint","IMPRINT",FACE,{"disambiguationData":[TD([[makeQuery(id+"F3.imprint","IMPRINT",EDGE,{"derivedFrom":sQuery(id+"F3.wireOp",EDGE,"E2.10.6.0")}),-1.0]])]});
            var Q197;
            Q197=makeQuery(id+"F3.imprint","IMPRINT",FACE,{"disambiguationData":[TD([[makeQuery(id+"F3.imprint","IMPRINT",EDGE,{"derivedFrom":sQuery(id+"F3.wireOp",EDGE,"E2.12.4.0")}),-1.0]])]});
            var Q198;
            Q198=makeQuery(id+"F3.imprint","IMPRINT",FACE,{"disambiguationData":[TD([[makeQuery(id+"F3.imprint","IMPRINT",EDGE,{"derivedFrom":sQuery(id+"F3.wireOp",EDGE,"E2.5.11.0")}),-1.0]])]});
            var Q199;
            Q199=makeQuery(id+"F3.imprint","IMPRINT",FACE,{"disambiguationData":[TD([[makeQuery(id+"F3.imprint","IMPRINT",EDGE,{"derivedFrom":sQuery(id+"F3.wireOp",EDGE,"E2.6.10.0")}),-1.0]])]});
            var Q200;
            Q200=makeQuery(id+"F3.imprint","IMPRINT",FACE,{"disambiguationData":[TD([[makeQuery(id+"F3.imprint","IMPRINT",EDGE,{"derivedFrom":sQuery(id+"F3.wireOp",EDGE,"E2.7.9.0")}),-1.0]])]});
            var Q201;
            Q201=makeQuery(id+"F3.imprint","IMPRINT",FACE,{"disambiguationData":[TD([[makeQuery(id+"F3.imprint","IMPRINT",EDGE,{"derivedFrom":sQuery(id+"F3.wireOp",EDGE,"E2.2.14.0")}),-1.0]])]});
            var Q202;
            Q202=makeQuery(id+"F3.imprint","IMPRINT",FACE,{"disambiguationData":[TD([[makeQuery(id+"F3.imprint","IMPRINT",EDGE,{"derivedFrom":sQuery(id+"F3.wireOp",EDGE,"E2.1.15.0")}),-1.0]])]});
            var Q203;
            Q203=makeQuery(id+"F3.imprint","IMPRINT",FACE,{"disambiguationData":[TD([[makeQuery(id+"F3.imprint","IMPRINT",EDGE,{"derivedFrom":sQuery(id+"F3.wireOp",EDGE,"E2.3.13.0")}),-1.0]])]});
            var Q204;
            Q204=makeQuery(id+"F3.imprint","IMPRINT",FACE,{"disambiguationData":[TD([[makeQuery(id+"F3.imprint","IMPRINT",EDGE,{"derivedFrom":sQuery(id+"F3.wireOp",EDGE,"E2.4.12.0")}),-1.0]])]});
            var Q205;
            Q205=makeQuery(id+"F3.imprint","IMPRINT",FACE,{"disambiguationData":[TD([[makeQuery(id+"F3.imprint","IMPRINT",EDGE,{"derivedFrom":sQuery(id+"F3.wireOp",EDGE,"E2.12.16.0")}),-1.0]])]});
            var Q206;
            Q206=makeQuery(id+"F3.imprint","IMPRINT",FACE,{"disambiguationData":[TD([[makeQuery(id+"F3.imprint","IMPRINT",EDGE,{"derivedFrom":sQuery(id+"F3.wireOp",EDGE,"E2.13.15.0")}),-1.0]])]});
            var Q207;
            Q207=makeQuery(id+"F3.imprint","IMPRINT",FACE,{"disambiguationData":[TD([[makeQuery(id+"F3.imprint","IMPRINT",EDGE,{"derivedFrom":sQuery(id+"F3.wireOp",EDGE,"E2.14.14.0")}),-1.0]])]});
            var Q208;
            Q208=makeQuery(id+"F3.imprint","IMPRINT",FACE,{"disambiguationData":[TD([[makeQuery(id+"F3.imprint","IMPRINT",EDGE,{"derivedFrom":sQuery(id+"F3.wireOp",EDGE,"E2.16.14.0")}),-1.0]])]});
            var Q209;
            Q209=makeQuery(id+"F3.imprint","IMPRINT",FACE,{"disambiguationData":[TD([[makeQuery(id+"F3.imprint","IMPRINT",EDGE,{"derivedFrom":sQuery(id+"F3.wireOp",EDGE,"E2.14.0.0")}),-1.0]])]});
            var Q210;
            Q210=makeQuery(id+"F3.imprint","IMPRINT",FACE,{"disambiguationData":[TD([[makeQuery(id+"F3.imprint","IMPRINT",EDGE,{"derivedFrom":sQuery(id+"F3.wireOp",EDGE,"E2.13.1.0")}),-1.0]])]});
            var Q211;
            Q211=makeQuery(id+"F3.imprint","IMPRINT",FACE,{"disambiguationData":[TD([[makeQuery(id+"F3.imprint","IMPRINT",EDGE,{"derivedFrom":sQuery(id+"F3.wireOp",EDGE,"E2.14.16.0")}),-1.0]])]});
            var Q212;
            Q212=makeQuery(id+"F3.imprint","IMPRINT",FACE,{"disambiguationData":[TD([[makeQuery(id+"F3.imprint","IMPRINT",EDGE,{"derivedFrom":sQuery(id+"F3.wireOp",EDGE,"E2.9.5.0")}),-1.0]])]});
            var Q213;
            Q213=makeQuery(id+"F3.imprint","IMPRINT",FACE,{"disambiguationData":[TD([[makeQuery(id+"F3.imprint","IMPRINT",EDGE,{"derivedFrom":sQuery(id+"F3.wireOp",EDGE,"E2.10.4.0")}),-1.0]])]});
            var Q214;
            Q214=makeQuery(id+"F3.imprint","IMPRINT",FACE,{"disambiguationData":[TD([[makeQuery(id+"F3.imprint","IMPRINT",EDGE,{"derivedFrom":sQuery(id+"F3.wireOp",EDGE,"E2.11.3.0")}),-1.0]])]});
            var Q215;
            Q215=makeQuery(id+"F3.imprint","IMPRINT",FACE,{"disambiguationData":[TD([[makeQuery(id+"F3.imprint","IMPRINT",EDGE,{"derivedFrom":sQuery(id+"F3.wireOp",EDGE,"E2.12.2.0")}),-1.0]])]});
            var Q216;
            Q216=makeQuery(id+"F3.imprint","IMPRINT",FACE,{"disambiguationData":[TD([[makeQuery(id+"F3.imprint","IMPRINT",EDGE,{"derivedFrom":sQuery(id+"F3.wireOp",EDGE,"E2.5.9.0")}),-1.0]])]});
            var Q217;
            Q217=makeQuery(id+"F3.imprint","IMPRINT",FACE,{"disambiguationData":[TD([[makeQuery(id+"F3.imprint","IMPRINT",EDGE,{"derivedFrom":sQuery(id+"F3.wireOp",EDGE,"E2.6.8.0")}),-1.0]])]});
            var Q218;
            Q218=makeQuery(id+"F3.imprint","IMPRINT",FACE,{"disambiguationData":[TD([[makeQuery(id+"F3.imprint","IMPRINT",EDGE,{"derivedFrom":sQuery(id+"F3.wireOp",EDGE,"E2.7.7.0")}),-1.0]])]});
            var Q219;
            Q219=makeQuery(id+"F3.imprint","IMPRINT",FACE,{"disambiguationData":[TD([[makeQuery(id+"F3.imprint","IMPRINT",EDGE,{"derivedFrom":sQuery(id+"F3.wireOp",EDGE,"E2.1.13.0")}),-1.0]])]});
            var Q220;
            Q220=makeQuery(id+"F3.imprint","IMPRINT",FACE,{"disambiguationData":[TD([[makeQuery(id+"F3.imprint","IMPRINT",EDGE,{"derivedFrom":sQuery(id+"F3.wireOp",EDGE,"E2.2.12.0")}),-1.0]])]});
            var Q221;
            Q221=makeQuery(id+"F3.imprint","IMPRINT",FACE,{"disambiguationData":[TD([[makeQuery(id+"F3.imprint","IMPRINT",EDGE,{"derivedFrom":sQuery(id+"F3.wireOp",EDGE,"E2.3.11.0")}),-1.0]])]});
            var Q222;
            Q222=makeQuery(id+"F3.imprint","IMPRINT",FACE,{"disambiguationData":[TD([[makeQuery(id+"F3.imprint","IMPRINT",EDGE,{"derivedFrom":sQuery(id+"F3.wireOp",EDGE,"E2.4.10.0")}),-1.0]])]});
            var Q223;
            Q223=makeQuery(id+"F3.imprint","IMPRINT",FACE,{"disambiguationData":[TD([[makeQuery(id+"F3.imprint","IMPRINT",EDGE,{"derivedFrom":sQuery(id+"F3.wireOp",EDGE,"E2.16.13.0")}),-1.0]])]});
            var Q224;
            Q224=makeQuery(id+"F3.imprint","IMPRINT",FACE,{"disambiguationData":[TD([[makeQuery(id+"F3.imprint","IMPRINT",EDGE,{"derivedFrom":sQuery(id+"F3.wireOp",EDGE,"E2.13.0.0")}),-1.0]])]});
            var Q225;
            Q225=makeQuery(id+"F3.imprint","IMPRINT",FACE,{"disambiguationData":[TD([[makeQuery(id+"F3.imprint","IMPRINT",EDGE,{"derivedFrom":sQuery(id+"F3.wireOp",EDGE,"E2.13.16.0")}),-1.0]])]});
            var Q226;
            Q226=makeQuery(id+"F3.imprint","IMPRINT",FACE,{"disambiguationData":[TD([[makeQuery(id+"F3.imprint","IMPRINT",EDGE,{"derivedFrom":sQuery(id+"F3.wireOp",EDGE,"E2.14.15.0")}),-1.0]])]});
            var Q227;
            Q227=makeQuery(id+"F3.imprint","IMPRINT",FACE,{"disambiguationData":[TD([[makeQuery(id+"F3.imprint","IMPRINT",EDGE,{"derivedFrom":sQuery(id+"F3.wireOp",EDGE,"E2.9.4.0")}),-1.0]])]});
            var Q228;
            Q228=makeQuery(id+"F3.imprint","IMPRINT",FACE,{"disambiguationData":[TD([[makeQuery(id+"F3.imprint","IMPRINT",EDGE,{"derivedFrom":sQuery(id+"F3.wireOp",EDGE,"E2.11.2.0")}),-1.0]])]});
            var Q229;
            Q229=makeQuery(id+"F3.imprint","IMPRINT",FACE,{"disambiguationData":[TD([[makeQuery(id+"F3.imprint","IMPRINT",EDGE,{"derivedFrom":sQuery(id+"F3.wireOp",EDGE,"E2.10.3.0")}),-1.0]])]});
            var Q230;
            Q230=makeQuery(id+"F3.imprint","IMPRINT",FACE,{"disambiguationData":[TD([[makeQuery(id+"F3.imprint","IMPRINT",EDGE,{"derivedFrom":sQuery(id+"F3.wireOp",EDGE,"E2.12.1.0")}),-1.0]])]});
            var Q231;
            Q231=makeQuery(id+"F3.imprint","IMPRINT",FACE,{"disambiguationData":[TD([[makeQuery(id+"F3.imprint","IMPRINT",EDGE,{"derivedFrom":sQuery(id+"F3.wireOp",EDGE,"E2.5.8.0")}),-1.0]])]});
            var Q232;
            Q232=makeQuery(id+"F3.imprint","IMPRINT",FACE,{"disambiguationData":[TD([[makeQuery(id+"F3.imprint","IMPRINT",EDGE,{"derivedFrom":sQuery(id+"F3.wireOp",EDGE,"E2.6.7.0")}),-1.0]])]});
            var Q233;
            Q233=makeQuery(id+"F3.imprint","IMPRINT",FACE,{"disambiguationData":[TD([[makeQuery(id+"F3.imprint","IMPRINT",EDGE,{"derivedFrom":sQuery(id+"F3.wireOp",EDGE,"E2.7.6.0")}),-1.0]])]});
            var Q234;
            Q234=makeQuery(id+"F3.imprint","IMPRINT",FACE,{"disambiguationData":[TD([[makeQuery(id+"F3.imprint","IMPRINT",EDGE,{"derivedFrom":sQuery(id+"F3.wireOp",EDGE,"E2.1.12.0")}),-1.0]])]});
            var Q235;
            Q235=makeQuery(id+"F3.imprint","IMPRINT",FACE,{"disambiguationData":[TD([[makeQuery(id+"F3.imprint","IMPRINT",EDGE,{"derivedFrom":sQuery(id+"F3.wireOp",EDGE,"E2.2.11.0")}),-1.0]])]});
            var Q236;
            Q236=makeQuery(id+"F3.imprint","IMPRINT",FACE,{"disambiguationData":[TD([[makeQuery(id+"F3.imprint","IMPRINT",EDGE,{"derivedFrom":sQuery(id+"F3.wireOp",EDGE,"E2.3.10.0")}),-1.0]])]});
            var Q237;
            Q237=makeQuery(id+"F3.imprint","IMPRINT",FACE,{"disambiguationData":[TD([[makeQuery(id+"F3.imprint","IMPRINT",EDGE,{"derivedFrom":sQuery(id+"F3.wireOp",EDGE,"E2.4.9.0")}),-1.0]])]});
            var Q238;
            Q238=makeQuery(id+"F3.imprint","IMPRINT",FACE,{"disambiguationData":[TD([[makeQuery(id+"F3.imprint","IMPRINT",EDGE,{"derivedFrom":sQuery(id+"F3.wireOp",EDGE,"E2.6.9.0")}),-1.0]])]});
            var Q239;
            Q239=makeQuery(id+"F3.imprint","IMPRINT",FACE,{"disambiguationData":[TD([[makeQuery(id+"F3.imprint","IMPRINT",EDGE,{"derivedFrom":sQuery(id+"F3.wireOp",EDGE,"E2.7.8.0")}),-1.0]])]});
            var Q240;
            Q240=makeQuery(id+"F3.imprint","IMPRINT",FACE,{"disambiguationData":[TD([[makeQuery(id+"F3.imprint","IMPRINT",EDGE,{"derivedFrom":sQuery(id+"F3.wireOp",EDGE,"E2.9.6.0")}),-1.0]])]});
            var Q241;
            Q241=makeQuery(id+"F3.imprint","IMPRINT",FACE,{"disambiguationData":[TD([[makeQuery(id+"F3.imprint","IMPRINT",EDGE,{"derivedFrom":sQuery(id+"F3.wireOp",EDGE,"E2.2.13.0")}),-1.0]])]});
            var Q242;
            Q242=makeQuery(id+"F3.imprint","IMPRINT",FACE,{"disambiguationData":[TD([[makeQuery(id+"F3.imprint","IMPRINT",EDGE,{"derivedFrom":sQuery(id+"F3.wireOp",EDGE,"E2.3.12.0")}),-1.0]])]});
            var Q243;
            Q243=makeQuery(id+"F3.imprint","IMPRINT",FACE,{"disambiguationData":[TD([[makeQuery(id+"F3.imprint","IMPRINT",EDGE,{"derivedFrom":sQuery(id+"F3.wireOp",EDGE,"E2.4.11.0")}),-1.0]])]});
            var Q244;
            Q244=makeQuery(id+"F3.imprint","IMPRINT",FACE,{"disambiguationData":[TD([[makeQuery(id+"F3.imprint","IMPRINT",EDGE,{"derivedFrom":sQuery(id+"F3.wireOp",EDGE,"E2.5.10.0")}),-1.0]])]});
            var Q245;
            Q245=makeQuery(id+"F3.imprint","IMPRINT",FACE,{"disambiguationData":[TD([[makeQuery(id+"F3.imprint","IMPRINT",EDGE,{"derivedFrom":sQuery(id+"F3.wireOp",EDGE,"E2.1.14.0")}),-1.0]])]});
            var Q246;
            Q246=makeQuery(id+"F3.imprint","IMPRINT",FACE,{"disambiguationData":[TD([[makeQuery(id+"F3.imprint","IMPRINT",EDGE,{"derivedFrom":sQuery(id+"F3.wireOp",EDGE,"E2.14.1.0")}),-1.0]])]});
            var Q247;
            Q247=makeQuery(id+"F3.imprint","IMPRINT",FACE,{"disambiguationData":[TD([[makeQuery(id+"F3.imprint","IMPRINT",EDGE,{"derivedFrom":sQuery(id+"F3.wireOp",EDGE,"E2.16.15.0")}),-1.0]])]});
            var Q248;
            Q248=makeQuery(id+"F3.imprint","IMPRINT",FACE,{"disambiguationData":[TD([[makeQuery(id+"F3.imprint","IMPRINT",EDGE,{"derivedFrom":sQuery(id+"F3.wireOp",EDGE,"E2.10.5.0")}),-1.0]])]});
            var Q249;
            Q249=makeQuery(id+"F3.imprint","IMPRINT",FACE,{"disambiguationData":[TD([[makeQuery(id+"F3.imprint","IMPRINT",EDGE,{"derivedFrom":sQuery(id+"F3.wireOp",EDGE,"E2.11.4.0")}),-1.0]])]});
            var Q250;
            Q250=makeQuery(id+"F3.imprint","IMPRINT",FACE,{"disambiguationData":[TD([[makeQuery(id+"F3.imprint","IMPRINT",EDGE,{"derivedFrom":sQuery(id+"F3.wireOp",EDGE,"E2.12.3.0")}),-1.0]])]});
            var Q251;
            Q251=makeQuery(id+"F3.imprint","IMPRINT",FACE,{"disambiguationData":[TD([[makeQuery(id+"F3.imprint","IMPRINT",EDGE,{"derivedFrom":sQuery(id+"F3.wireOp",EDGE,"E2.13.2.0")}),-1.0]])]});
            var Q252;
            Q252=makeQuery(id+"F3.imprint","IMPRINT",FACE,{"disambiguationData":[TD([[makeQuery(id+"F3.imprint","IMPRINT",EDGE,{"derivedFrom":sQuery(id+"F3.wireOp",EDGE,"E2.9.3.0")}),-1.0]])]});
            var Q253;
            Q253=makeQuery(id+"F3.imprint","IMPRINT",FACE,{"disambiguationData":[TD([[makeQuery(id+"F3.imprint","IMPRINT",EDGE,{"derivedFrom":sQuery(id+"F3.wireOp",EDGE,"E2.10.2.0")}),-1.0]])]});
            var Q254;
            Q254=makeQuery(id+"F3.imprint","IMPRINT",FACE,{"disambiguationData":[TD([[makeQuery(id+"F3.imprint","IMPRINT",EDGE,{"derivedFrom":sQuery(id+"F3.wireOp",EDGE,"E2.11.1.0")}),-1.0]])]});
            var Q255;
            Q255=makeQuery(id+"F3.imprint","IMPRINT",FACE,{"disambiguationData":[TD([[makeQuery(id+"F3.imprint","IMPRINT",EDGE,{"derivedFrom":sQuery(id+"F3.wireOp",EDGE,"E2.4.8.0")}),-1.0]])]});
            var Q256;
            Q256=makeQuery(id+"F3.imprint","IMPRINT",FACE,{"disambiguationData":[TD([[makeQuery(id+"F3.imprint","IMPRINT",EDGE,{"derivedFrom":sQuery(id+"F3.wireOp",EDGE,"E2.5.7.0")}),-1.0]])]});
            var Q257;
            Q257=makeQuery(id+"F3.imprint","IMPRINT",FACE,{"disambiguationData":[TD([[makeQuery(id+"F3.imprint","IMPRINT",EDGE,{"derivedFrom":sQuery(id+"F3.wireOp",EDGE,"E2.6.6.0")}),-1.0]])]});
            var Q258;
            Q258=makeQuery(id+"F3.imprint","IMPRINT",FACE,{"disambiguationData":[TD([[makeQuery(id+"F3.imprint","IMPRINT",EDGE,{"derivedFrom":sQuery(id+"F3.wireOp",EDGE,"E2.7.5.0")}),-1.0]])]});
            var Q259;
            Q259=makeQuery(id+"F3.imprint","IMPRINT",FACE,{"disambiguationData":[TD([[makeQuery(id+"F3.imprint","IMPRINT",EDGE,{"derivedFrom":sQuery(id+"F3.wireOp",EDGE,"E2.1.11.0")}),-1.0]])]});
            var Q260;
            Q260=makeQuery(id+"F3.imprint","IMPRINT",FACE,{"disambiguationData":[TD([[makeQuery(id+"F3.imprint","IMPRINT",EDGE,{"derivedFrom":sQuery(id+"F3.wireOp",EDGE,"E2.2.10.0")}),-1.0]])]});
            var Q261;
            Q261=makeQuery(id+"F3.imprint","IMPRINT",FACE,{"disambiguationData":[TD([[makeQuery(id+"F3.imprint","IMPRINT",EDGE,{"derivedFrom":sQuery(id+"F3.wireOp",EDGE,"E2.3.9.0")}),-1.0]])]});
            var Q262;
            Q262=makeQuery(id+"F3.imprint","IMPRINT",FACE,{"disambiguationData":[TD([[makeQuery(id+"F3.imprint","IMPRINT",EDGE,{"derivedFrom":sQuery(id+"F3.wireOp",EDGE,"E2.8.13.0")}),-1.0]])]});
            var Q263;
            Q263=makeQuery(id+"F3.imprint","IMPRINT",FACE,{"disambiguationData":[TD([[makeQuery(id+"F3.imprint","IMPRINT",EDGE,{"derivedFrom":sQuery(id+"F3.wireOp",EDGE,"E2.8.12.0")}),-1.0]])]});
            var Q264;
            Q264=makeQuery(id+"F3.imprint","IMPRINT",FACE,{"disambiguationData":[TD([[makeQuery(id+"F3.imprint","IMPRINT",EDGE,{"derivedFrom":sQuery(id+"F3.wireOp",EDGE,"E2.8.11.0")}),-1.0]])]});
            var Q265;
            Q265=makeQuery(id+"F3.imprint","IMPRINT",FACE,{"disambiguationData":[TD([[makeQuery(id+"F3.imprint","IMPRINT",EDGE,{"derivedFrom":sQuery(id+"F3.wireOp",EDGE,"E2.8.10.0")}),-1.0]])]});
            var Q266;
            Q266=makeQuery(id+"F3.imprint","IMPRINT",FACE,{"disambiguationData":[TD([[makeQuery(id+"F3.imprint","IMPRINT",EDGE,{"derivedFrom":sQuery(id+"F3.wireOp",EDGE,"E2.8.9.0")}),-1.0]])]});
            var Q267;
            Q267=makeQuery(id+"F3.imprint","IMPRINT",FACE,{"disambiguationData":[TD([[makeQuery(id+"F3.imprint","IMPRINT",EDGE,{"derivedFrom":sQuery(id+"F3.wireOp",EDGE,"E2.8.8.0")}),-1.0]])]});
            var Q268;
            Q268=makeQuery(id+"F3.imprint","IMPRINT",FACE,{"disambiguationData":[TD([[makeQuery(id+"F3.imprint","IMPRINT",EDGE,{"derivedFrom":sQuery(id+"F3.wireOp",EDGE,"E2.8.6.0")}),-1.0]])]});
            var Q269;
            Q269=makeQuery(id+"F3.imprint","IMPRINT",FACE,{"disambiguationData":[TD([[makeQuery(id+"F3.imprint","IMPRINT",EDGE,{"derivedFrom":sQuery(id+"F3.wireOp",EDGE,"E2.8.5.0")}),-1.0]])]});
            var Q270;
            Q270=makeQuery(id+"F3.imprint","IMPRINT",FACE,{"disambiguationData":[TD([[makeQuery(id+"F3.imprint","IMPRINT",EDGE,{"derivedFrom":sQuery(id+"F3.wireOp",EDGE,"E2.8.7.0")}),-1.0]])]});
            var Q271;
            Q271=makeQuery(id+"F3.imprint","IMPRINT",FACE,{"disambiguationData":[TD([[makeQuery(id+"F3.imprint","IMPRINT",EDGE,{"derivedFrom":sQuery(id+"F3.wireOp",EDGE,"E2.8.4.0")}),-1.0]])]});
            var Q272;
            Q272=makeQuery(id+"F3.imprint","IMPRINT",FACE,{"disambiguationData":[TD([[makeQuery(id+"F3.imprint","IMPRINT",EDGE,{"derivedFrom":sQuery(id+"F3.wireOp",EDGE,"E2.0.12.0")}),-1.0]])]});
            var Q273;
            Q273=makeQuery(id+"F3.imprint","IMPRINT",FACE,{"disambiguationData":[TD([[makeQuery(id+"F3.imprint","IMPRINT",EDGE,{"derivedFrom":sQuery(id+"F3.wireOp",EDGE,"E2.0.11.0")}),-1.0]])]});
            var Q274;
            Q274=makeQuery(id+"F3.imprint","IMPRINT",FACE,{"disambiguationData":[TD([[makeQuery(id+"F3.imprint","IMPRINT",EDGE,{"derivedFrom":sQuery(id+"F3.wireOp",EDGE,"E2.0.10.0")}),-1.0]])]});
            var Q275;
            Q275=makeQuery(id+"F3.imprint","IMPRINT",FACE,{"disambiguationData":[TD([[makeQuery(id+"F3.imprint","IMPRINT",EDGE,{"derivedFrom":sQuery(id+"F3.wireOp",EDGE,"E2.0.9.0")}),-1.0]])]});
            var Q276;
            Q276=makeQuery(id+"F3.imprint","IMPRINT",FACE,{"disambiguationData":[TD([[makeQuery(id+"F3.imprint","IMPRINT",EDGE,{"derivedFrom":sQuery(id+"F3.wireOp",EDGE,"E2.0.7.0")}),-1.0]])]});
            var Q277;
            Q277=makeQuery(id+"F3.imprint","IMPRINT",FACE,{"disambiguationData":[TD([[makeQuery(id+"F3.imprint","IMPRINT",EDGE,{"derivedFrom":sQuery(id+"F3.wireOp",EDGE,"E2.0.8.0")}),-1.0]])]});
            var Q278;
            Q278=makeQuery(id+"F3.imprint","IMPRINT",FACE,{"disambiguationData":[TD([[makeQuery(id+"F3.imprint","IMPRINT",EDGE,{"derivedFrom":sQuery(id+"F3.wireOp",EDGE,"E2.0.6.0")}),-1.0]])]});
            var Q279;
            Q279=makeQuery(id+"F3.imprint","IMPRINT",FACE,{"disambiguationData":[TD([[makeQuery(id+"F3.imprint","IMPRINT",EDGE,{"derivedFrom":sQuery(id+"F3.wireOp",EDGE,"E2.0.5.0")}),-1.0]])]});
            var Q280;
            Q280=makeQuery(id+"F3.imprint","IMPRINT",FACE,{"disambiguationData":[TD([[makeQuery(id+"F3.imprint","IMPRINT",EDGE,{"derivedFrom":sQuery(id+"F3.wireOp",EDGE,"E2.0.4.0")}),-1.0]])]});
            var Q281;
            Q281=makeQuery(id+"F3.imprint","IMPRINT",FACE,{"disambiguationData":[TD([[makeQuery(id+"F3.imprint","IMPRINT",EDGE,{"derivedFrom":sQuery(id+"F3.wireOp",EDGE,"E2.0.3.0")}),-1.0]])]});
            var Q282;
            Q282=makeQuery(id+"F3.imprint","IMPRINT",FACE,{"disambiguationData":[TD([[makeQuery(id+"F3.imprint","IMPRINT",EDGE,{"derivedFrom":sQuery(id+"F3.wireOp",EDGE,"E2.0.2.0")}),-1.0]])]});
            var Q283;
            Q283=makeQuery(id+"F3.imprint","IMPRINT",FACE,{"disambiguationData":[TD([[makeQuery(id+"F3.imprint","IMPRINT",EDGE,{"derivedFrom":sQuery(id+"F3.wireOp",EDGE,"E2.0.14.0")}),-1.0]])]});
            var Q284;
            Q284=makeQuery(id+"F3.imprint","IMPRINT",FACE,{"disambiguationData":[TD([[makeQuery(id+"F3.imprint","IMPRINT",EDGE,{"derivedFrom":sQuery(id+"F3.wireOp",EDGE,"E2.0.13.0")}),-1.0]])]});
            var Q285;
            Q285=makeQuery(id+"F3.imprint","IMPRINT",FACE,{"disambiguationData":[TD([[makeQuery(id+"F3.imprint","IMPRINT",EDGE,{"derivedFrom":sQuery(id+"F3.wireOp",EDGE,"E2.0.15.0")}),-1.0]])]});
            var Q286;
            Q286=makeQuery(id+"F3.imprint","IMPRINT",FACE,{"disambiguationData":[TD([[makeQuery(id+"F3.imprint","IMPRINT",EDGE,{"derivedFrom":sQuery(id+"F3.wireOp",EDGE,"E2.0.16.0")}),-1.0]])]});
            var Q287;
            Q287=makeQuery(id+"F3.imprint","IMPRINT",FACE,{"disambiguationData":[TD([[makeQuery(id+"F3.imprint","IMPRINT",EDGE,{"derivedFrom":sQuery(id+"F3.wireOp",EDGE,"E2.0.1.0")}),-1.0]])]});
            var Q288;
            Q288=makeQuery(id+"F3.imprint","IMPRINT",FACE,{"disambiguationData":[TD([[makeQuery(id+"F3.imprint","IMPRINT",EDGE,{"derivedFrom":sQuery(id+"F3.wireOp",EDGE,"E1.0")}),-1.0]])]});
            extrude(context, id + "F4", {"entities" : qUnion([Q0, Q1, Q2, Q3, Q4, Q5, Q6, Q7, Q8, Q9, Q10, Q11, Q12, Q13, Q14, Q15, Q16, Q17, Q18, Q19, Q20, Q21, Q22, Q23, Q24, Q25, Q26, Q27, Q28, Q29, Q30, Q31, Q32, Q33, Q34, Q35, Q36, Q37, Q38, Q39, Q40, Q41, Q42, Q43, Q44, Q45, Q46, Q47, Q48, Q49, Q50, Q51, Q52, Q53, Q54, Q55, Q56, Q57, Q58, Q59, Q60, Q61, Q62, Q63, Q64, Q65, Q66, Q67, Q68, Q69, Q70, Q71, Q72, Q73, Q74, Q75, Q76, Q77, Q78, Q79, Q80, Q81, Q82, Q83, Q84, Q85, Q86, Q87, Q88, Q89, Q90, Q91, Q92, Q93, Q94, Q95, Q96, Q97, Q98, Q99, Q100, Q101, Q102, Q103, Q104, Q105, Q106, Q107, Q108, Q109, Q110, Q111, Q112, Q113, Q114, Q115, Q116, Q117, Q118, Q119, Q120, Q121, Q122, Q123, Q124, Q125, Q126, Q127, Q128, Q129, Q130, Q131, Q132, Q133, Q134, Q135, Q136, Q137, Q138, Q139, Q140, Q141, Q142, Q143, Q144, Q145, Q146, Q147, Q148, Q149, Q150, Q151, Q152, Q153, Q154, Q155, Q156, Q157, Q158, Q159, Q160, Q161, Q162, Q163, Q164, Q165, Q166, Q167, Q168, Q169, Q170, Q171, Q172, Q173, Q174, Q175, Q176, Q177, Q178, Q179, Q180, Q181, Q182, Q183, Q184, Q185, Q186, Q187, Q188, Q189, Q190, Q191, Q192, Q193, Q194, Q195, Q196, Q197, Q198, Q199, Q200, Q201, Q202, Q203, Q204, Q205, Q206, Q207, Q208, Q209, Q210, Q211, Q212, Q213, Q214, Q215, Q216, Q217, Q218, Q219, Q220, Q221, Q222, Q223, Q224, Q225, Q226, Q227, Q228, Q229, Q230, Q231, Q232, Q233, Q234, Q235, Q236, Q237, Q238, Q239, Q240, Q241, Q242, Q243, Q244, Q245, Q246, Q247, Q248, Q249, Q250, Q251, Q252, Q253, Q254, Q255, Q256, Q257, Q258, Q259, Q260, Q261, Q262, Q263, Q264, Q265, Q266, Q267, Q268, Q269, Q270, Q271, Q272, Q273, Q274, Q275, Q276, Q277, Q278, Q279, Q280, Q281, Q282, Q283, Q284, Q285, Q286, Q287, Q288]), "operationType" : NewBodyOperationType.REMOVE, "oppositeDirection" : true, "depth" : 25 * mm, "offsetDistance" : 25 * mm});
        }
    });
